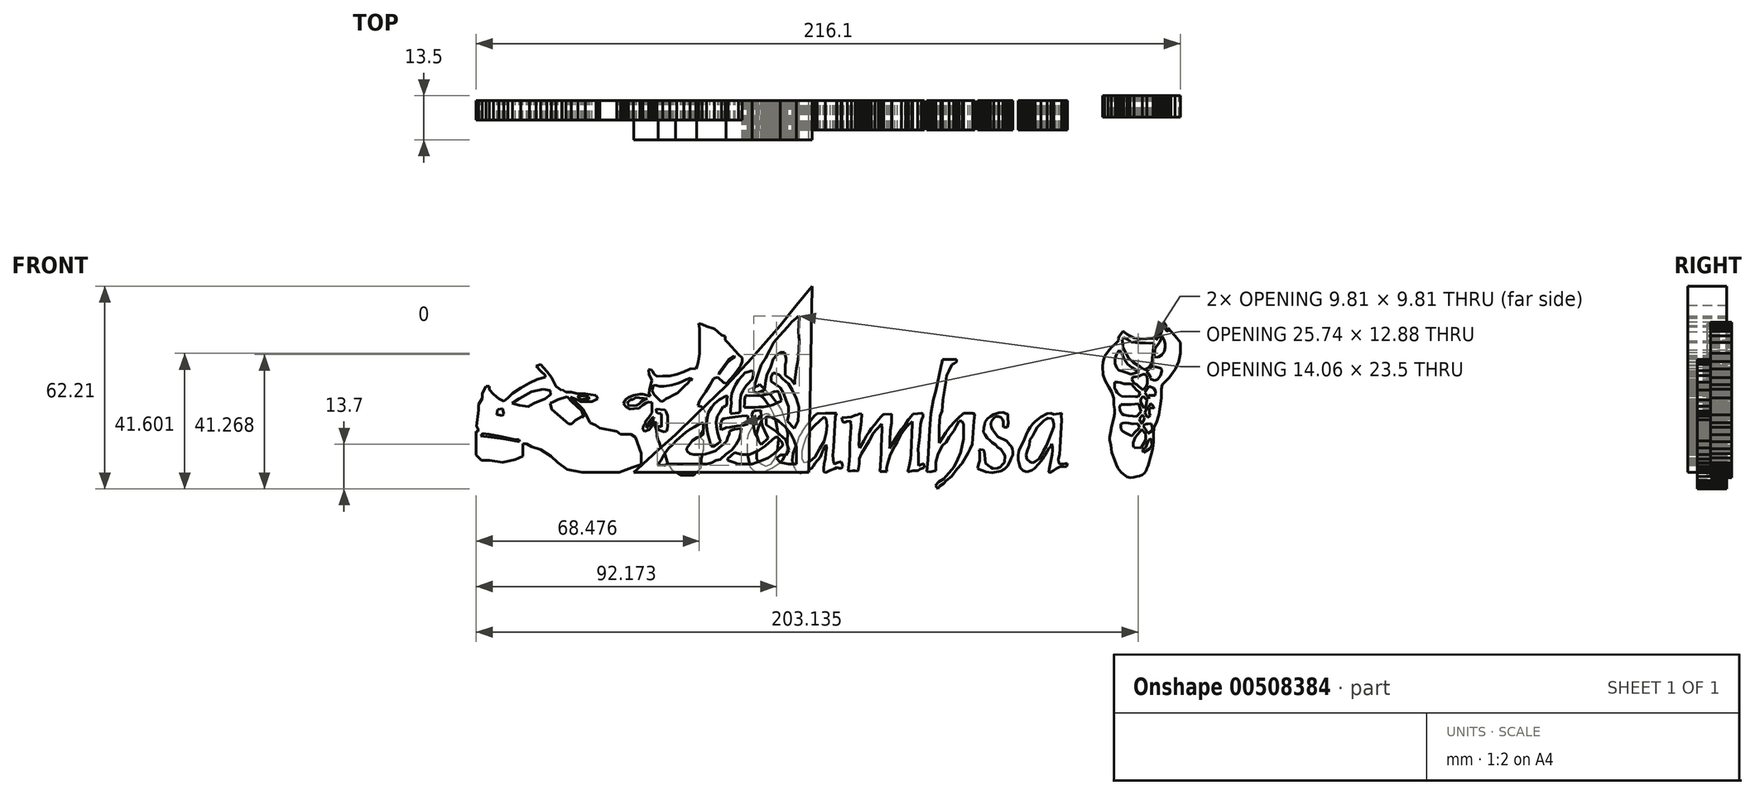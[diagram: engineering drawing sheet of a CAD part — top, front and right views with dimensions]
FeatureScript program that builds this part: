
annotation { "Feature Type Name" : "Feature", "Feature Type Description" : "" }
export const myFeature = defineFeature(function(context is Context, id is Id, definition is map)
    precondition{}
    {
        {
            var Q0;
            Q0=qCreatedBy(makeId("Front.planeOp"),FACE);
            var sketch = newSketch(context, id + "F0", { "sketchPlane" : qUnion([Q0])});
            skLineSegment(sketch, "E0", {"start": v(-52.16, 21.85) * mm, "end": v(-53.77, 22.66) * mm});
            skLineSegment(sketch, "E1", {"start": v(-53.77, 22.66) * mm, "end": v(-55.38, 23.98) * mm});
            skLineSegment(sketch, "E2", {"start": v(-55.38, 23.98) * mm, "end": v(-56.65, 25.48) * mm});
            skLineSegment(sketch, "E3", {"start": v(-56.65, 25.48) * mm, "end": v(-56.65, 26.4) * mm});
            skLineSegment(sketch, "E4", {"start": v(-56.65, 26.4) * mm, "end": v(-57.68, 26.4) * mm});
            skLineSegment(sketch, "E5", {"start": v(-57.68, 26.4) * mm, "end": v(-58.83, 24.27) * mm});
            skLineSegment(sketch, "E6", {"start": v(-58.83, 24.27) * mm, "end": v(-58.83, 22.72) * mm});
            skLineSegment(sketch, "E7", {"start": v(-58.83, 22.72) * mm, "end": v(-59.93, 20.82) * mm});
            skLineSegment(sketch, "E8", {"start": v(-59.93, 20.82) * mm, "end": v(-59.93, 19.15) * mm});
            skLineSegment(sketch, "E9", {"start": v(-59.93, 19.15) * mm, "end": v(-60.56, 14.31) * mm});
            skLineSegment(sketch, "E10", {"start": v(-60.56, 14.31) * mm, "end": v(-60.1, 13.22) * mm});
            skLineSegment(sketch, "E11", {"start": v(-60.1, 13.22) * mm, "end": v(-60.1, 12.58) * mm});
            skLineSegment(sketch, "E12", {"start": v(-60.1, 12.58) * mm, "end": v(-60.68, 12.58) * mm});
            skLineSegment(sketch, "E13", {"start": v(-60.68, 12.58) * mm, "end": v(-60.68, 10.91) * mm});
            skLineSegment(sketch, "E14", {"start": v(-60.68, 10.91) * mm, "end": v(-60.68, 7.7) * mm});
            skLineSegment(sketch, "E15", {"start": v(-60.68, 7.7) * mm, "end": v(-60.68, 5.33) * mm});
            skLineSegment(sketch, "E16", {"start": v(-60.68, 5.33) * mm, "end": v(-59, 3.66) * mm});
            skLineSegment(sketch, "E17", {"start": v(-59, 3.66) * mm, "end": v(-56.47, 3.66) * mm});
            skLineSegment(sketch, "E18", {"start": v(-56.47, 3.66) * mm, "end": v(-52.5, 3.14) * mm});
            skLineSegment(sketch, "E19", {"start": v(-52.5, 3.14) * mm, "end": v(-48.59, 4) * mm});
            skLineSegment(sketch, "E20", {"start": v(-48.59, 4) * mm, "end": v(-46.34, 4.99) * mm});
            skLineSegment(sketch, "E21", {"start": v(-46.34, 4.99) * mm, "end": v(-46.34, 7.17) * mm});
            skLineSegment(sketch, "E22", {"start": v(-46.34, 7.17) * mm, "end": v(-46.34, 8.78) * mm});
            skLineSegment(sketch, "E23", {"start": v(-46.34, 8.78) * mm, "end": v(-45.25, 8.78) * mm});
            skLineSegment(sketch, "E24", {"start": v(-45.25, 8.78) * mm, "end": v(-43.7, 7.92) * mm});
            skLineSegment(sketch, "E25", {"start": v(-43.7, 7.92) * mm, "end": v(-40.93, 7) * mm});
            skLineSegment(sketch, "E26", {"start": v(-40.93, 7) * mm, "end": v(-37.7, 5.04) * mm});
            skLineSegment(sketch, "E27", {"start": v(-37.7, 5.04) * mm, "end": v(-35.64, 3.09) * mm});
            skLineSegment(sketch, "E28", {"start": v(-35.64, 3.09) * mm, "end": v(-32.76, 0.96) * mm});
            skLineSegment(sketch, "E29", {"start": v(-32.76, 0.96) * mm, "end": v(-28.2, 0) * mm});
            skLineSegment(sketch, "E30", {"start": v(-28.2, 0) * mm, "end": v(-23.03, 0) * mm});
            skLineSegment(sketch, "E31", {"start": v(-23.03, 0) * mm, "end": v(-16.7, 0) * mm});
            skLineSegment(sketch, "E32", {"start": v(-16.7, 0) * mm, "end": v(-12.72, 1.53) * mm});
            skLineSegment(sketch, "E33", {"start": v(-12.72, 1.53) * mm, "end": v(-10.02, 2.51) * mm});
            skLineSegment(sketch, "E34", {"start": v(-10.02, 2.51) * mm, "end": v(-10.02, 3.32) * mm});
            skLineSegment(sketch, "E35", {"start": v(-10.02, 3.32) * mm, "end": v(-10.02, 5.9) * mm});
            skLineSegment(sketch, "E36", {"start": v(-10.02, 5.9) * mm, "end": v(-11.8, 10.86) * mm});
            skLineSegment(sketch, "E37", {"start": v(-11.8, 10.86) * mm, "end": v(-13.24, 11.66) * mm});
            skLineSegment(sketch, "E38", {"start": v(-13.24, 11.66) * mm, "end": v(-16.4, 11.66) * mm});
            skLineSegment(sketch, "E39", {"start": v(-16.4, 11.66) * mm, "end": v(-17.5, 12.58) * mm});
            skLineSegment(sketch, "E40", {"start": v(-17.5, 12.58) * mm, "end": v(-22.74, 13.62) * mm});
            skLineSegment(sketch, "E41", {"start": v(-22.74, 13.62) * mm, "end": v(-24, 14.48) * mm});
            skLineSegment(sketch, "E42", {"start": v(-24, 14.48) * mm, "end": v(-25.73, 15.23) * mm});
            skLineSegment(sketch, "E43", {"start": v(-25.73, 15.23) * mm, "end": v(-26.54, 16.96) * mm});
            skLineSegment(sketch, "E44", {"start": v(-26.54, 16.96) * mm, "end": v(-27.92, 19.5) * mm});
            skLineSegment(sketch, "E45", {"start": v(-27.92, 19.5) * mm, "end": v(-30.86, 22.37) * mm});
            skLineSegment(sketch, "E46", {"start": v(-30.86, 22.37) * mm, "end": v(-31.72, 23.12) * mm});
            skLineSegment(sketch, "E47", {"start": v(-31.72, 23.12) * mm, "end": v(-29.42, 22.26) * mm});
            skLineSegment(sketch, "E48", {"start": v(-29.42, 22.26) * mm, "end": v(-28.61, 21.8) * mm});
            skLineSegment(sketch, "E49", {"start": v(-28.61, 21.8) * mm, "end": v(-26.42, 21.8) * mm});
            skLineSegment(sketch, "E50", {"start": v(-26.42, 21.8) * mm, "end": v(-25.1, 21.8) * mm});
            skLineSegment(sketch, "E51", {"start": v(-25.1, 21.8) * mm, "end": v(-23.37, 22.6) * mm});
            skLineSegment(sketch, "E52", {"start": v(-23.37, 22.6) * mm, "end": v(-23.86, 23.64) * mm});
            skLineSegment(sketch, "E53", {"start": v(-23.86, 23.64) * mm, "end": v(-27.12, 24.16) * mm});
            skLineSegment(sketch, "E54", {"start": v(-27.12, 24.16) * mm, "end": v(-29.42, 24.16) * mm});
            skLineSegment(sketch, "E55", {"start": v(-29.42, 24.16) * mm, "end": v(-31.5, 24.62) * mm});
            skLineSegment(sketch, "E56", {"start": v(-31.5, 24.62) * mm, "end": v(-33.16, 24.62) * mm});
            skLineSegment(sketch, "E57", {"start": v(-33.16, 24.62) * mm, "end": v(-34.25, 25.42) * mm});
            skLineSegment(sketch, "E58", {"start": v(-34.25, 25.42) * mm, "end": v(-34.44, 25.17) * mm});
            skLineSegment(sketch, "E59", {"start": v(-34.44, 25.17) * mm, "end": v(-36.19, 26.46) * mm});
            skLineSegment(sketch, "E60", {"start": v(-36.19, 26.46) * mm, "end": v(-37.53, 29.22) * mm});
            skLineSegment(sketch, "E61", {"start": v(-37.53, 29.22) * mm, "end": v(-38.92, 31.06) * mm});
            skLineSegment(sketch, "E62", {"start": v(-38.92, 31.06) * mm, "end": v(-40.93, 33.2) * mm});
            skLineSegment(sketch, "E63", {"start": v(-40.93, 33.2) * mm, "end": v(-42.26, 32.62) * mm});
            skLineSegment(sketch, "E64", {"start": v(-42.26, 32.62) * mm, "end": v(-40.7, 31) * mm});
            skLineSegment(sketch, "E65", {"start": v(-40.7, 31) * mm, "end": v(-39.43, 29.85) * mm});
            skLineSegment(sketch, "E66", {"start": v(-39.43, 29.85) * mm, "end": v(-39.43, 29.22) * mm});
            skLineSegment(sketch, "E67", {"start": v(-39.43, 29.22) * mm, "end": v(-41.85, 28.65) * mm});
            skLineSegment(sketch, "E68", {"start": v(-41.85, 28.65) * mm, "end": v(-44.33, 27.44) * mm});
            skLineSegment(sketch, "E69", {"start": v(-44.33, 27.44) * mm, "end": v(-46.98, 26) * mm});
            skLineSegment(sketch, "E70", {"start": v(-46.98, 26) * mm, "end": v(-49.57, 24.33) * mm});
            skLineSegment(sketch, "E71", {"start": v(-49.57, 24.33) * mm, "end": v(-50.9, 22.95) * mm});
            skLineSegment(sketch, "E72", {"start": v(-50.9, 22.95) * mm, "end": v(-52.16, 21.85) * mm});
            skLineSegment(sketch, "E73", {"start": v(-37.94, 21.22) * mm, "end": v(-37.48, 19.38) * mm});
            skLineSegment(sketch, "E74", {"start": v(-37.48, 19.38) * mm, "end": v(-32.3, 14.89) * mm});
            skLineSegment(sketch, "E75", {"start": v(-32.3, 14.89) * mm, "end": v(-31.32, 14.89) * mm});
            skLineSegment(sketch, "E76", {"start": v(-31.32, 14.89) * mm, "end": v(-30.17, 16.04) * mm});
            skLineSegment(sketch, "E77", {"start": v(-30.17, 16.04) * mm, "end": v(-28.2, 17.13) * mm});
            skLineSegment(sketch, "E78", {"start": v(-28.2, 17.13) * mm, "end": v(-27.7, 16.96) * mm});
            skLineSegment(sketch, "E79", {"start": v(-27.7, 16.96) * mm, "end": v(-28.27, 18.97) * mm});
            skLineSegment(sketch, "E80", {"start": v(-28.27, 18.97) * mm, "end": v(-31.38, 21.77) * mm});
            skPoint(sketch, "E80.endSnap0", {"position": v(-59.38, 21.77) * mm});
            skLineSegment(sketch, "E81", {"start": v(-31.38, 21.77) * mm, "end": v(-32.76, 23.3) * mm});
            skLineSegment(sketch, "E82", {"start": v(-32.76, 23.3) * mm, "end": v(-35.52, 22.43) * mm});
            skLineSegment(sketch, "E83", {"start": v(-35.52, 22.43) * mm, "end": v(-36.84, 21.74) * mm});
            skLineSegment(sketch, "E84", {"start": v(-36.84, 21.74) * mm, "end": v(-37.94, 21.22) * mm});
            skLineSegment(sketch, "E85", {"start": v(-35.12, 21.22) * mm, "end": v(-33.62, 22.14) * mm});
            skLineSegment(sketch, "E86", {"start": v(-33.62, 22.14) * mm, "end": v(-32.63, 22.28) * mm});
            skLineSegment(sketch, "E87", {"start": v(-32.63, 22.28) * mm, "end": v(-31.9, 21.34) * mm});
            skLineSegment(sketch, "E88", {"start": v(-31.9, 21.34) * mm, "end": v(-30.56, 20.1) * mm});
            skLineSegment(sketch, "E89", {"start": v(-30.56, 20.1) * mm, "end": v(-29.1, 19) * mm});
            skLineSegment(sketch, "E90", {"start": v(-29.1, 19) * mm, "end": v(-29.1, 18.34) * mm});
            skLineSegment(sketch, "E91", {"start": v(-29.1, 18.34) * mm, "end": v(-30.3, 17.83) * mm});
            skLineSegment(sketch, "E92", {"start": v(-30.3, 17.83) * mm, "end": v(-31.17, 17.23) * mm});
            skLineSegment(sketch, "E93", {"start": v(-31.17, 17.23) * mm, "end": v(-31.9, 17.68) * mm});
            skLineSegment(sketch, "E94", {"start": v(-31.9, 17.68) * mm, "end": v(-33.02, 18.94) * mm});
            skLineSegment(sketch, "E95", {"start": v(-33.02, 18.94) * mm, "end": v(-33.88, 19.97) * mm});
            skLineSegment(sketch, "E96", {"start": v(-33.88, 19.97) * mm, "end": v(-34.56, 20.6) * mm});
            skLineSegment(sketch, "E97", {"start": v(-34.56, 20.6) * mm, "end": v(-35.12, 21.22) * mm});
            skLineSegment(sketch, "E98", {"start": v(-26.17, 23.22) * mm, "end": v(-28.2, 23.54) * mm});
            skLineSegment(sketch, "E99", {"start": v(-28.2, 23.54) * mm, "end": v(-29.56, 23.54) * mm});
            skLineSegment(sketch, "E100", {"start": v(-29.56, 23.54) * mm, "end": v(-29.32, 23.18) * mm});
            skLineSegment(sketch, "E101", {"start": v(-29.32, 23.18) * mm, "end": v(-28.45, 22.43) * mm});
            skLineSegment(sketch, "E102", {"start": v(-28.45, 22.43) * mm, "end": v(-27.03, 22.67) * mm});
            skLineSegment(sketch, "E103", {"start": v(-27.03, 22.67) * mm, "end": v(-26.03, 22.52) * mm});
            skLineSegment(sketch, "E104", {"start": v(-26.03, 22.52) * mm, "end": v(-26.17, 23.22) * mm});
            skLineSegment(sketch, "E105", {"start": v(-49.66, 21.22) * mm, "end": v(-47.54, 22.67) * mm});
            skLineSegment(sketch, "E106", {"start": v(-47.54, 22.67) * mm, "end": v(-43.66, 24.84) * mm});
            skLineSegment(sketch, "E107", {"start": v(-43.66, 24.84) * mm, "end": v(-40.16, 25.54) * mm});
            skLineSegment(sketch, "E108", {"start": v(-40.16, 25.54) * mm, "end": v(-38.01, 25.2) * mm});
            skLineSegment(sketch, "E109", {"start": v(-38.01, 25.2) * mm, "end": v(-37.8, 23.87) * mm});
            skLineSegment(sketch, "E110", {"start": v(-37.8, 23.87) * mm, "end": v(-39.54, 22.67) * mm});
            skLineSegment(sketch, "E111", {"start": v(-39.54, 22.67) * mm, "end": v(-42.86, 21.22) * mm});
            skLineSegment(sketch, "E112", {"start": v(-42.86, 21.22) * mm, "end": v(-44.7, 20.18) * mm});
            skLineSegment(sketch, "E113", {"start": v(-44.7, 20.18) * mm, "end": v(-47.4, 20.6) * mm});
            skLineSegment(sketch, "E114", {"start": v(-47.4, 20.6) * mm, "end": v(-49.66, 21.22) * mm});
            skLineSegment(sketch, "E115", {"start": v(-59.35, 11.23) * mm, "end": v(-58.72, 11.96) * mm});
            skLineSegment(sketch, "E116", {"start": v(-58.72, 11.96) * mm, "end": v(-56.7, 11.76) * mm});
            skLineSegment(sketch, "E117", {"start": v(-56.7, 11.76) * mm, "end": v(-53.3, 11.13) * mm});
            skLineSegment(sketch, "E118", {"start": v(-53.3, 11.13) * mm, "end": v(-49.28, 10.26) * mm});
            skLineSegment(sketch, "E119", {"start": v(-49.28, 10.26) * mm, "end": v(-47.5, 10.02) * mm});
            skLineSegment(sketch, "E120", {"start": v(-47.5, 10.02) * mm, "end": v(-47.35, 9.44) * mm});
            skLineSegment(sketch, "E121", {"start": v(-47.35, 9.44) * mm, "end": v(-51.46, 10.17) * mm});
            skLineSegment(sketch, "E122", {"start": v(-51.46, 10.17) * mm, "end": v(-55.14, 10.65) * mm});
            skLineSegment(sketch, "E123", {"start": v(-55.14, 10.65) * mm, "end": v(-59.35, 11.23) * mm});
            skLineSegment(sketch, "E124", {"start": v(-54.08, 19.36) * mm, "end": v(-52.58, 19.66) * mm});
            skLineSegment(sketch, "E125", {"start": v(-52.58, 19.66) * mm, "end": v(-52.23, 17.94) * mm});
            skLineSegment(sketch, "E126", {"start": v(-52.23, 17.94) * mm, "end": v(-52.66, 17.45) * mm});
            skLineSegment(sketch, "E127", {"start": v(-52.66, 17.45) * mm, "end": v(-54.32, 17.81) * mm});
            skLineSegment(sketch, "E128", {"start": v(-54.32, 17.81) * mm, "end": v(-54.08, 19.36) * mm});
            skLineSegment(sketch, "E129", {"start": v(-6.02, 22.75) * mm, "end": v(-4.76, 20.8) * mm});
            skLineSegment(sketch, "E130", {"start": v(-4.76, 20.8) * mm, "end": v(-3.96, 17.79) * mm});
            skLineSegment(sketch, "E131", {"start": v(-3.96, 17.79) * mm, "end": v(-2.58, 15.86) * mm});
            skLineSegment(sketch, "E132", {"start": v(-2.58, 15.86) * mm, "end": v(0, 14.17) * mm});
            skLineSegment(sketch, "E133", {"start": v(0, 14.17) * mm, "end": v(2.62, 14.17) * mm});
            skLineSegment(sketch, "E134", {"start": v(2.62, 14.17) * mm, "end": v(4.09, 14.17) * mm});
            skLineSegment(sketch, "E135", {"start": v(4.09, 14.17) * mm, "end": v(6.37, 16.45) * mm});
            skLineSegment(sketch, "E136", {"start": v(6.37, 16.45) * mm, "end": v(6.37, 19.18) * mm});
            skLineSegment(sketch, "E137", {"start": v(6.37, 19.18) * mm, "end": v(7.18, 22.3) * mm});
            skLineSegment(sketch, "E138", {"start": v(7.18, 22.3) * mm, "end": v(7.18, 24.67) * mm});
            skLineSegment(sketch, "E139", {"start": v(7.18, 24.67) * mm, "end": v(6.26, 25.57) * mm});
            skLineSegment(sketch, "E140", {"start": v(6.26, 25.57) * mm, "end": v(6.26, 26.6) * mm});
            skLineSegment(sketch, "E141", {"start": v(6.26, 26.6) * mm, "end": v(7.8, 29.07) * mm});
            skLineSegment(sketch, "E142", {"start": v(7.8, 29.07) * mm, "end": v(7.85, 33.37) * mm});
            skLineSegment(sketch, "E143", {"start": v(7.85, 33.37) * mm, "end": v(7.18, 34.4) * mm});
            skLineSegment(sketch, "E144", {"start": v(7.18, 34.4) * mm, "end": v(6.45, 35.3) * mm});
            skLineSegment(sketch, "E145", {"start": v(6.45, 35.3) * mm, "end": v(5.32, 35.46) * mm});
            skLineSegment(sketch, "E146", {"start": v(5.32, 35.46) * mm, "end": v(5.89, 37) * mm});
            skLineSegment(sketch, "E147", {"start": v(5.89, 37) * mm, "end": v(6.68, 38.17) * mm});
            skLineSegment(sketch, "E148", {"start": v(6.68, 38.17) * mm, "end": v(7.78, 39.83) * mm});
            skLineSegment(sketch, "E149", {"start": v(7.78, 39.83) * mm, "end": v(9.12, 41.87) * mm});
            skLineSegment(sketch, "E150", {"start": v(9.12, 41.87) * mm, "end": v(10.26, 43.87) * mm});
            skLineSegment(sketch, "E151", {"start": v(10.26, 43.87) * mm, "end": v(11.51, 44.21) * mm});
            skLineSegment(sketch, "E152", {"start": v(11.51, 44.21) * mm, "end": v(13.22, 42.65) * mm});
            skLineSegment(sketch, "E153", {"start": v(13.22, 42.65) * mm, "end": v(14.1, 42.32) * mm});
            skLineSegment(sketch, "E154", {"start": v(14.1, 42.32) * mm, "end": v(16.44, 44.88) * mm});
            skLineSegment(sketch, "E155", {"start": v(16.44, 44.88) * mm, "end": v(18.49, 47.7) * mm});
            skLineSegment(sketch, "E156", {"start": v(18.49, 47.7) * mm, "end": v(18.92, 49.06) * mm});
            skLineSegment(sketch, "E157", {"start": v(18.92, 49.06) * mm, "end": v(18.92, 50.25) * mm});
            skLineSegment(sketch, "E158", {"start": v(18.92, 50.25) * mm, "end": v(17.84, 51.21) * mm});
            skLineSegment(sketch, "E159", {"start": v(17.84, 51.21) * mm, "end": v(14.6, 54.74) * mm});
            skLineSegment(sketch, "E160", {"start": v(14.6, 54.74) * mm, "end": v(13.8, 55.68) * mm});
            skLineSegment(sketch, "E161", {"start": v(13.8, 55.68) * mm, "end": v(13.8, 56.76) * mm});
            skLineSegment(sketch, "E162", {"start": v(13.8, 56.76) * mm, "end": v(12.64, 57.2) * mm});
            skLineSegment(sketch, "E163", {"start": v(12.64, 57.2) * mm, "end": v(10.42, 59.17) * mm});
            skLineSegment(sketch, "E164", {"start": v(10.42, 59.17) * mm, "end": v(8, 59.93) * mm});
            skLineSegment(sketch, "E165", {"start": v(8, 59.93) * mm, "end": v(6.58, 60.49) * mm});
            skLineSegment(sketch, "E166", {"start": v(6.58, 60.49) * mm, "end": v(5.66, 60.78) * mm});
            skLineSegment(sketch, "E167", {"start": v(5.66, 60.78) * mm, "end": v(5.89, 59.11) * mm});
            skLineSegment(sketch, "E168", {"start": v(5.89, 59.11) * mm, "end": v(5.89, 55.85) * mm});
            skLineSegment(sketch, "E169", {"start": v(5.89, 55.85) * mm, "end": v(5.89, 53.23) * mm});
            skLineSegment(sketch, "E170", {"start": v(5.89, 53.23) * mm, "end": v(5.89, 51.55) * mm});
            skLineSegment(sketch, "E171", {"start": v(5.89, 51.55) * mm, "end": v(5.5, 49.05) * mm});
            skLineSegment(sketch, "E172", {"start": v(5.5, 49.05) * mm, "end": v(5.18, 47.54) * mm});
            skLineSegment(sketch, "E173", {"start": v(5.18, 47.54) * mm, "end": v(4.75, 46.95) * mm});
            skLineSegment(sketch, "E174", {"start": v(4.75, 46.95) * mm, "end": v(2.97, 46.76) * mm});
            skLineSegment(sketch, "E175", {"start": v(2.97, 46.76) * mm, "end": v(1.05, 45.9) * mm});
            skLineSegment(sketch, "E176", {"start": v(1.05, 45.9) * mm, "end": v(-1.08, 45.11) * mm});
            skLineSegment(sketch, "E177", {"start": v(-1.08, 45.11) * mm, "end": v(-3.26, 44.62) * mm});
            skLineSegment(sketch, "E178", {"start": v(-3.26, 44.62) * mm, "end": v(-5.42, 44.59) * mm});
            skLineSegment(sketch, "E179", {"start": v(-5.42, 44.59) * mm, "end": v(-7.15, 44.48) * mm});
            skLineSegment(sketch, "E180", {"start": v(-7.15, 44.48) * mm, "end": v(-8.14, 45.28) * mm});
            skLineSegment(sketch, "E181", {"start": v(-8.14, 45.28) * mm, "end": v(-8.58, 46.16) * mm});
            skLineSegment(sketch, "E182", {"start": v(-8.58, 46.16) * mm, "end": v(-9.05, 46.65) * mm});
            skLineSegment(sketch, "E183", {"start": v(-9.05, 46.65) * mm, "end": v(-9.78, 46.49) * mm});
            skLineSegment(sketch, "E184", {"start": v(-9.78, 46.49) * mm, "end": v(-9.62, 44.98) * mm});
            skLineSegment(sketch, "E185", {"start": v(-9.62, 44.98) * mm, "end": v(-9.14, 44.1) * mm});
            skLineSegment(sketch, "E186", {"start": v(-9.14, 44.1) * mm, "end": v(-8.76, 43.2) * mm});
            skLineSegment(sketch, "E187", {"start": v(-8.76, 43.2) * mm, "end": v(-8.95, 42.5) * mm});
            skLineSegment(sketch, "E188", {"start": v(-8.95, 42.5) * mm, "end": v(-9.5, 40.4) * mm});
            skLineSegment(sketch, "E189", {"start": v(-9.5, 40.4) * mm, "end": v(-9.57, 39.3) * mm});
            skLineSegment(sketch, "E190", {"start": v(-9.57, 39.3) * mm, "end": v(-9.29, 38.39) * mm});
            skLineSegment(sketch, "E191", {"start": v(-9.29, 38.39) * mm, "end": v(-11.53, 39) * mm});
            skLineSegment(sketch, "E192", {"start": v(-11.53, 39) * mm, "end": v(-12.41, 39.02) * mm});
            skLineSegment(sketch, "E193", {"start": v(-12.41, 39.02) * mm, "end": v(-14.38, 38.71) * mm});
            skLineSegment(sketch, "E194", {"start": v(-14.38, 38.71) * mm, "end": v(-15.94, 38.01) * mm});
            skLineSegment(sketch, "E195", {"start": v(-15.94, 38.01) * mm, "end": v(-16.87, 37.45) * mm});
            skLineSegment(sketch, "E196", {"start": v(-16.87, 37.45) * mm, "end": v(-17.16, 36.72) * mm});
            skLineSegment(sketch, "E197", {"start": v(-17.16, 36.72) * mm, "end": v(-17.45, 36.13) * mm});
            skLineSegment(sketch, "E198", {"start": v(-17.45, 36.13) * mm, "end": v(-16.62, 35.12) * mm});
            skLineSegment(sketch, "E199", {"start": v(-16.62, 35.12) * mm, "end": v(-15.5, 34.46) * mm});
            skLineSegment(sketch, "E200", {"start": v(-15.5, 34.46) * mm, "end": v(-14.21, 34.54) * mm});
            skLineSegment(sketch, "E201", {"start": v(-14.21, 34.54) * mm, "end": v(-12.69, 34.78) * mm});
            skLineSegment(sketch, "E202", {"start": v(-12.69, 34.78) * mm, "end": v(-11.56, 35.7) * mm});
            skLineSegment(sketch, "E203", {"start": v(-11.56, 35.7) * mm, "end": v(-10.53, 36.42) * mm});
            skLineSegment(sketch, "E204", {"start": v(-10.53, 36.42) * mm, "end": v(-9.7, 36.6) * mm});
            skLineSegment(sketch, "E205", {"start": v(-9.7, 36.6) * mm, "end": v(-8.75, 36.47) * mm});
            skLineSegment(sketch, "E206", {"start": v(-8.75, 36.47) * mm, "end": v(-8.73, 35.42) * mm});
            skLineSegment(sketch, "E207", {"start": v(-8.73, 35.42) * mm, "end": v(-8.68, 33.33) * mm});
            skLineSegment(sketch, "E208", {"start": v(-8.68, 33.33) * mm, "end": v(-9.8, 31.87) * mm});
            skLineSegment(sketch, "E209", {"start": v(-9.8, 31.87) * mm, "end": v(-10.72, 30.64) * mm});
            skLineSegment(sketch, "E210", {"start": v(-10.72, 30.64) * mm, "end": v(-10.72, 30.01) * mm});
            skLineSegment(sketch, "E211", {"start": v(-10.72, 30.01) * mm, "end": v(-11.39, 29.26) * mm});
            skLineSegment(sketch, "E212", {"start": v(-11.39, 29.26) * mm, "end": v(-11.58, 28.24) * mm});
            skLineSegment(sketch, "E213", {"start": v(-11.58, 28.24) * mm, "end": v(-11, 27.56) * mm});
            skLineSegment(sketch, "E214", {"start": v(-11, 27.56) * mm, "end": v(-9.61, 28.08) * mm});
            skLineSegment(sketch, "E215", {"start": v(-9.61, 28.08) * mm, "end": v(-8.76, 29.12) * mm});
            skLineSegment(sketch, "E216", {"start": v(-8.76, 29.12) * mm, "end": v(-8.45, 29.78) * mm});
            skLineSegment(sketch, "E217", {"start": v(-8.45, 29.78) * mm, "end": v(-8.14, 30.41) * mm});
            skLineSegment(sketch, "E218", {"start": v(-8.14, 30.41) * mm, "end": v(-7.67, 30.66) * mm});
            skLineSegment(sketch, "E219", {"start": v(-7.67, 30.66) * mm, "end": v(-7.63, 30) * mm});
            skLineSegment(sketch, "E220", {"start": v(-7.63, 30) * mm, "end": v(-7.66, 29.08) * mm});
            skLineSegment(sketch, "E221", {"start": v(-7.66, 29.08) * mm, "end": v(-7.29, 28.04) * mm});
            skLineSegment(sketch, "E222", {"start": v(-7.29, 28.04) * mm, "end": v(-7.16, 26.35) * mm});
            skLineSegment(sketch, "E223", {"start": v(-7.16, 26.35) * mm, "end": v(-6.97, 25.2) * mm});
            skLineSegment(sketch, "E224", {"start": v(-6.97, 25.2) * mm, "end": v(-6.48, 24.12) * mm});
            skLineSegment(sketch, "E225", {"start": v(-6.48, 24.12) * mm, "end": v(-6.02, 22.75) * mm});
            skLineSegment(sketch, "E226", {"start": v(-7.43, 34.47) * mm, "end": v(-4.76, 34.18) * mm});
            skLineSegment(sketch, "E227", {"start": v(-4.76, 34.18) * mm, "end": v(-4.36, 33.75) * mm});
            skLineSegment(sketch, "E228", {"start": v(-4.36, 33.75) * mm, "end": v(-3.96, 32.26) * mm});
            skLineSegment(sketch, "E229", {"start": v(-3.96, 32.26) * mm, "end": v(-3.92, 30.5) * mm});
            skLineSegment(sketch, "E230", {"start": v(-3.92, 30.5) * mm, "end": v(-3.92, 29.33) * mm});
            skLineSegment(sketch, "E231", {"start": v(-3.92, 29.33) * mm, "end": v(-4.06, 28.38) * mm});
            skLineSegment(sketch, "E232", {"start": v(-4.06, 28.38) * mm, "end": v(-4.3, 27.62) * mm});
            skLineSegment(sketch, "E233", {"start": v(-4.3, 27.62) * mm, "end": v(-5.06, 27.53) * mm});
            skLineSegment(sketch, "E234", {"start": v(-5.06, 27.53) * mm, "end": v(-5.75, 27.8) * mm});
            skLineSegment(sketch, "E235", {"start": v(-5.75, 27.8) * mm, "end": v(-6.47, 28.05) * mm});
            skLineSegment(sketch, "E236", {"start": v(-6.47, 28.05) * mm, "end": v(-6.8, 28.11) * mm});
            skLineSegment(sketch, "E237", {"start": v(-6.8, 28.11) * mm, "end": v(-7.03, 29.26) * mm});
            skLineSegment(sketch, "E238", {"start": v(-7.03, 29.26) * mm, "end": v(-5.82, 29.04) * mm});
            skLineSegment(sketch, "E239", {"start": v(-5.82, 29.04) * mm, "end": v(-5.8, 30.87) * mm});
            skLineSegment(sketch, "E240", {"start": v(-5.8, 30.87) * mm, "end": v(-5.81, 32.44) * mm});
            skLineSegment(sketch, "E241", {"start": v(-5.81, 32.44) * mm, "end": v(-5.86, 33.13) * mm});
            skLineSegment(sketch, "E242", {"start": v(-5.86, 33.13) * mm, "end": v(-6.89, 33.15) * mm});
            skLineSegment(sketch, "E243", {"start": v(-6.89, 33.15) * mm, "end": v(-7.35, 33.5) * mm});
            skLineSegment(sketch, "E244", {"start": v(-7.35, 33.5) * mm, "end": v(-7.43, 34.47) * mm});
            skLineSegment(sketch, "E245", {"start": v(-10.43, 29.05) * mm, "end": v(-9.97, 30) * mm});
            skLineSegment(sketch, "E246", {"start": v(-9.97, 30) * mm, "end": v(-9.54, 30.65) * mm});
            skLineSegment(sketch, "E247", {"start": v(-9.54, 30.65) * mm, "end": v(-8.95, 31.26) * mm});
            skLineSegment(sketch, "E248", {"start": v(-8.95, 31.26) * mm, "end": v(-8.46, 31.95) * mm});
            skLineSegment(sketch, "E249", {"start": v(-8.46, 31.95) * mm, "end": v(-8.15, 31.98) * mm});
            skLineSegment(sketch, "E250", {"start": v(-8.15, 31.98) * mm, "end": v(-8.07, 31.6) * mm});
            skLineSegment(sketch, "E251", {"start": v(-8.07, 31.6) * mm, "end": v(-8.47, 31) * mm});
            skLineSegment(sketch, "E252", {"start": v(-8.47, 31) * mm, "end": v(-8.86, 30.23) * mm});
            skLineSegment(sketch, "E253", {"start": v(-8.86, 30.23) * mm, "end": v(-9.48, 29.43) * mm});
            skLineSegment(sketch, "E254", {"start": v(-9.48, 29.43) * mm, "end": v(-10.06, 28.86) * mm});
            skLineSegment(sketch, "E255", {"start": v(-10.06, 28.86) * mm, "end": v(-10.34, 28.78) * mm});
            skLineSegment(sketch, "E256", {"start": v(-10.34, 28.78) * mm, "end": v(-10.43, 29.05) * mm});
            skLineSegment(sketch, "E257", {"start": v(-8.2, 41.87) * mm, "end": v(-8.73, 40.18) * mm});
            skLineSegment(sketch, "E258", {"start": v(-8.73, 40.18) * mm, "end": v(-8.06, 38.91) * mm});
            skLineSegment(sketch, "E259", {"start": v(-8.06, 38.91) * mm, "end": v(-5.92, 36.76) * mm});
            skLineSegment(sketch, "E260", {"start": v(-5.92, 36.76) * mm, "end": v(-5.1, 37.02) * mm});
            skLineSegment(sketch, "E261", {"start": v(-5.1, 37.02) * mm, "end": v(-4.43, 37.6) * mm});
            skLineSegment(sketch, "E262", {"start": v(-4.43, 37.6) * mm, "end": v(-3.5, 38) * mm});
            skLineSegment(sketch, "E263", {"start": v(-3.5, 38) * mm, "end": v(-2.18, 38.83) * mm});
            skLineSegment(sketch, "E264", {"start": v(-2.18, 38.83) * mm, "end": v(-0.85, 39.48) * mm});
            skLineSegment(sketch, "E265", {"start": v(-0.85, 39.48) * mm, "end": v(0.37, 40.74) * mm});
            skLineSegment(sketch, "E266", {"start": v(0.37, 40.74) * mm, "end": v(1.33, 41.62) * mm});
            skLineSegment(sketch, "E267", {"start": v(1.33, 41.62) * mm, "end": v(2.27, 42.47) * mm});
            skLineSegment(sketch, "E268", {"start": v(2.27, 42.47) * mm, "end": v(3.02, 43.3) * mm});
            skLineSegment(sketch, "E269", {"start": v(3.02, 43.3) * mm, "end": v(3.8, 43.48) * mm});
            skLineSegment(sketch, "E270", {"start": v(3.8, 43.48) * mm, "end": v(3.07, 44.02) * mm});
            skLineSegment(sketch, "E271", {"start": v(3.07, 44.02) * mm, "end": v(1.7, 43.46) * mm});
            skLineSegment(sketch, "E272", {"start": v(1.7, 43.46) * mm, "end": v(0.19, 42.67) * mm});
            skLineSegment(sketch, "E273", {"start": v(0.19, 42.67) * mm, "end": v(-0.8, 42.37) * mm});
            skLineSegment(sketch, "E274", {"start": v(-0.8, 42.37) * mm, "end": v(-2.58, 41.87) * mm});
            skLineSegment(sketch, "E275", {"start": v(-2.58, 41.87) * mm, "end": v(-5.02, 41.46) * mm});
            skLineSegment(sketch, "E276", {"start": v(-5.02, 41.46) * mm, "end": v(-6.39, 41.47) * mm});
            skLineSegment(sketch, "E277", {"start": v(-6.39, 41.47) * mm, "end": v(-7.35, 41.7) * mm});
            skLineSegment(sketch, "E278", {"start": v(-7.35, 41.7) * mm, "end": v(-8.2, 41.87) * mm});
            skLineSegment(sketch, "E279", {"start": v(-10.06, 37.62) * mm, "end": v(-12.41, 37.88) * mm});
            skLineSegment(sketch, "E280", {"start": v(-12.41, 37.88) * mm, "end": v(-13.65, 38.01) * mm});
            skLineSegment(sketch, "E281", {"start": v(-13.65, 38.01) * mm, "end": v(-14.58, 37.35) * mm});
            skLineSegment(sketch, "E282", {"start": v(-14.58, 37.35) * mm, "end": v(-15.04, 37.33) * mm});
            skLineSegment(sketch, "E283", {"start": v(-15.04, 37.33) * mm, "end": v(-15.95, 36.92) * mm});
            skLineSegment(sketch, "E284", {"start": v(-15.95, 36.92) * mm, "end": v(-16.2, 36.16) * mm});
            skLineSegment(sketch, "E285", {"start": v(-16.2, 36.16) * mm, "end": v(-15.78, 35.62) * mm});
            skLineSegment(sketch, "E286", {"start": v(-15.78, 35.62) * mm, "end": v(-14.4, 35.43) * mm});
            skLineSegment(sketch, "E287", {"start": v(-14.4, 35.43) * mm, "end": v(-13.4, 35.58) * mm});
            skLineSegment(sketch, "E288", {"start": v(-13.4, 35.58) * mm, "end": v(-12.56, 36.14) * mm});
            skLineSegment(sketch, "E289", {"start": v(-12.56, 36.14) * mm, "end": v(-12, 36.8) * mm});
            skLineSegment(sketch, "E290", {"start": v(-12, 36.8) * mm, "end": v(-11.35, 37.08) * mm});
            skLineSegment(sketch, "E291", {"start": v(-11.35, 37.08) * mm, "end": v(-10.06, 37.62) * mm});
            skLineSegment(sketch, "E292", {"start": v(11.7, 45.43) * mm, "end": v(13.07, 47.33) * mm});
            skLineSegment(sketch, "E293", {"start": v(13.07, 47.33) * mm, "end": v(14.71, 49.6) * mm});
            skLineSegment(sketch, "E294", {"start": v(14.71, 49.6) * mm, "end": v(16.6, 50.78) * mm});
            skLineSegment(sketch, "E295", {"start": v(16.6, 50.78) * mm, "end": v(16.82, 50.44) * mm});
            skLineSegment(sketch, "E296", {"start": v(16.82, 50.44) * mm, "end": v(15.34, 49.5) * mm});
            skLineSegment(sketch, "E297", {"start": v(15.34, 49.5) * mm, "end": v(14.43, 48.68) * mm});
            skLineSegment(sketch, "E298", {"start": v(14.43, 48.68) * mm, "end": v(13.44, 47.32) * mm});
            skLineSegment(sketch, "E299", {"start": v(13.44, 47.32) * mm, "end": v(12.45, 45.94) * mm});
            skLineSegment(sketch, "E300", {"start": v(12.45, 45.94) * mm, "end": v(11.87, 45.15) * mm});
            skLineSegment(sketch, "E301", {"start": v(11.87, 45.15) * mm, "end": v(11.7, 45.43) * mm});
            skSolve(sketch);
        }
        {
            var Q0;
            Q0 = qSketchRegion(id + "F0", true);
            extrude(context, id + "F1", {"entities" : qUnion([Q0]), "depth" : 6 * mm});
        }
        {
            var Q0;
            Q0=qCreatedBy(makeId("Front.planeOp"),FACE);
            var sketch = newSketch(context, id + "F2", { "sketchPlane" : qUnion([Q0])});
            skLineSegment(sketch, "E302", {"start": v(20.35, -39.22) * mm, "end": v(25.12, -33.39) * mm});
            skLineSegment(sketch, "E303", {"start": v(25.12, -33.39) * mm, "end": v(30.07, -27.2) * mm});
            skLineSegment(sketch, "E304", {"start": v(30.07, -27.2) * mm, "end": v(38.73, -17.3) * mm});
            skLineSegment(sketch, "E305", {"start": v(38.73, -17.3) * mm, "end": v(46.69, -8.64) * mm});
            skLineSegment(sketch, "E306", {"start": v(46.69, -8.64) * mm, "end": v(55.7, 0) * mm});
            skLineSegment(sketch, "E307", {"start": v(55.7, 0) * mm, "end": v(62.24, 6.4) * mm});
            skLineSegment(sketch, "E308", {"start": v(62.24, 6.4) * mm, "end": v(67.6, 11.08) * mm});
            skLineSegment(sketch, "E309", {"start": v(67.6, 11.08) * mm, "end": v(73.91, 16.95) * mm});
            skLineSegment(sketch, "E310", {"start": v(73.91, 16.95) * mm, "end": v(75.03, 17.98) * mm});
            skLineSegment(sketch, "E311", {"start": v(75.03, 17.98) * mm, "end": v(21.36, 17.98) * mm});
            skLineSegment(sketch, "E312", {"start": v(21.36, 17.98) * mm, "end": v(20.35, -39.22) * mm});
            skLineSegment(sketch, "E313", {"start": v(25.12, 15.33) * mm, "end": v(25.12, 12.7) * mm});
            skLineSegment(sketch, "E314", {"start": v(25.12, 12.7) * mm, "end": v(25.12, 10.18) * mm});
            skLineSegment(sketch, "E315", {"start": v(25.12, 10.18) * mm, "end": v(25.94, 7.97) * mm});
            skLineSegment(sketch, "E316", {"start": v(25.94, 7.97) * mm, "end": v(26.89, 5.98) * mm});
            skLineSegment(sketch, "E317", {"start": v(26.89, 5.98) * mm, "end": v(28.67, 3.77) * mm});
            skLineSegment(sketch, "E318", {"start": v(28.67, 3.77) * mm, "end": v(30.46, 2.3) * mm});
            skLineSegment(sketch, "E319", {"start": v(30.46, 2.3) * mm, "end": v(32.67, 1.04) * mm});
            skLineSegment(sketch, "E320", {"start": v(32.67, 1.04) * mm, "end": v(34.35, 0.93) * mm});
            skLineSegment(sketch, "E321", {"start": v(34.35, 0.93) * mm, "end": v(34.35, 3.35) * mm});
            skLineSegment(sketch, "E322", {"start": v(34.35, 3.35) * mm, "end": v(31.3, 5.35) * mm});
            skLineSegment(sketch, "E323", {"start": v(31.3, 5.35) * mm, "end": v(28.46, 7.87) * mm});
            skLineSegment(sketch, "E324", {"start": v(28.46, 7.87) * mm, "end": v(27.41, 11.02) * mm});
            skLineSegment(sketch, "E325", {"start": v(27.41, 11.02) * mm, "end": v(28.36, 12.6) * mm});
            skLineSegment(sketch, "E326", {"start": v(28.36, 12.6) * mm, "end": v(30.04, 12.6) * mm});
            skLineSegment(sketch, "E327", {"start": v(30.04, 12.6) * mm, "end": v(31.2, 13.65) * mm});
            skLineSegment(sketch, "E328", {"start": v(31.2, 13.65) * mm, "end": v(30.1, 14.86) * mm});
            skLineSegment(sketch, "E329", {"start": v(30.1, 14.86) * mm, "end": v(27.57, 15.44) * mm});
            skLineSegment(sketch, "E330", {"start": v(27.57, 15.44) * mm, "end": v(25.12, 15.33) * mm});
            skLineSegment(sketch, "E331", {"start": v(29.34, 9.65) * mm, "end": v(30.62, 10.97) * mm});
            skPoint(sketch, "E331.endSnap0", {"position": v(30.62, 13.12) * mm});
            skLineSegment(sketch, "E332", {"start": v(30.62, 10.97) * mm, "end": v(32.03, 12.26) * mm});
            skLineSegment(sketch, "E333", {"start": v(32.03, 12.26) * mm, "end": v(33.8, 13.45) * mm});
            skLineSegment(sketch, "E334", {"start": v(33.8, 13.45) * mm, "end": v(35.97, 14.42) * mm});
            skLineSegment(sketch, "E335", {"start": v(35.97, 14.42) * mm, "end": v(38.67, 15.33) * mm});
            skLineSegment(sketch, "E336", {"start": v(38.67, 15.33) * mm, "end": v(41.14, 15.33) * mm});
            skLineSegment(sketch, "E337", {"start": v(41.14, 15.33) * mm, "end": v(42.86, 15.33) * mm});
            skLineSegment(sketch, "E338", {"start": v(42.86, 15.33) * mm, "end": v(44.68, 14.77) * mm});
            skLineSegment(sketch, "E339", {"start": v(44.68, 14.77) * mm, "end": v(46.18, 14.24) * mm});
            skLineSegment(sketch, "E340", {"start": v(46.18, 14.24) * mm, "end": v(46.18, 13.76) * mm});
            skLineSegment(sketch, "E341", {"start": v(46.18, 13.76) * mm, "end": v(44.9, 12.6) * mm});
            skLineSegment(sketch, "E342", {"start": v(44.9, 12.6) * mm, "end": v(44, 11.78) * mm});
            skLineSegment(sketch, "E343", {"start": v(44, 11.78) * mm, "end": v(41.98, 12.48) * mm});
            skLineSegment(sketch, "E344", {"start": v(41.98, 12.48) * mm, "end": v(39.5, 12.48) * mm});
            skLineSegment(sketch, "E345", {"start": v(39.5, 12.48) * mm, "end": v(36.68, 11.15) * mm});
            skLineSegment(sketch, "E346", {"start": v(36.68, 11.15) * mm, "end": v(34.6, 9.82) * mm});
            skLineSegment(sketch, "E347", {"start": v(34.6, 9.82) * mm, "end": v(33.1, 8.45) * mm});
            skLineSegment(sketch, "E348", {"start": v(33.1, 8.45) * mm, "end": v(31.61, 7.1) * mm});
            skLineSegment(sketch, "E349", {"start": v(31.61, 7.1) * mm, "end": v(30.93, 7.1) * mm});
            skLineSegment(sketch, "E350", {"start": v(30.93, 7.1) * mm, "end": v(29.42, 8.77) * mm});
            skLineSegment(sketch, "E351", {"start": v(29.42, 8.77) * mm, "end": v(29.34, 9.65) * mm});
            skLineSegment(sketch, "E352", {"start": v(33.72, 7.4) * mm, "end": v(34.88, 8.45) * mm});
            skLineSegment(sketch, "E353", {"start": v(34.88, 8.45) * mm, "end": v(35.87, 9.35) * mm});
            skLineSegment(sketch, "E354", {"start": v(35.87, 9.35) * mm, "end": v(36.68, 8.45) * mm});
            skLineSegment(sketch, "E355", {"start": v(36.68, 8.45) * mm, "end": v(37.12, 7.13) * mm});
            skLineSegment(sketch, "E356", {"start": v(37.12, 7.13) * mm, "end": v(37.83, 5.8) * mm});
            skLineSegment(sketch, "E357", {"start": v(37.83, 5.8) * mm, "end": v(38.22, 4.12) * mm});
            skLineSegment(sketch, "E358", {"start": v(38.22, 4.12) * mm, "end": v(38.36, 2.93) * mm});
            skLineSegment(sketch, "E359", {"start": v(38.36, 2.93) * mm, "end": v(38.36, 1.6) * mm});
            skLineSegment(sketch, "E360", {"start": v(38.36, 1.6) * mm, "end": v(38.84, 0.1) * mm});
            skLineSegment(sketch, "E361", {"start": v(38.84, 0.1) * mm, "end": v(38.27, -1) * mm});
            skLineSegment(sketch, "E362", {"start": v(38.27, -1) * mm, "end": v(37.38, -1.05) * mm});
            skLineSegment(sketch, "E363", {"start": v(37.38, -1.05) * mm, "end": v(36.06, -1.14) * mm});
            skLineSegment(sketch, "E364", {"start": v(36.06, -1.14) * mm, "end": v(35.92, 0.93) * mm});
            skLineSegment(sketch, "E365", {"start": v(35.92, 0.93) * mm, "end": v(35.75, 2.49) * mm});
            skLineSegment(sketch, "E366", {"start": v(35.75, 2.49) * mm, "end": v(35.48, 3.73) * mm});
            skLineSegment(sketch, "E367", {"start": v(35.48, 3.73) * mm, "end": v(34.9, 5.14) * mm});
            skLineSegment(sketch, "E368", {"start": v(34.9, 5.14) * mm, "end": v(34.25, 6.47) * mm});
            skLineSegment(sketch, "E369", {"start": v(34.25, 6.47) * mm, "end": v(33.72, 7.4) * mm});
            skLineSegment(sketch, "E370", {"start": v(42.06, 4.5) * mm, "end": v(42.3, 6.25) * mm});
            skLineSegment(sketch, "E371", {"start": v(42.3, 6.25) * mm, "end": v(42.68, 7.68) * mm});
            skLineSegment(sketch, "E372", {"start": v(42.68, 7.68) * mm, "end": v(43.65, 9.4) * mm});
            skLineSegment(sketch, "E373", {"start": v(43.65, 9.4) * mm, "end": v(45, 11.09) * mm});
            skLineSegment(sketch, "E374", {"start": v(45, 11.09) * mm, "end": v(46.72, 12.3) * mm});
            skLineSegment(sketch, "E375", {"start": v(46.72, 12.3) * mm, "end": v(48.52, 13.95) * mm});
            skLineSegment(sketch, "E376", {"start": v(48.52, 13.95) * mm, "end": v(49.72, 14.24) * mm});
            skLineSegment(sketch, "E377", {"start": v(49.72, 14.24) * mm, "end": v(51.22, 14.93) * mm});
            skLineSegment(sketch, "E378", {"start": v(51.22, 14.93) * mm, "end": v(52.74, 15.33) * mm});
            skLineSegment(sketch, "E379", {"start": v(52.74, 15.33) * mm, "end": v(54.21, 15.36) * mm});
            skLineSegment(sketch, "E380", {"start": v(54.21, 15.36) * mm, "end": v(55.75, 15.33) * mm});
            skLineSegment(sketch, "E381", {"start": v(55.75, 15.33) * mm, "end": v(57.92, 15.33) * mm});
            skLineSegment(sketch, "E382", {"start": v(57.92, 15.33) * mm, "end": v(59.76, 15.41) * mm});
            skLineSegment(sketch, "E383", {"start": v(59.76, 15.41) * mm, "end": v(61.33, 15.36) * mm});
            skLineSegment(sketch, "E384", {"start": v(61.33, 15.36) * mm, "end": v(64.57, 15.41) * mm});
            skLineSegment(sketch, "E385", {"start": v(64.57, 15.41) * mm, "end": v(65.62, 15.73) * mm});
            skLineSegment(sketch, "E386", {"start": v(65.62, 15.73) * mm, "end": v(66.85, 15.62) * mm});
            skLineSegment(sketch, "E387", {"start": v(66.85, 15.62) * mm, "end": v(67.38, 15.62) * mm});
            skLineSegment(sketch, "E388", {"start": v(67.38, 15.62) * mm, "end": v(67.8, 15.67) * mm});
            skLineSegment(sketch, "E389", {"start": v(67.8, 15.67) * mm, "end": v(66.7, 14.24) * mm});
            skLineSegment(sketch, "E390", {"start": v(66.7, 14.24) * mm, "end": v(65.75, 12.5) * mm});
            skLineSegment(sketch, "E391", {"start": v(65.75, 12.5) * mm, "end": v(64.36, 10.6) * mm});
            skLineSegment(sketch, "E392", {"start": v(64.36, 10.6) * mm, "end": v(63.08, 9.44) * mm});
            skLineSegment(sketch, "E393", {"start": v(63.08, 9.44) * mm, "end": v(61.94, 8.13) * mm});
            skLineSegment(sketch, "E394", {"start": v(61.94, 8.13) * mm, "end": v(60.42, 6.76) * mm});
            skLineSegment(sketch, "E395", {"start": v(60.42, 6.76) * mm, "end": v(59.08, 5.54) * mm});
            skLineSegment(sketch, "E396", {"start": v(59.08, 5.54) * mm, "end": v(57.76, 4.74) * mm});
            skLineSegment(sketch, "E397", {"start": v(57.76, 4.74) * mm, "end": v(56.37, 3.93) * mm});
            skLineSegment(sketch, "E398", {"start": v(56.37, 3.93) * mm, "end": v(55.08, 3.17) * mm});
            skLineSegment(sketch, "E399", {"start": v(55.08, 3.17) * mm, "end": v(54.26, 2.85) * mm});
            skLineSegment(sketch, "E400", {"start": v(54.26, 2.85) * mm, "end": v(53.71, 2.85) * mm});
            skLineSegment(sketch, "E401", {"start": v(53.71, 2.85) * mm, "end": v(53.69, 4.72) * mm});
            skLineSegment(sketch, "E402", {"start": v(53.69, 4.72) * mm, "end": v(53.69, 6.19) * mm});
            skLineSegment(sketch, "E403", {"start": v(53.69, 6.19) * mm, "end": v(54.31, 6.76) * mm});
            skLineSegment(sketch, "E404", {"start": v(54.31, 6.76) * mm, "end": v(55.66, 7.3) * mm});
            skLineSegment(sketch, "E405", {"start": v(55.66, 7.3) * mm, "end": v(57.02, 8.16) * mm});
            skLineSegment(sketch, "E406", {"start": v(57.02, 8.16) * mm, "end": v(57.92, 9.26) * mm});
            skLineSegment(sketch, "E407", {"start": v(57.92, 9.26) * mm, "end": v(58.81, 10.52) * mm});
            skLineSegment(sketch, "E408", {"start": v(58.81, 10.52) * mm, "end": v(58.81, 11.18) * mm});
            skLineSegment(sketch, "E409", {"start": v(58.81, 11.18) * mm, "end": v(58.5, 11.51) * mm});
            skLineSegment(sketch, "E410", {"start": v(58.5, 11.51) * mm, "end": v(57.76, 12.15) * mm});
            skLineSegment(sketch, "E411", {"start": v(57.76, 12.15) * mm, "end": v(56.6, 12.42) * mm});
            skLineSegment(sketch, "E412", {"start": v(56.6, 12.42) * mm, "end": v(55, 12.5) * mm});
            skLineSegment(sketch, "E413", {"start": v(55, 12.5) * mm, "end": v(53.03, 12.31) * mm});
            skLineSegment(sketch, "E414", {"start": v(53.03, 12.31) * mm, "end": v(51.4, 11.81) * mm});
            skLineSegment(sketch, "E415", {"start": v(51.4, 11.81) * mm, "end": v(49.93, 11.29) * mm});
            skLineSegment(sketch, "E416", {"start": v(49.93, 11.29) * mm, "end": v(48.7, 10.31) * mm});
            skLineSegment(sketch, "E417", {"start": v(48.7, 10.31) * mm, "end": v(47.3, 9.2) * mm});
            skLineSegment(sketch, "E418", {"start": v(47.3, 9.2) * mm, "end": v(46.49, 8.26) * mm});
            skLineSegment(sketch, "E419", {"start": v(46.49, 8.26) * mm, "end": v(46.18, 7.19) * mm});
            skLineSegment(sketch, "E420", {"start": v(46.18, 7.19) * mm, "end": v(45.67, 6.24) * mm});
            skLineSegment(sketch, "E421", {"start": v(45.67, 6.24) * mm, "end": v(45.67, 5.35) * mm});
            skLineSegment(sketch, "E422", {"start": v(45.67, 5.35) * mm, "end": v(44.94, 4.93) * mm});
            skLineSegment(sketch, "E423", {"start": v(44.94, 4.93) * mm, "end": v(44.12, 4.74) * mm});
            skLineSegment(sketch, "E424", {"start": v(44.12, 4.74) * mm, "end": v(43.1, 4.53) * mm});
            skLineSegment(sketch, "E425", {"start": v(43.1, 4.53) * mm, "end": v(42.06, 4.5) * mm});
            skLineSegment(sketch, "E426", {"start": v(39.93, 3.12) * mm, "end": v(39.93, 1.88) * mm});
            skLineSegment(sketch, "E427", {"start": v(39.93, 1.88) * mm, "end": v(39.93, 0.77) * mm});
            skLineSegment(sketch, "E428", {"start": v(39.93, 0.77) * mm, "end": v(40.1, 0.5) * mm});
            skLineSegment(sketch, "E429", {"start": v(40.1, 0.5) * mm, "end": v(41.88, 0.69) * mm});
            skLineSegment(sketch, "E430", {"start": v(41.88, 0.69) * mm, "end": v(43.91, 0.9) * mm});
            skLineSegment(sketch, "E431", {"start": v(43.91, 0.9) * mm, "end": v(45.68, 1.17) * mm});
            skLineSegment(sketch, "E432", {"start": v(45.68, 1.17) * mm, "end": v(47.31, 1.44) * mm});
            skLineSegment(sketch, "E433", {"start": v(47.31, 1.44) * mm, "end": v(48.02, 1.8) * mm});
            skLineSegment(sketch, "E434", {"start": v(48.02, 1.8) * mm, "end": v(48.2, 2.76) * mm});
            skLineSegment(sketch, "E435", {"start": v(48.2, 2.76) * mm, "end": v(48.46, 4.22) * mm});
            skLineSegment(sketch, "E436", {"start": v(48.46, 4.22) * mm, "end": v(48.06, 4.88) * mm});
            skLineSegment(sketch, "E437", {"start": v(48.06, 4.88) * mm, "end": v(46.65, 4.22) * mm});
            skLineSegment(sketch, "E438", {"start": v(46.65, 4.22) * mm, "end": v(45.41, 4.04) * mm});
            skLineSegment(sketch, "E439", {"start": v(45.41, 4.04) * mm, "end": v(43.38, 3.7) * mm});
            skLineSegment(sketch, "E440", {"start": v(43.38, 3.7) * mm, "end": v(42.23, 3.56) * mm});
            skLineSegment(sketch, "E441", {"start": v(42.23, 3.56) * mm, "end": v(41.26, 3.38) * mm});
            skLineSegment(sketch, "E442", {"start": v(41.26, 3.38) * mm, "end": v(39.93, 3.12) * mm});
            skLineSegment(sketch, "E443", {"start": v(48.4, 8.45) * mm, "end": v(49.22, 9.2) * mm});
            skLineSegment(sketch, "E444", {"start": v(49.22, 9.2) * mm, "end": v(50.14, 9.65) * mm});
            skLineSegment(sketch, "E445", {"start": v(50.14, 9.65) * mm, "end": v(50.8, 10.08) * mm});
            skLineSegment(sketch, "E446", {"start": v(50.8, 10.08) * mm, "end": v(51.25, 9.82) * mm});
            skLineSegment(sketch, "E447", {"start": v(51.25, 9.82) * mm, "end": v(51.51, 9) * mm});
            skLineSegment(sketch, "E448", {"start": v(51.51, 9) * mm, "end": v(51.77, 8) * mm});
            skLineSegment(sketch, "E449", {"start": v(51.77, 8) * mm, "end": v(52.15, 6.74) * mm});
            skLineSegment(sketch, "E450", {"start": v(52.15, 6.74) * mm, "end": v(52.52, 4.91) * mm});
            skLineSegment(sketch, "E451", {"start": v(52.52, 4.91) * mm, "end": v(52.7, 3.24) * mm});
            skLineSegment(sketch, "E452", {"start": v(52.7, 3.24) * mm, "end": v(52.52, 1.64) * mm});
            skLineSegment(sketch, "E453", {"start": v(52.52, 1.64) * mm, "end": v(52.15, -0.33) * mm});
            skLineSegment(sketch, "E454", {"start": v(52.15, -0.33) * mm, "end": v(51.22, -1.96) * mm});
            skLineSegment(sketch, "E455", {"start": v(51.22, -1.96) * mm, "end": v(50.21, -3.11) * mm});
            skLineSegment(sketch, "E456", {"start": v(50.21, -3.11) * mm, "end": v(48.73, -4.49) * mm});
            skLineSegment(sketch, "E457", {"start": v(48.73, -4.49) * mm, "end": v(46.9, -5.42) * mm});
            skLineSegment(sketch, "E458", {"start": v(46.9, -5.42) * mm, "end": v(46.2, -5.53) * mm});
            skLineSegment(sketch, "E459", {"start": v(46.2, -5.53) * mm, "end": v(46.5, -4.56) * mm});
            skLineSegment(sketch, "E460", {"start": v(46.5, -4.56) * mm, "end": v(46.5, -3.15) * mm});
            skLineSegment(sketch, "E461", {"start": v(46.5, -3.15) * mm, "end": v(46.9, -2.26) * mm});
            skLineSegment(sketch, "E462", {"start": v(46.9, -2.26) * mm, "end": v(47.61, -2.22) * mm});
            skLineSegment(sketch, "E463", {"start": v(47.61, -2.22) * mm, "end": v(48.61, -0.55) * mm});
            skLineSegment(sketch, "E464", {"start": v(48.61, -0.55) * mm, "end": v(49.32, 0.6) * mm});
            skLineSegment(sketch, "E465", {"start": v(49.32, 0.6) * mm, "end": v(49.73, 2.61) * mm});
            skLineSegment(sketch, "E466", {"start": v(49.73, 2.61) * mm, "end": v(49.66, 3.91) * mm});
            skLineSegment(sketch, "E467", {"start": v(49.66, 3.91) * mm, "end": v(49.28, 5.96) * mm});
            skLineSegment(sketch, "E468", {"start": v(49.28, 5.96) * mm, "end": v(48.73, 7.6) * mm});
            skLineSegment(sketch, "E469", {"start": v(48.73, 7.6) * mm, "end": v(48.4, 8.45) * mm});
            skLineSegment(sketch, "E470", {"start": v(25.74, 4.5) * mm, "end": v(27, 3.12) * mm});
            skLineSegment(sketch, "E471", {"start": v(27, 3.12) * mm, "end": v(27.9, 2.13) * mm});
            skLineSegment(sketch, "E472", {"start": v(27.9, 2.13) * mm, "end": v(27.6, 0.48) * mm});
            skLineSegment(sketch, "E473", {"start": v(27.6, 0.48) * mm, "end": v(27.6, -2.27) * mm});
            skLineSegment(sketch, "E474", {"start": v(27.6, -2.27) * mm, "end": v(28.27, -4.13) * mm});
            skLineSegment(sketch, "E475", {"start": v(28.27, -4.13) * mm, "end": v(29.01, -6.28) * mm});
            skLineSegment(sketch, "E476", {"start": v(29.01, -6.28) * mm, "end": v(30.05, -8.14) * mm});
            skLineSegment(sketch, "E477", {"start": v(30.05, -8.14) * mm, "end": v(31.61, -9.18) * mm});
            skLineSegment(sketch, "E478", {"start": v(31.61, -9.18) * mm, "end": v(32.88, -10.07) * mm});
            skLineSegment(sketch, "E479", {"start": v(32.88, -10.07) * mm, "end": v(32.88, -11.41) * mm});
            skLineSegment(sketch, "E480", {"start": v(32.88, -11.41) * mm, "end": v(32.28, -12.67) * mm});
            skLineSegment(sketch, "E481", {"start": v(32.28, -12.67) * mm, "end": v(30.5, -12.08) * mm});
            skLineSegment(sketch, "E482", {"start": v(30.5, -12.08) * mm, "end": v(29.3, -10.74) * mm});
            skLineSegment(sketch, "E483", {"start": v(29.3, -10.74) * mm, "end": v(27.6, -9.25) * mm});
            skLineSegment(sketch, "E484", {"start": v(27.6, -9.25) * mm, "end": v(26.34, -7.4) * mm});
            skLineSegment(sketch, "E485", {"start": v(26.34, -7.4) * mm, "end": v(25.07, -4.72) * mm});
            skLineSegment(sketch, "E486", {"start": v(25.07, -4.72) * mm, "end": v(24.33, -2.2) * mm});
            skLineSegment(sketch, "E487", {"start": v(24.33, -2.2) * mm, "end": v(24.55, 0.11) * mm});
            skLineSegment(sketch, "E488", {"start": v(24.55, 0.11) * mm, "end": v(24.63, 2.2) * mm});
            skLineSegment(sketch, "E489", {"start": v(24.63, 2.2) * mm, "end": v(25.74, 4.5) * mm});
            skLineSegment(sketch, "E490", {"start": v(42.38, -1) * mm, "end": v(42.38, -2.53) * mm});
            skLineSegment(sketch, "E491", {"start": v(42.38, -2.53) * mm, "end": v(42.38, -4.09) * mm});
            skLineSegment(sketch, "E492", {"start": v(42.38, -4.09) * mm, "end": v(42.08, -5.87) * mm});
            skLineSegment(sketch, "E493", {"start": v(42.08, -5.87) * mm, "end": v(41.45, -7.17) * mm});
            skLineSegment(sketch, "E494", {"start": v(41.45, -7.17) * mm, "end": v(40.48, -8.7) * mm});
            skLineSegment(sketch, "E495", {"start": v(40.48, -8.7) * mm, "end": v(39.74, -9.51) * mm});
            skLineSegment(sketch, "E496", {"start": v(39.74, -9.51) * mm, "end": v(39.03, -10.22) * mm});
            skLineSegment(sketch, "E497", {"start": v(39.03, -10.22) * mm, "end": v(38.73, -10.6) * mm});
            skLineSegment(sketch, "E498", {"start": v(38.73, -10.6) * mm, "end": v(38.29, -12.08) * mm});
            skLineSegment(sketch, "E499", {"start": v(38.29, -12.08) * mm, "end": v(38.29, -13) * mm});
            skLineSegment(sketch, "E500", {"start": v(38.29, -13) * mm, "end": v(38.66, -13.38) * mm});
            skLineSegment(sketch, "E501", {"start": v(38.66, -13.38) * mm, "end": v(39.89, -12.93) * mm});
            skLineSegment(sketch, "E502", {"start": v(39.89, -12.93) * mm, "end": v(40.85, -12.67) * mm});
            skLineSegment(sketch, "E503", {"start": v(40.85, -12.67) * mm, "end": v(41.74, -11.63) * mm});
            skLineSegment(sketch, "E504", {"start": v(41.74, -11.63) * mm, "end": v(42.9, -10.44) * mm});
            skLineSegment(sketch, "E505", {"start": v(42.9, -10.44) * mm, "end": v(43.83, -9.03) * mm});
            skLineSegment(sketch, "E506", {"start": v(43.83, -9.03) * mm, "end": v(44.38, -7.58) * mm});
            skLineSegment(sketch, "E507", {"start": v(44.38, -7.58) * mm, "end": v(44.9, -6.28) * mm});
            skLineSegment(sketch, "E508", {"start": v(44.9, -6.28) * mm, "end": v(45.16, -4.57) * mm});
            skLineSegment(sketch, "E509", {"start": v(45.16, -4.57) * mm, "end": v(45.13, -3.27) * mm});
            skLineSegment(sketch, "E510", {"start": v(45.13, -3.27) * mm, "end": v(45.28, -1.45) * mm});
            skLineSegment(sketch, "E511", {"start": v(45.28, -1.45) * mm, "end": v(45.35, -0.19) * mm});
            skLineSegment(sketch, "E512", {"start": v(45.35, -0.19) * mm, "end": v(44.94, -0.11) * mm});
            skLineSegment(sketch, "E513", {"start": v(44.94, -0.11) * mm, "end": v(43.94, -0.3) * mm});
            skLineSegment(sketch, "E514", {"start": v(43.94, -0.3) * mm, "end": v(42.9, -0.37) * mm});
            skLineSegment(sketch, "E515", {"start": v(42.9, -0.37) * mm, "end": v(42.38, -0.67) * mm});
            skLineSegment(sketch, "E516", {"start": v(42.38, -0.67) * mm, "end": v(42.36, -1) * mm});
            skLineSegment(sketch, "E517", {"start": v(42.36, -1) * mm, "end": v(42.38, -1) * mm});
            skLineSegment(sketch, "E518", {"start": v(29.65, -4.12) * mm, "end": v(29.88, -4.79) * mm});
            skLineSegment(sketch, "E519", {"start": v(29.88, -4.79) * mm, "end": v(30.45, -6.46) * mm});
            skLineSegment(sketch, "E520", {"start": v(30.45, -6.46) * mm, "end": v(30.7, -6.9) * mm});
            skLineSegment(sketch, "E521", {"start": v(30.7, -6.9) * mm, "end": v(31.15, -6.98) * mm});
            skLineSegment(sketch, "E522", {"start": v(31.15, -6.98) * mm, "end": v(31.94, -6.83) * mm});
            skLineSegment(sketch, "E523", {"start": v(31.94, -6.83) * mm, "end": v(32.96, -6.33) * mm});
            skLineSegment(sketch, "E524", {"start": v(32.96, -6.33) * mm, "end": v(35.62, -5.72) * mm});
            skLineSegment(sketch, "E525", {"start": v(35.62, -5.72) * mm, "end": v(36.77, -5.57) * mm});
            skLineSegment(sketch, "E526", {"start": v(36.77, -5.57) * mm, "end": v(38.22, -5.72) * mm});
            skLineSegment(sketch, "E527", {"start": v(38.22, -5.72) * mm, "end": v(39.43, -5.6) * mm});
            skLineSegment(sketch, "E528", {"start": v(39.43, -5.6) * mm, "end": v(40.32, -5.72) * mm});
            skLineSegment(sketch, "E529", {"start": v(40.32, -5.72) * mm, "end": v(40.77, -5.57) * mm});
            skLineSegment(sketch, "E530", {"start": v(40.77, -5.57) * mm, "end": v(40.95, -4.51) * mm});
            skLineSegment(sketch, "E531", {"start": v(40.95, -4.51) * mm, "end": v(41.03, -3.57) * mm});
            skLineSegment(sketch, "E532", {"start": v(41.03, -3.57) * mm, "end": v(41.16, -2.04) * mm});
            skLineSegment(sketch, "E533", {"start": v(41.16, -2.04) * mm, "end": v(40.22, -1.97) * mm});
            skLineSegment(sketch, "E534", {"start": v(40.22, -1.97) * mm, "end": v(39.4, -2) * mm});
            skLineSegment(sketch, "E535", {"start": v(39.4, -2) * mm, "end": v(37.82, -2) * mm});
            skLineSegment(sketch, "E536", {"start": v(37.82, -2) * mm, "end": v(36.7, -2.15) * mm});
            skLineSegment(sketch, "E537", {"start": v(36.7, -2.15) * mm, "end": v(35.33, -2.18) * mm});
            skLineSegment(sketch, "E538", {"start": v(35.33, -2.18) * mm, "end": v(33.99, -2.44) * mm});
            skLineSegment(sketch, "E539", {"start": v(33.99, -2.44) * mm, "end": v(32.41, -2.75) * mm});
            skLineSegment(sketch, "E540", {"start": v(32.41, -2.75) * mm, "end": v(31.57, -3.17) * mm});
            skLineSegment(sketch, "E541", {"start": v(31.57, -3.17) * mm, "end": v(30.83, -3.54) * mm});
            skLineSegment(sketch, "E542", {"start": v(30.83, -3.54) * mm, "end": v(30.1, -3.86) * mm});
            skLineSegment(sketch, "E543", {"start": v(30.1, -3.86) * mm, "end": v(29.65, -4.12) * mm});
            skLineSegment(sketch, "E544", {"start": v(35.01, -7.15) * mm, "end": v(35.7, -7.15) * mm});
            skLineSegment(sketch, "E545", {"start": v(35.7, -7.15) * mm, "end": v(37.01, -6.53) * mm});
            skLineSegment(sketch, "E546", {"start": v(37.01, -6.53) * mm, "end": v(38.08, -6.72) * mm});
            skLineSegment(sketch, "E547", {"start": v(38.08, -6.72) * mm, "end": v(38.26, -7.47) * mm});
            skLineSegment(sketch, "E548", {"start": v(38.26, -7.47) * mm, "end": v(37.76, -9.28) * mm});
            skLineSegment(sketch, "E549", {"start": v(37.76, -9.28) * mm, "end": v(37.01, -11.72) * mm});
            skLineSegment(sketch, "E550", {"start": v(37.01, -11.72) * mm, "end": v(35.95, -15.15) * mm});
            skLineSegment(sketch, "E551", {"start": v(35.95, -15.15) * mm, "end": v(34.7, -17.03) * mm});
            skLineSegment(sketch, "E552", {"start": v(34.7, -17.03) * mm, "end": v(33.26, -19.72) * mm});
            skLineSegment(sketch, "E553", {"start": v(33.26, -19.72) * mm, "end": v(32.14, -21.9) * mm});
            skLineSegment(sketch, "E554", {"start": v(32.14, -21.9) * mm, "end": v(30.33, -23.97) * mm});
            skLineSegment(sketch, "E555", {"start": v(30.33, -23.97) * mm, "end": v(27.83, -26.84) * mm});
            skLineSegment(sketch, "E556", {"start": v(27.83, -26.84) * mm, "end": v(26.51, -28.28) * mm});
            skLineSegment(sketch, "E557", {"start": v(26.51, -28.28) * mm, "end": v(25.14, -29.4) * mm});
            skLineSegment(sketch, "E558", {"start": v(25.14, -29.4) * mm, "end": v(24.51, -30.03) * mm});
            skLineSegment(sketch, "E559", {"start": v(24.51, -30.03) * mm, "end": v(24.2, -29.65) * mm});
            skLineSegment(sketch, "E560", {"start": v(24.2, -29.65) * mm, "end": v(24.51, -25.28) * mm});
            skLineSegment(sketch, "E561", {"start": v(24.51, -25.28) * mm, "end": v(24.2, -22.53) * mm});
            skLineSegment(sketch, "E562", {"start": v(24.2, -22.53) * mm, "end": v(24.51, -17.72) * mm});
            skLineSegment(sketch, "E563", {"start": v(24.51, -17.72) * mm, "end": v(24.7, -15.84) * mm});
            skLineSegment(sketch, "E564", {"start": v(24.7, -15.84) * mm, "end": v(25.14, -13.97) * mm});
            skLineSegment(sketch, "E565", {"start": v(25.14, -13.97) * mm, "end": v(25.39, -12.1) * mm});
            skLineSegment(sketch, "E566", {"start": v(25.39, -12.1) * mm, "end": v(25.58, -10.22) * mm});
            skLineSegment(sketch, "E567", {"start": v(25.58, -10.22) * mm, "end": v(25.58, -9.1) * mm});
            skLineSegment(sketch, "E568", {"start": v(25.58, -9.1) * mm, "end": v(26.2, -9.72) * mm});
            skLineSegment(sketch, "E569", {"start": v(26.2, -9.72) * mm, "end": v(26.83, -10.65) * mm});
            skLineSegment(sketch, "E570", {"start": v(26.83, -10.65) * mm, "end": v(27.89, -11.47) * mm});
            skLineSegment(sketch, "E571", {"start": v(27.89, -11.47) * mm, "end": v(28.51, -11.9) * mm});
            skLineSegment(sketch, "E572", {"start": v(28.51, -11.9) * mm, "end": v(28.58, -12.22) * mm});
            skLineSegment(sketch, "E573", {"start": v(28.58, -12.22) * mm, "end": v(28.58, -13.4) * mm});
            skLineSegment(sketch, "E574", {"start": v(28.58, -13.4) * mm, "end": v(28.58, -15.15) * mm});
            skLineSegment(sketch, "E575", {"start": v(28.58, -15.15) * mm, "end": v(28.26, -16.1) * mm});
            skLineSegment(sketch, "E576", {"start": v(28.26, -16.1) * mm, "end": v(28.26, -17.15) * mm});
            skLineSegment(sketch, "E577", {"start": v(28.26, -17.15) * mm, "end": v(28.83, -18.9) * mm});
            skLineSegment(sketch, "E578", {"start": v(28.83, -18.9) * mm, "end": v(30.08, -18.97) * mm});
            skLineSegment(sketch, "E579", {"start": v(30.08, -18.97) * mm, "end": v(31.2, -18.03) * mm});
            skLineSegment(sketch, "E580", {"start": v(31.2, -18.03) * mm, "end": v(32.26, -16.9) * mm});
            skLineSegment(sketch, "E581", {"start": v(32.26, -16.9) * mm, "end": v(32.89, -14.9) * mm});
            skLineSegment(sketch, "E582", {"start": v(32.89, -14.9) * mm, "end": v(33.14, -14.03) * mm});
            skLineSegment(sketch, "E583", {"start": v(33.14, -14.03) * mm, "end": v(34.2, -12.15) * mm});
            skLineSegment(sketch, "E584", {"start": v(34.2, -12.15) * mm, "end": v(34.51, -10.28) * mm});
            skLineSegment(sketch, "E585", {"start": v(34.51, -10.28) * mm, "end": v(34.83, -8.34) * mm});
            skLineSegment(sketch, "E586", {"start": v(34.83, -8.34) * mm, "end": v(35.01, -7.15) * mm});
            skLineSegment(sketch, "E587", {"start": v(35.01, -7.15) * mm, "end": v(35.01, -7.15) * mm});
            skSolve(sketch);
        }
        {
            var Q0;
            Q0 = qSketchRegion(id + "F2", true);
            extrude(context, id + "F3", {"entities" : qUnion([Q0]), "depth" : 12 * mm});
        }
        {
            var Q0;
            Q0=makeQuery(id+"F3.opExtrude","SWEPT_BODY",BODY,{"disambiguationData":[OSD([sQuery(id+"F2.wireOp",EDGE,"E302"),sQuery(id+"F2.wireOp",EDGE,"E303"),sQuery(id+"F2.wireOp",EDGE,"E304"),sQuery(id+"F2.wireOp",EDGE,"E305"),sQuery(id+"F2.wireOp",EDGE,"E306"),sQuery(id+"F2.wireOp",EDGE,"E307"),sQuery(id+"F2.wireOp",EDGE,"E308"),sQuery(id+"F2.wireOp",EDGE,"E309"),sQuery(id+"F2.wireOp",EDGE,"E310"),sQuery(id+"F2.wireOp",EDGE,"E311"),sQuery(id+"F2.wireOp",EDGE,"E312"),sQuery(id+"F2.wireOp",EDGE,"E313"),sQuery(id+"F2.wireOp",EDGE,"E314"),sQuery(id+"F2.wireOp",EDGE,"E315"),sQuery(id+"F2.wireOp",EDGE,"E316"),sQuery(id+"F2.wireOp",EDGE,"E317"),sQuery(id+"F2.wireOp",EDGE,"E318"),sQuery(id+"F2.wireOp",EDGE,"E319"),sQuery(id+"F2.wireOp",EDGE,"E320"),sQuery(id+"F2.wireOp",EDGE,"E321"),sQuery(id+"F2.wireOp",EDGE,"E322"),sQuery(id+"F2.wireOp",EDGE,"E323"),sQuery(id+"F2.wireOp",EDGE,"E324"),sQuery(id+"F2.wireOp",EDGE,"E325"),sQuery(id+"F2.wireOp",EDGE,"E326"),sQuery(id+"F2.wireOp",EDGE,"E327"),sQuery(id+"F2.wireOp",EDGE,"E328"),sQuery(id+"F2.wireOp",EDGE,"E329"),sQuery(id+"F2.wireOp",EDGE,"E330"),sQuery(id+"F2.wireOp",EDGE,"E331"),sQuery(id+"F2.wireOp",EDGE,"E332"),sQuery(id+"F2.wireOp",EDGE,"E333"),sQuery(id+"F2.wireOp",EDGE,"E334"),sQuery(id+"F2.wireOp",EDGE,"E335"),sQuery(id+"F2.wireOp",EDGE,"E336"),sQuery(id+"F2.wireOp",EDGE,"E337"),sQuery(id+"F2.wireOp",EDGE,"E338"),sQuery(id+"F2.wireOp",EDGE,"E339"),sQuery(id+"F2.wireOp",EDGE,"E340"),sQuery(id+"F2.wireOp",EDGE,"E341"),sQuery(id+"F2.wireOp",EDGE,"E342"),sQuery(id+"F2.wireOp",EDGE,"E343"),sQuery(id+"F2.wireOp",EDGE,"E344"),sQuery(id+"F2.wireOp",EDGE,"E345"),sQuery(id+"F2.wireOp",EDGE,"E346"),sQuery(id+"F2.wireOp",EDGE,"E347"),sQuery(id+"F2.wireOp",EDGE,"E348"),sQuery(id+"F2.wireOp",EDGE,"E349"),sQuery(id+"F2.wireOp",EDGE,"E350"),sQuery(id+"F2.wireOp",EDGE,"E351"),sQuery(id+"F2.wireOp",EDGE,"E352"),sQuery(id+"F2.wireOp",EDGE,"E353"),sQuery(id+"F2.wireOp",EDGE,"E354"),sQuery(id+"F2.wireOp",EDGE,"E355"),sQuery(id+"F2.wireOp",EDGE,"E356"),sQuery(id+"F2.wireOp",EDGE,"E357"),sQuery(id+"F2.wireOp",EDGE,"E358"),sQuery(id+"F2.wireOp",EDGE,"E359"),sQuery(id+"F2.wireOp",EDGE,"E360"),sQuery(id+"F2.wireOp",EDGE,"E361"),sQuery(id+"F2.wireOp",EDGE,"E362"),sQuery(id+"F2.wireOp",EDGE,"E363"),sQuery(id+"F2.wireOp",EDGE,"E364"),sQuery(id+"F2.wireOp",EDGE,"E365"),sQuery(id+"F2.wireOp",EDGE,"E366"),sQuery(id+"F2.wireOp",EDGE,"E367"),sQuery(id+"F2.wireOp",EDGE,"E368"),sQuery(id+"F2.wireOp",EDGE,"E369"),sQuery(id+"F2.wireOp",EDGE,"E370"),sQuery(id+"F2.wireOp",EDGE,"E371"),sQuery(id+"F2.wireOp",EDGE,"E372"),sQuery(id+"F2.wireOp",EDGE,"E373"),sQuery(id+"F2.wireOp",EDGE,"E374"),sQuery(id+"F2.wireOp",EDGE,"E375"),sQuery(id+"F2.wireOp",EDGE,"E376"),sQuery(id+"F2.wireOp",EDGE,"E377"),sQuery(id+"F2.wireOp",EDGE,"E378"),sQuery(id+"F2.wireOp",EDGE,"E379"),sQuery(id+"F2.wireOp",EDGE,"E380"),sQuery(id+"F2.wireOp",EDGE,"E381"),sQuery(id+"F2.wireOp",EDGE,"E382"),sQuery(id+"F2.wireOp",EDGE,"E383"),sQuery(id+"F2.wireOp",EDGE,"E384"),sQuery(id+"F2.wireOp",EDGE,"E385"),sQuery(id+"F2.wireOp",EDGE,"E386"),sQuery(id+"F2.wireOp",EDGE,"E387"),sQuery(id+"F2.wireOp",EDGE,"E388"),sQuery(id+"F2.wireOp",EDGE,"E389"),sQuery(id+"F2.wireOp",EDGE,"E390"),sQuery(id+"F2.wireOp",EDGE,"E391"),sQuery(id+"F2.wireOp",EDGE,"E392"),sQuery(id+"F2.wireOp",EDGE,"E393"),sQuery(id+"F2.wireOp",EDGE,"E394"),sQuery(id+"F2.wireOp",EDGE,"E395"),sQuery(id+"F2.wireOp",EDGE,"E396"),sQuery(id+"F2.wireOp",EDGE,"E397"),sQuery(id+"F2.wireOp",EDGE,"E398"),sQuery(id+"F2.wireOp",EDGE,"E399"),sQuery(id+"F2.wireOp",EDGE,"E400"),sQuery(id+"F2.wireOp",EDGE,"E401"),sQuery(id+"F2.wireOp",EDGE,"E402"),sQuery(id+"F2.wireOp",EDGE,"E403"),sQuery(id+"F2.wireOp",EDGE,"E404"),sQuery(id+"F2.wireOp",EDGE,"E405"),sQuery(id+"F2.wireOp",EDGE,"E406"),sQuery(id+"F2.wireOp",EDGE,"E407"),sQuery(id+"F2.wireOp",EDGE,"E408"),sQuery(id+"F2.wireOp",EDGE,"E409"),sQuery(id+"F2.wireOp",EDGE,"E410"),sQuery(id+"F2.wireOp",EDGE,"E411"),sQuery(id+"F2.wireOp",EDGE,"E412"),sQuery(id+"F2.wireOp",EDGE,"E413"),sQuery(id+"F2.wireOp",EDGE,"E414"),sQuery(id+"F2.wireOp",EDGE,"E415"),sQuery(id+"F2.wireOp",EDGE,"E416"),sQuery(id+"F2.wireOp",EDGE,"E417"),sQuery(id+"F2.wireOp",EDGE,"E418"),sQuery(id+"F2.wireOp",EDGE,"E419"),sQuery(id+"F2.wireOp",EDGE,"E420"),sQuery(id+"F2.wireOp",EDGE,"E421"),sQuery(id+"F2.wireOp",EDGE,"E422"),sQuery(id+"F2.wireOp",EDGE,"E423"),sQuery(id+"F2.wireOp",EDGE,"E424"),sQuery(id+"F2.wireOp",EDGE,"E425"),sQuery(id+"F2.wireOp",EDGE,"E426"),sQuery(id+"F2.wireOp",EDGE,"E427"),sQuery(id+"F2.wireOp",EDGE,"E428"),sQuery(id+"F2.wireOp",EDGE,"E429"),sQuery(id+"F2.wireOp",EDGE,"E430"),sQuery(id+"F2.wireOp",EDGE,"E431"),sQuery(id+"F2.wireOp",EDGE,"E432"),sQuery(id+"F2.wireOp",EDGE,"E433"),sQuery(id+"F2.wireOp",EDGE,"E434"),sQuery(id+"F2.wireOp",EDGE,"E435"),sQuery(id+"F2.wireOp",EDGE,"E436"),sQuery(id+"F2.wireOp",EDGE,"E437"),sQuery(id+"F2.wireOp",EDGE,"E438"),sQuery(id+"F2.wireOp",EDGE,"E439"),sQuery(id+"F2.wireOp",EDGE,"E440"),sQuery(id+"F2.wireOp",EDGE,"E441"),sQuery(id+"F2.wireOp",EDGE,"E442"),sQuery(id+"F2.wireOp",EDGE,"E443"),sQuery(id+"F2.wireOp",EDGE,"E444"),sQuery(id+"F2.wireOp",EDGE,"E445"),sQuery(id+"F2.wireOp",EDGE,"E446"),sQuery(id+"F2.wireOp",EDGE,"E447"),sQuery(id+"F2.wireOp",EDGE,"E448"),sQuery(id+"F2.wireOp",EDGE,"E449"),sQuery(id+"F2.wireOp",EDGE,"E450"),sQuery(id+"F2.wireOp",EDGE,"E451"),sQuery(id+"F2.wireOp",EDGE,"E452"),sQuery(id+"F2.wireOp",EDGE,"E453"),sQuery(id+"F2.wireOp",EDGE,"E454"),sQuery(id+"F2.wireOp",EDGE,"E455"),sQuery(id+"F2.wireOp",EDGE,"E456"),sQuery(id+"F2.wireOp",EDGE,"E457"),sQuery(id+"F2.wireOp",EDGE,"E458"),sQuery(id+"F2.wireOp",EDGE,"E459"),sQuery(id+"F2.wireOp",EDGE,"E460"),sQuery(id+"F2.wireOp",EDGE,"E461"),sQuery(id+"F2.wireOp",EDGE,"E462"),sQuery(id+"F2.wireOp",EDGE,"E463"),sQuery(id+"F2.wireOp",EDGE,"E464"),sQuery(id+"F2.wireOp",EDGE,"E465"),sQuery(id+"F2.wireOp",EDGE,"E466"),sQuery(id+"F2.wireOp",EDGE,"E467"),sQuery(id+"F2.wireOp",EDGE,"E468"),sQuery(id+"F2.wireOp",EDGE,"E469"),sQuery(id+"F2.wireOp",EDGE,"E470"),sQuery(id+"F2.wireOp",EDGE,"E471"),sQuery(id+"F2.wireOp",EDGE,"E472"),sQuery(id+"F2.wireOp",EDGE,"E473"),sQuery(id+"F2.wireOp",EDGE,"E474"),sQuery(id+"F2.wireOp",EDGE,"E475"),sQuery(id+"F2.wireOp",EDGE,"E476"),sQuery(id+"F2.wireOp",EDGE,"E477"),sQuery(id+"F2.wireOp",EDGE,"E478"),sQuery(id+"F2.wireOp",EDGE,"E479"),sQuery(id+"F2.wireOp",EDGE,"E480"),sQuery(id+"F2.wireOp",EDGE,"E481"),sQuery(id+"F2.wireOp",EDGE,"E482"),sQuery(id+"F2.wireOp",EDGE,"E483"),sQuery(id+"F2.wireOp",EDGE,"E484"),sQuery(id+"F2.wireOp",EDGE,"E485"),sQuery(id+"F2.wireOp",EDGE,"E486"),sQuery(id+"F2.wireOp",EDGE,"E487"),sQuery(id+"F2.wireOp",EDGE,"E488"),sQuery(id+"F2.wireOp",EDGE,"E489"),sQuery(id+"F2.wireOp",EDGE,"E490"),sQuery(id+"F2.wireOp",EDGE,"E491"),sQuery(id+"F2.wireOp",EDGE,"E492"),sQuery(id+"F2.wireOp",EDGE,"E493"),sQuery(id+"F2.wireOp",EDGE,"E494"),sQuery(id+"F2.wireOp",EDGE,"E495"),sQuery(id+"F2.wireOp",EDGE,"E496"),sQuery(id+"F2.wireOp",EDGE,"E497"),sQuery(id+"F2.wireOp",EDGE,"E498"),sQuery(id+"F2.wireOp",EDGE,"E499"),sQuery(id+"F2.wireOp",EDGE,"E500"),sQuery(id+"F2.wireOp",EDGE,"E501"),sQuery(id+"F2.wireOp",EDGE,"E502"),sQuery(id+"F2.wireOp",EDGE,"E503"),sQuery(id+"F2.wireOp",EDGE,"E504"),sQuery(id+"F2.wireOp",EDGE,"E505"),sQuery(id+"F2.wireOp",EDGE,"E506"),sQuery(id+"F2.wireOp",EDGE,"E507"),sQuery(id+"F2.wireOp",EDGE,"E508"),sQuery(id+"F2.wireOp",EDGE,"E509"),sQuery(id+"F2.wireOp",EDGE,"E510"),sQuery(id+"F2.wireOp",EDGE,"E511"),sQuery(id+"F2.wireOp",EDGE,"E512"),sQuery(id+"F2.wireOp",EDGE,"E513"),sQuery(id+"F2.wireOp",EDGE,"E514"),sQuery(id+"F2.wireOp",EDGE,"E515"),sQuery(id+"F2.wireOp",EDGE,"E516"),sQuery(id+"F2.wireOp",EDGE,"E517"),sQuery(id+"F2.wireOp",EDGE,"E518"),sQuery(id+"F2.wireOp",EDGE,"E519"),sQuery(id+"F2.wireOp",EDGE,"E520"),sQuery(id+"F2.wireOp",EDGE,"E521"),sQuery(id+"F2.wireOp",EDGE,"E522"),sQuery(id+"F2.wireOp",EDGE,"E523"),sQuery(id+"F2.wireOp",EDGE,"E524"),sQuery(id+"F2.wireOp",EDGE,"E525"),sQuery(id+"F2.wireOp",EDGE,"E526"),sQuery(id+"F2.wireOp",EDGE,"E527"),sQuery(id+"F2.wireOp",EDGE,"E528"),sQuery(id+"F2.wireOp",EDGE,"E529"),sQuery(id+"F2.wireOp",EDGE,"E530"),sQuery(id+"F2.wireOp",EDGE,"E531"),sQuery(id+"F2.wireOp",EDGE,"E532"),sQuery(id+"F2.wireOp",EDGE,"E533"),sQuery(id+"F2.wireOp",EDGE,"E534"),sQuery(id+"F2.wireOp",EDGE,"E535"),sQuery(id+"F2.wireOp",EDGE,"E536"),sQuery(id+"F2.wireOp",EDGE,"E537"),sQuery(id+"F2.wireOp",EDGE,"E538"),sQuery(id+"F2.wireOp",EDGE,"E539"),sQuery(id+"F2.wireOp",EDGE,"E540"),sQuery(id+"F2.wireOp",EDGE,"E541"),sQuery(id+"F2.wireOp",EDGE,"E542"),sQuery(id+"F2.wireOp",EDGE,"E543"),sQuery(id+"F2.wireOp",EDGE,"E544"),sQuery(id+"F2.wireOp",EDGE,"E545"),sQuery(id+"F2.wireOp",EDGE,"E546"),sQuery(id+"F2.wireOp",EDGE,"E547"),sQuery(id+"F2.wireOp",EDGE,"E548"),sQuery(id+"F2.wireOp",EDGE,"E549"),sQuery(id+"F2.wireOp",EDGE,"E550"),sQuery(id+"F2.wireOp",EDGE,"E551"),sQuery(id+"F2.wireOp",EDGE,"E552"),sQuery(id+"F2.wireOp",EDGE,"E553"),sQuery(id+"F2.wireOp",EDGE,"E554"),sQuery(id+"F2.wireOp",EDGE,"E555"),sQuery(id+"F2.wireOp",EDGE,"E556"),sQuery(id+"F2.wireOp",EDGE,"E557"),sQuery(id+"F2.wireOp",EDGE,"E558"),sQuery(id+"F2.wireOp",EDGE,"E559"),sQuery(id+"F2.wireOp",EDGE,"E560"),sQuery(id+"F2.wireOp",EDGE,"E561"),sQuery(id+"F2.wireOp",EDGE,"E562"),sQuery(id+"F2.wireOp",EDGE,"E563"),sQuery(id+"F2.wireOp",EDGE,"E564"),sQuery(id+"F2.wireOp",EDGE,"E565"),sQuery(id+"F2.wireOp",EDGE,"E566"),sQuery(id+"F2.wireOp",EDGE,"E567"),sQuery(id+"F2.wireOp",EDGE,"E568"),sQuery(id+"F2.wireOp",EDGE,"E569"),sQuery(id+"F2.wireOp",EDGE,"E570"),sQuery(id+"F2.wireOp",EDGE,"E571"),sQuery(id+"F2.wireOp",EDGE,"E572"),sQuery(id+"F2.wireOp",EDGE,"E573"),sQuery(id+"F2.wireOp",EDGE,"E574"),sQuery(id+"F2.wireOp",EDGE,"E575"),sQuery(id+"F2.wireOp",EDGE,"E576"),sQuery(id+"F2.wireOp",EDGE,"E577"),sQuery(id+"F2.wireOp",EDGE,"E578"),sQuery(id+"F2.wireOp",EDGE,"E579"),sQuery(id+"F2.wireOp",EDGE,"E580"),sQuery(id+"F2.wireOp",EDGE,"E581"),sQuery(id+"F2.wireOp",EDGE,"E582"),sQuery(id+"F2.wireOp",EDGE,"E583"),sQuery(id+"F2.wireOp",EDGE,"E584"),sQuery(id+"F2.wireOp",EDGE,"E585"),sQuery(id+"F2.wireOp",EDGE,"E586"),sQuery(id+"F2.wireOp",EDGE,"E587")])]});
            var Q1;
            Q1=makeQuery(id+"F3.opExtrude","SWEPT_EDGE",EDGE,{"disambiguationData":[OSD([sQuery(id+"F2.wireOp",EDGE,"E311"),sQuery(id+"F2.wireOp",EDGE,"E312")])]});
            transform(context, id + "F4", {"entities" : qUnion([Q0]), "transformType" : TransformType.ROTATION, "transformAxis" : qUnion([Q1]), "angle" : 180 * degree, "makeCopy" : false});
        }
        {
            var Q0;
            Q0=makeQuery(id+"F3.opExtrude","SWEPT_BODY",BODY,{"disambiguationData":[OSD([sQuery(id+"F2.wireOp",EDGE,"E302"),sQuery(id+"F2.wireOp",EDGE,"E303"),sQuery(id+"F2.wireOp",EDGE,"E304"),sQuery(id+"F2.wireOp",EDGE,"E305"),sQuery(id+"F2.wireOp",EDGE,"E306"),sQuery(id+"F2.wireOp",EDGE,"E307"),sQuery(id+"F2.wireOp",EDGE,"E308"),sQuery(id+"F2.wireOp",EDGE,"E309"),sQuery(id+"F2.wireOp",EDGE,"E310"),sQuery(id+"F2.wireOp",EDGE,"E311"),sQuery(id+"F2.wireOp",EDGE,"E312"),sQuery(id+"F2.wireOp",EDGE,"E313"),sQuery(id+"F2.wireOp",EDGE,"E314"),sQuery(id+"F2.wireOp",EDGE,"E315"),sQuery(id+"F2.wireOp",EDGE,"E316"),sQuery(id+"F2.wireOp",EDGE,"E317"),sQuery(id+"F2.wireOp",EDGE,"E318"),sQuery(id+"F2.wireOp",EDGE,"E319"),sQuery(id+"F2.wireOp",EDGE,"E320"),sQuery(id+"F2.wireOp",EDGE,"E321"),sQuery(id+"F2.wireOp",EDGE,"E322"),sQuery(id+"F2.wireOp",EDGE,"E323"),sQuery(id+"F2.wireOp",EDGE,"E324"),sQuery(id+"F2.wireOp",EDGE,"E325"),sQuery(id+"F2.wireOp",EDGE,"E326"),sQuery(id+"F2.wireOp",EDGE,"E327"),sQuery(id+"F2.wireOp",EDGE,"E328"),sQuery(id+"F2.wireOp",EDGE,"E329"),sQuery(id+"F2.wireOp",EDGE,"E330"),sQuery(id+"F2.wireOp",EDGE,"E331"),sQuery(id+"F2.wireOp",EDGE,"E332"),sQuery(id+"F2.wireOp",EDGE,"E333"),sQuery(id+"F2.wireOp",EDGE,"E334"),sQuery(id+"F2.wireOp",EDGE,"E335"),sQuery(id+"F2.wireOp",EDGE,"E336"),sQuery(id+"F2.wireOp",EDGE,"E337"),sQuery(id+"F2.wireOp",EDGE,"E338"),sQuery(id+"F2.wireOp",EDGE,"E339"),sQuery(id+"F2.wireOp",EDGE,"E340"),sQuery(id+"F2.wireOp",EDGE,"E341"),sQuery(id+"F2.wireOp",EDGE,"E342"),sQuery(id+"F2.wireOp",EDGE,"E343"),sQuery(id+"F2.wireOp",EDGE,"E344"),sQuery(id+"F2.wireOp",EDGE,"E345"),sQuery(id+"F2.wireOp",EDGE,"E346"),sQuery(id+"F2.wireOp",EDGE,"E347"),sQuery(id+"F2.wireOp",EDGE,"E348"),sQuery(id+"F2.wireOp",EDGE,"E349"),sQuery(id+"F2.wireOp",EDGE,"E350"),sQuery(id+"F2.wireOp",EDGE,"E351"),sQuery(id+"F2.wireOp",EDGE,"E352"),sQuery(id+"F2.wireOp",EDGE,"E353"),sQuery(id+"F2.wireOp",EDGE,"E354"),sQuery(id+"F2.wireOp",EDGE,"E355"),sQuery(id+"F2.wireOp",EDGE,"E356"),sQuery(id+"F2.wireOp",EDGE,"E357"),sQuery(id+"F2.wireOp",EDGE,"E358"),sQuery(id+"F2.wireOp",EDGE,"E359"),sQuery(id+"F2.wireOp",EDGE,"E360"),sQuery(id+"F2.wireOp",EDGE,"E361"),sQuery(id+"F2.wireOp",EDGE,"E362"),sQuery(id+"F2.wireOp",EDGE,"E363"),sQuery(id+"F2.wireOp",EDGE,"E364"),sQuery(id+"F2.wireOp",EDGE,"E365"),sQuery(id+"F2.wireOp",EDGE,"E366"),sQuery(id+"F2.wireOp",EDGE,"E367"),sQuery(id+"F2.wireOp",EDGE,"E368"),sQuery(id+"F2.wireOp",EDGE,"E369"),sQuery(id+"F2.wireOp",EDGE,"E370"),sQuery(id+"F2.wireOp",EDGE,"E371"),sQuery(id+"F2.wireOp",EDGE,"E372"),sQuery(id+"F2.wireOp",EDGE,"E373"),sQuery(id+"F2.wireOp",EDGE,"E374"),sQuery(id+"F2.wireOp",EDGE,"E375"),sQuery(id+"F2.wireOp",EDGE,"E376"),sQuery(id+"F2.wireOp",EDGE,"E377"),sQuery(id+"F2.wireOp",EDGE,"E378"),sQuery(id+"F2.wireOp",EDGE,"E379"),sQuery(id+"F2.wireOp",EDGE,"E380"),sQuery(id+"F2.wireOp",EDGE,"E381"),sQuery(id+"F2.wireOp",EDGE,"E382"),sQuery(id+"F2.wireOp",EDGE,"E383"),sQuery(id+"F2.wireOp",EDGE,"E384"),sQuery(id+"F2.wireOp",EDGE,"E385"),sQuery(id+"F2.wireOp",EDGE,"E386"),sQuery(id+"F2.wireOp",EDGE,"E387"),sQuery(id+"F2.wireOp",EDGE,"E388"),sQuery(id+"F2.wireOp",EDGE,"E389"),sQuery(id+"F2.wireOp",EDGE,"E390"),sQuery(id+"F2.wireOp",EDGE,"E391"),sQuery(id+"F2.wireOp",EDGE,"E392"),sQuery(id+"F2.wireOp",EDGE,"E393"),sQuery(id+"F2.wireOp",EDGE,"E394"),sQuery(id+"F2.wireOp",EDGE,"E395"),sQuery(id+"F2.wireOp",EDGE,"E396"),sQuery(id+"F2.wireOp",EDGE,"E397"),sQuery(id+"F2.wireOp",EDGE,"E398"),sQuery(id+"F2.wireOp",EDGE,"E399"),sQuery(id+"F2.wireOp",EDGE,"E400"),sQuery(id+"F2.wireOp",EDGE,"E401"),sQuery(id+"F2.wireOp",EDGE,"E402"),sQuery(id+"F2.wireOp",EDGE,"E403"),sQuery(id+"F2.wireOp",EDGE,"E404"),sQuery(id+"F2.wireOp",EDGE,"E405"),sQuery(id+"F2.wireOp",EDGE,"E406"),sQuery(id+"F2.wireOp",EDGE,"E407"),sQuery(id+"F2.wireOp",EDGE,"E408"),sQuery(id+"F2.wireOp",EDGE,"E409"),sQuery(id+"F2.wireOp",EDGE,"E410"),sQuery(id+"F2.wireOp",EDGE,"E411"),sQuery(id+"F2.wireOp",EDGE,"E412"),sQuery(id+"F2.wireOp",EDGE,"E413"),sQuery(id+"F2.wireOp",EDGE,"E414"),sQuery(id+"F2.wireOp",EDGE,"E415"),sQuery(id+"F2.wireOp",EDGE,"E416"),sQuery(id+"F2.wireOp",EDGE,"E417"),sQuery(id+"F2.wireOp",EDGE,"E418"),sQuery(id+"F2.wireOp",EDGE,"E419"),sQuery(id+"F2.wireOp",EDGE,"E420"),sQuery(id+"F2.wireOp",EDGE,"E421"),sQuery(id+"F2.wireOp",EDGE,"E422"),sQuery(id+"F2.wireOp",EDGE,"E423"),sQuery(id+"F2.wireOp",EDGE,"E424"),sQuery(id+"F2.wireOp",EDGE,"E425"),sQuery(id+"F2.wireOp",EDGE,"E426"),sQuery(id+"F2.wireOp",EDGE,"E427"),sQuery(id+"F2.wireOp",EDGE,"E428"),sQuery(id+"F2.wireOp",EDGE,"E429"),sQuery(id+"F2.wireOp",EDGE,"E430"),sQuery(id+"F2.wireOp",EDGE,"E431"),sQuery(id+"F2.wireOp",EDGE,"E432"),sQuery(id+"F2.wireOp",EDGE,"E433"),sQuery(id+"F2.wireOp",EDGE,"E434"),sQuery(id+"F2.wireOp",EDGE,"E435"),sQuery(id+"F2.wireOp",EDGE,"E436"),sQuery(id+"F2.wireOp",EDGE,"E437"),sQuery(id+"F2.wireOp",EDGE,"E438"),sQuery(id+"F2.wireOp",EDGE,"E439"),sQuery(id+"F2.wireOp",EDGE,"E440"),sQuery(id+"F2.wireOp",EDGE,"E441"),sQuery(id+"F2.wireOp",EDGE,"E442"),sQuery(id+"F2.wireOp",EDGE,"E443"),sQuery(id+"F2.wireOp",EDGE,"E444"),sQuery(id+"F2.wireOp",EDGE,"E445"),sQuery(id+"F2.wireOp",EDGE,"E446"),sQuery(id+"F2.wireOp",EDGE,"E447"),sQuery(id+"F2.wireOp",EDGE,"E448"),sQuery(id+"F2.wireOp",EDGE,"E449"),sQuery(id+"F2.wireOp",EDGE,"E450"),sQuery(id+"F2.wireOp",EDGE,"E451"),sQuery(id+"F2.wireOp",EDGE,"E452"),sQuery(id+"F2.wireOp",EDGE,"E453"),sQuery(id+"F2.wireOp",EDGE,"E454"),sQuery(id+"F2.wireOp",EDGE,"E455"),sQuery(id+"F2.wireOp",EDGE,"E456"),sQuery(id+"F2.wireOp",EDGE,"E457"),sQuery(id+"F2.wireOp",EDGE,"E458"),sQuery(id+"F2.wireOp",EDGE,"E459"),sQuery(id+"F2.wireOp",EDGE,"E460"),sQuery(id+"F2.wireOp",EDGE,"E461"),sQuery(id+"F2.wireOp",EDGE,"E462"),sQuery(id+"F2.wireOp",EDGE,"E463"),sQuery(id+"F2.wireOp",EDGE,"E464"),sQuery(id+"F2.wireOp",EDGE,"E465"),sQuery(id+"F2.wireOp",EDGE,"E466"),sQuery(id+"F2.wireOp",EDGE,"E467"),sQuery(id+"F2.wireOp",EDGE,"E468"),sQuery(id+"F2.wireOp",EDGE,"E469"),sQuery(id+"F2.wireOp",EDGE,"E470"),sQuery(id+"F2.wireOp",EDGE,"E471"),sQuery(id+"F2.wireOp",EDGE,"E472"),sQuery(id+"F2.wireOp",EDGE,"E473"),sQuery(id+"F2.wireOp",EDGE,"E474"),sQuery(id+"F2.wireOp",EDGE,"E475"),sQuery(id+"F2.wireOp",EDGE,"E476"),sQuery(id+"F2.wireOp",EDGE,"E477"),sQuery(id+"F2.wireOp",EDGE,"E478"),sQuery(id+"F2.wireOp",EDGE,"E479"),sQuery(id+"F2.wireOp",EDGE,"E480"),sQuery(id+"F2.wireOp",EDGE,"E481"),sQuery(id+"F2.wireOp",EDGE,"E482"),sQuery(id+"F2.wireOp",EDGE,"E483"),sQuery(id+"F2.wireOp",EDGE,"E484"),sQuery(id+"F2.wireOp",EDGE,"E485"),sQuery(id+"F2.wireOp",EDGE,"E486"),sQuery(id+"F2.wireOp",EDGE,"E487"),sQuery(id+"F2.wireOp",EDGE,"E488"),sQuery(id+"F2.wireOp",EDGE,"E489"),sQuery(id+"F2.wireOp",EDGE,"E490"),sQuery(id+"F2.wireOp",EDGE,"E491"),sQuery(id+"F2.wireOp",EDGE,"E492"),sQuery(id+"F2.wireOp",EDGE,"E493"),sQuery(id+"F2.wireOp",EDGE,"E494"),sQuery(id+"F2.wireOp",EDGE,"E495"),sQuery(id+"F2.wireOp",EDGE,"E496"),sQuery(id+"F2.wireOp",EDGE,"E497"),sQuery(id+"F2.wireOp",EDGE,"E498"),sQuery(id+"F2.wireOp",EDGE,"E499"),sQuery(id+"F2.wireOp",EDGE,"E500"),sQuery(id+"F2.wireOp",EDGE,"E501"),sQuery(id+"F2.wireOp",EDGE,"E502"),sQuery(id+"F2.wireOp",EDGE,"E503"),sQuery(id+"F2.wireOp",EDGE,"E504"),sQuery(id+"F2.wireOp",EDGE,"E505"),sQuery(id+"F2.wireOp",EDGE,"E506"),sQuery(id+"F2.wireOp",EDGE,"E507"),sQuery(id+"F2.wireOp",EDGE,"E508"),sQuery(id+"F2.wireOp",EDGE,"E509"),sQuery(id+"F2.wireOp",EDGE,"E510"),sQuery(id+"F2.wireOp",EDGE,"E511"),sQuery(id+"F2.wireOp",EDGE,"E512"),sQuery(id+"F2.wireOp",EDGE,"E513"),sQuery(id+"F2.wireOp",EDGE,"E514"),sQuery(id+"F2.wireOp",EDGE,"E515"),sQuery(id+"F2.wireOp",EDGE,"E516"),sQuery(id+"F2.wireOp",EDGE,"E517"),sQuery(id+"F2.wireOp",EDGE,"E518"),sQuery(id+"F2.wireOp",EDGE,"E519"),sQuery(id+"F2.wireOp",EDGE,"E520"),sQuery(id+"F2.wireOp",EDGE,"E521"),sQuery(id+"F2.wireOp",EDGE,"E522"),sQuery(id+"F2.wireOp",EDGE,"E523"),sQuery(id+"F2.wireOp",EDGE,"E524"),sQuery(id+"F2.wireOp",EDGE,"E525"),sQuery(id+"F2.wireOp",EDGE,"E526"),sQuery(id+"F2.wireOp",EDGE,"E527"),sQuery(id+"F2.wireOp",EDGE,"E528"),sQuery(id+"F2.wireOp",EDGE,"E529"),sQuery(id+"F2.wireOp",EDGE,"E530"),sQuery(id+"F2.wireOp",EDGE,"E531"),sQuery(id+"F2.wireOp",EDGE,"E532"),sQuery(id+"F2.wireOp",EDGE,"E533"),sQuery(id+"F2.wireOp",EDGE,"E534"),sQuery(id+"F2.wireOp",EDGE,"E535"),sQuery(id+"F2.wireOp",EDGE,"E536"),sQuery(id+"F2.wireOp",EDGE,"E537"),sQuery(id+"F2.wireOp",EDGE,"E538"),sQuery(id+"F2.wireOp",EDGE,"E539"),sQuery(id+"F2.wireOp",EDGE,"E540"),sQuery(id+"F2.wireOp",EDGE,"E541"),sQuery(id+"F2.wireOp",EDGE,"E542"),sQuery(id+"F2.wireOp",EDGE,"E543"),sQuery(id+"F2.wireOp",EDGE,"E544"),sQuery(id+"F2.wireOp",EDGE,"E545"),sQuery(id+"F2.wireOp",EDGE,"E546"),sQuery(id+"F2.wireOp",EDGE,"E547"),sQuery(id+"F2.wireOp",EDGE,"E548"),sQuery(id+"F2.wireOp",EDGE,"E549"),sQuery(id+"F2.wireOp",EDGE,"E550"),sQuery(id+"F2.wireOp",EDGE,"E551"),sQuery(id+"F2.wireOp",EDGE,"E552"),sQuery(id+"F2.wireOp",EDGE,"E553"),sQuery(id+"F2.wireOp",EDGE,"E554"),sQuery(id+"F2.wireOp",EDGE,"E555"),sQuery(id+"F2.wireOp",EDGE,"E556"),sQuery(id+"F2.wireOp",EDGE,"E557"),sQuery(id+"F2.wireOp",EDGE,"E558"),sQuery(id+"F2.wireOp",EDGE,"E559"),sQuery(id+"F2.wireOp",EDGE,"E560"),sQuery(id+"F2.wireOp",EDGE,"E561"),sQuery(id+"F2.wireOp",EDGE,"E562"),sQuery(id+"F2.wireOp",EDGE,"E563"),sQuery(id+"F2.wireOp",EDGE,"E564"),sQuery(id+"F2.wireOp",EDGE,"E565"),sQuery(id+"F2.wireOp",EDGE,"E566"),sQuery(id+"F2.wireOp",EDGE,"E567"),sQuery(id+"F2.wireOp",EDGE,"E568"),sQuery(id+"F2.wireOp",EDGE,"E569"),sQuery(id+"F2.wireOp",EDGE,"E570"),sQuery(id+"F2.wireOp",EDGE,"E571"),sQuery(id+"F2.wireOp",EDGE,"E572"),sQuery(id+"F2.wireOp",EDGE,"E573"),sQuery(id+"F2.wireOp",EDGE,"E574"),sQuery(id+"F2.wireOp",EDGE,"E575"),sQuery(id+"F2.wireOp",EDGE,"E576"),sQuery(id+"F2.wireOp",EDGE,"E577"),sQuery(id+"F2.wireOp",EDGE,"E578"),sQuery(id+"F2.wireOp",EDGE,"E579"),sQuery(id+"F2.wireOp",EDGE,"E580"),sQuery(id+"F2.wireOp",EDGE,"E581"),sQuery(id+"F2.wireOp",EDGE,"E582"),sQuery(id+"F2.wireOp",EDGE,"E583"),sQuery(id+"F2.wireOp",EDGE,"E584"),sQuery(id+"F2.wireOp",EDGE,"E585"),sQuery(id+"F2.wireOp",EDGE,"E586"),sQuery(id+"F2.wireOp",EDGE,"E587")])]});
            transform(context, id + "F5", {"entities" : qUnion([Q0]), "transformType" : TransformType.TRANSLATION_3D, "dx" : 20 * mm, "dy" : 0 * mm, "dz" : -18 * mm, "makeCopy" : false});
        }
        {
            var Q0;
            Q0=makeQuery(id+"F1.opExtrude","SWEPT_BODY",BODY,{"disambiguationData":[OSD([sQuery(id+"F0.wireOp",EDGE,"E129"),sQuery(id+"F0.wireOp",EDGE,"E130"),sQuery(id+"F0.wireOp",EDGE,"E131"),sQuery(id+"F0.wireOp",EDGE,"E132"),sQuery(id+"F0.wireOp",EDGE,"E133"),sQuery(id+"F0.wireOp",EDGE,"E134"),sQuery(id+"F0.wireOp",EDGE,"E135"),sQuery(id+"F0.wireOp",EDGE,"E136"),sQuery(id+"F0.wireOp",EDGE,"E137"),sQuery(id+"F0.wireOp",EDGE,"E138"),sQuery(id+"F0.wireOp",EDGE,"E139"),sQuery(id+"F0.wireOp",EDGE,"E140"),sQuery(id+"F0.wireOp",EDGE,"E141"),sQuery(id+"F0.wireOp",EDGE,"E142"),sQuery(id+"F0.wireOp",EDGE,"E143"),sQuery(id+"F0.wireOp",EDGE,"E144"),sQuery(id+"F0.wireOp",EDGE,"E145"),sQuery(id+"F0.wireOp",EDGE,"E146"),sQuery(id+"F0.wireOp",EDGE,"E147"),sQuery(id+"F0.wireOp",EDGE,"E148"),sQuery(id+"F0.wireOp",EDGE,"E149"),sQuery(id+"F0.wireOp",EDGE,"E150"),sQuery(id+"F0.wireOp",EDGE,"E151"),sQuery(id+"F0.wireOp",EDGE,"E152"),sQuery(id+"F0.wireOp",EDGE,"E153"),sQuery(id+"F0.wireOp",EDGE,"E154"),sQuery(id+"F0.wireOp",EDGE,"E155"),sQuery(id+"F0.wireOp",EDGE,"E156"),sQuery(id+"F0.wireOp",EDGE,"E157"),sQuery(id+"F0.wireOp",EDGE,"E158"),sQuery(id+"F0.wireOp",EDGE,"E159"),sQuery(id+"F0.wireOp",EDGE,"E160"),sQuery(id+"F0.wireOp",EDGE,"E161"),sQuery(id+"F0.wireOp",EDGE,"E162"),sQuery(id+"F0.wireOp",EDGE,"E163"),sQuery(id+"F0.wireOp",EDGE,"E164"),sQuery(id+"F0.wireOp",EDGE,"E165"),sQuery(id+"F0.wireOp",EDGE,"E166"),sQuery(id+"F0.wireOp",EDGE,"E167"),sQuery(id+"F0.wireOp",EDGE,"E168"),sQuery(id+"F0.wireOp",EDGE,"E169"),sQuery(id+"F0.wireOp",EDGE,"E170"),sQuery(id+"F0.wireOp",EDGE,"E171"),sQuery(id+"F0.wireOp",EDGE,"E172"),sQuery(id+"F0.wireOp",EDGE,"E173"),sQuery(id+"F0.wireOp",EDGE,"E174"),sQuery(id+"F0.wireOp",EDGE,"E175"),sQuery(id+"F0.wireOp",EDGE,"E176"),sQuery(id+"F0.wireOp",EDGE,"E177"),sQuery(id+"F0.wireOp",EDGE,"E178"),sQuery(id+"F0.wireOp",EDGE,"E179"),sQuery(id+"F0.wireOp",EDGE,"E180"),sQuery(id+"F0.wireOp",EDGE,"E181"),sQuery(id+"F0.wireOp",EDGE,"E182"),sQuery(id+"F0.wireOp",EDGE,"E183"),sQuery(id+"F0.wireOp",EDGE,"E184"),sQuery(id+"F0.wireOp",EDGE,"E185"),sQuery(id+"F0.wireOp",EDGE,"E186"),sQuery(id+"F0.wireOp",EDGE,"E187"),sQuery(id+"F0.wireOp",EDGE,"E188"),sQuery(id+"F0.wireOp",EDGE,"E189"),sQuery(id+"F0.wireOp",EDGE,"E190"),sQuery(id+"F0.wireOp",EDGE,"E191"),sQuery(id+"F0.wireOp",EDGE,"E192"),sQuery(id+"F0.wireOp",EDGE,"E193"),sQuery(id+"F0.wireOp",EDGE,"E194"),sQuery(id+"F0.wireOp",EDGE,"E195"),sQuery(id+"F0.wireOp",EDGE,"E196"),sQuery(id+"F0.wireOp",EDGE,"E197"),sQuery(id+"F0.wireOp",EDGE,"E198"),sQuery(id+"F0.wireOp",EDGE,"E199"),sQuery(id+"F0.wireOp",EDGE,"E200"),sQuery(id+"F0.wireOp",EDGE,"E201"),sQuery(id+"F0.wireOp",EDGE,"E202"),sQuery(id+"F0.wireOp",EDGE,"E203"),sQuery(id+"F0.wireOp",EDGE,"E204"),sQuery(id+"F0.wireOp",EDGE,"E205"),sQuery(id+"F0.wireOp",EDGE,"E206"),sQuery(id+"F0.wireOp",EDGE,"E207"),sQuery(id+"F0.wireOp",EDGE,"E208"),sQuery(id+"F0.wireOp",EDGE,"E209"),sQuery(id+"F0.wireOp",EDGE,"E210"),sQuery(id+"F0.wireOp",EDGE,"E211"),sQuery(id+"F0.wireOp",EDGE,"E212"),sQuery(id+"F0.wireOp",EDGE,"E213"),sQuery(id+"F0.wireOp",EDGE,"E214"),sQuery(id+"F0.wireOp",EDGE,"E215"),sQuery(id+"F0.wireOp",EDGE,"E216"),sQuery(id+"F0.wireOp",EDGE,"E217"),sQuery(id+"F0.wireOp",EDGE,"E218"),sQuery(id+"F0.wireOp",EDGE,"E219"),sQuery(id+"F0.wireOp",EDGE,"E220"),sQuery(id+"F0.wireOp",EDGE,"E221"),sQuery(id+"F0.wireOp",EDGE,"E222"),sQuery(id+"F0.wireOp",EDGE,"E223"),sQuery(id+"F0.wireOp",EDGE,"E224"),sQuery(id+"F0.wireOp",EDGE,"E225"),sQuery(id+"F0.wireOp",EDGE,"E226"),sQuery(id+"F0.wireOp",EDGE,"E227"),sQuery(id+"F0.wireOp",EDGE,"E228"),sQuery(id+"F0.wireOp",EDGE,"E229"),sQuery(id+"F0.wireOp",EDGE,"E230"),sQuery(id+"F0.wireOp",EDGE,"E231"),sQuery(id+"F0.wireOp",EDGE,"E232"),sQuery(id+"F0.wireOp",EDGE,"E233"),sQuery(id+"F0.wireOp",EDGE,"E234"),sQuery(id+"F0.wireOp",EDGE,"E235"),sQuery(id+"F0.wireOp",EDGE,"E236"),sQuery(id+"F0.wireOp",EDGE,"E237"),sQuery(id+"F0.wireOp",EDGE,"E238"),sQuery(id+"F0.wireOp",EDGE,"E239"),sQuery(id+"F0.wireOp",EDGE,"E240"),sQuery(id+"F0.wireOp",EDGE,"E241"),sQuery(id+"F0.wireOp",EDGE,"E242"),sQuery(id+"F0.wireOp",EDGE,"E243"),sQuery(id+"F0.wireOp",EDGE,"E244"),sQuery(id+"F0.wireOp",EDGE,"E245"),sQuery(id+"F0.wireOp",EDGE,"E246"),sQuery(id+"F0.wireOp",EDGE,"E247"),sQuery(id+"F0.wireOp",EDGE,"E248"),sQuery(id+"F0.wireOp",EDGE,"E249"),sQuery(id+"F0.wireOp",EDGE,"E250"),sQuery(id+"F0.wireOp",EDGE,"E251"),sQuery(id+"F0.wireOp",EDGE,"E252"),sQuery(id+"F0.wireOp",EDGE,"E253"),sQuery(id+"F0.wireOp",EDGE,"E254"),sQuery(id+"F0.wireOp",EDGE,"E255"),sQuery(id+"F0.wireOp",EDGE,"E256"),sQuery(id+"F0.wireOp",EDGE,"E257"),sQuery(id+"F0.wireOp",EDGE,"E258"),sQuery(id+"F0.wireOp",EDGE,"E259"),sQuery(id+"F0.wireOp",EDGE,"E260"),sQuery(id+"F0.wireOp",EDGE,"E261"),sQuery(id+"F0.wireOp",EDGE,"E262"),sQuery(id+"F0.wireOp",EDGE,"E263"),sQuery(id+"F0.wireOp",EDGE,"E264"),sQuery(id+"F0.wireOp",EDGE,"E265"),sQuery(id+"F0.wireOp",EDGE,"E266"),sQuery(id+"F0.wireOp",EDGE,"E267"),sQuery(id+"F0.wireOp",EDGE,"E268"),sQuery(id+"F0.wireOp",EDGE,"E269"),sQuery(id+"F0.wireOp",EDGE,"E270"),sQuery(id+"F0.wireOp",EDGE,"E271"),sQuery(id+"F0.wireOp",EDGE,"E272"),sQuery(id+"F0.wireOp",EDGE,"E273"),sQuery(id+"F0.wireOp",EDGE,"E274"),sQuery(id+"F0.wireOp",EDGE,"E275"),sQuery(id+"F0.wireOp",EDGE,"E276"),sQuery(id+"F0.wireOp",EDGE,"E277"),sQuery(id+"F0.wireOp",EDGE,"E278"),sQuery(id+"F0.wireOp",EDGE,"E279"),sQuery(id+"F0.wireOp",EDGE,"E280"),sQuery(id+"F0.wireOp",EDGE,"E281"),sQuery(id+"F0.wireOp",EDGE,"E282"),sQuery(id+"F0.wireOp",EDGE,"E283"),sQuery(id+"F0.wireOp",EDGE,"E284"),sQuery(id+"F0.wireOp",EDGE,"E285"),sQuery(id+"F0.wireOp",EDGE,"E286"),sQuery(id+"F0.wireOp",EDGE,"E287"),sQuery(id+"F0.wireOp",EDGE,"E288"),sQuery(id+"F0.wireOp",EDGE,"E289"),sQuery(id+"F0.wireOp",EDGE,"E290"),sQuery(id+"F0.wireOp",EDGE,"E291"),sQuery(id+"F0.wireOp",EDGE,"E292"),sQuery(id+"F0.wireOp",EDGE,"E293"),sQuery(id+"F0.wireOp",EDGE,"E294"),sQuery(id+"F0.wireOp",EDGE,"E295"),sQuery(id+"F0.wireOp",EDGE,"E296"),sQuery(id+"F0.wireOp",EDGE,"E297"),sQuery(id+"F0.wireOp",EDGE,"E298"),sQuery(id+"F0.wireOp",EDGE,"E299"),sQuery(id+"F0.wireOp",EDGE,"E300"),sQuery(id+"F0.wireOp",EDGE,"E301")])]});
            transform(context, id + "F6", {"entities" : qUnion([Q0]), "transformType" : TransformType.TRANSLATION_3D, "dx" : 2 * mm, "dy" : 0 * mm, "dz" : 0 * mm, "makeCopy" : false});
        }
        {
            var Q0;
            Q0=makeQuery(id+"F1.opExtrude","SWEPT_BODY",BODY,{"disambiguationData":[OSD([sQuery(id+"F0.wireOp",EDGE,"E129"),sQuery(id+"F0.wireOp",EDGE,"E130"),sQuery(id+"F0.wireOp",EDGE,"E131"),sQuery(id+"F0.wireOp",EDGE,"E132"),sQuery(id+"F0.wireOp",EDGE,"E133"),sQuery(id+"F0.wireOp",EDGE,"E134"),sQuery(id+"F0.wireOp",EDGE,"E135"),sQuery(id+"F0.wireOp",EDGE,"E136"),sQuery(id+"F0.wireOp",EDGE,"E137"),sQuery(id+"F0.wireOp",EDGE,"E138"),sQuery(id+"F0.wireOp",EDGE,"E139"),sQuery(id+"F0.wireOp",EDGE,"E140"),sQuery(id+"F0.wireOp",EDGE,"E141"),sQuery(id+"F0.wireOp",EDGE,"E142"),sQuery(id+"F0.wireOp",EDGE,"E143"),sQuery(id+"F0.wireOp",EDGE,"E144"),sQuery(id+"F0.wireOp",EDGE,"E145"),sQuery(id+"F0.wireOp",EDGE,"E146"),sQuery(id+"F0.wireOp",EDGE,"E147"),sQuery(id+"F0.wireOp",EDGE,"E148"),sQuery(id+"F0.wireOp",EDGE,"E149"),sQuery(id+"F0.wireOp",EDGE,"E150"),sQuery(id+"F0.wireOp",EDGE,"E151"),sQuery(id+"F0.wireOp",EDGE,"E152"),sQuery(id+"F0.wireOp",EDGE,"E153"),sQuery(id+"F0.wireOp",EDGE,"E154"),sQuery(id+"F0.wireOp",EDGE,"E155"),sQuery(id+"F0.wireOp",EDGE,"E156"),sQuery(id+"F0.wireOp",EDGE,"E157"),sQuery(id+"F0.wireOp",EDGE,"E158"),sQuery(id+"F0.wireOp",EDGE,"E159"),sQuery(id+"F0.wireOp",EDGE,"E160"),sQuery(id+"F0.wireOp",EDGE,"E161"),sQuery(id+"F0.wireOp",EDGE,"E162"),sQuery(id+"F0.wireOp",EDGE,"E163"),sQuery(id+"F0.wireOp",EDGE,"E164"),sQuery(id+"F0.wireOp",EDGE,"E165"),sQuery(id+"F0.wireOp",EDGE,"E166"),sQuery(id+"F0.wireOp",EDGE,"E167"),sQuery(id+"F0.wireOp",EDGE,"E168"),sQuery(id+"F0.wireOp",EDGE,"E169"),sQuery(id+"F0.wireOp",EDGE,"E170"),sQuery(id+"F0.wireOp",EDGE,"E171"),sQuery(id+"F0.wireOp",EDGE,"E172"),sQuery(id+"F0.wireOp",EDGE,"E173"),sQuery(id+"F0.wireOp",EDGE,"E174"),sQuery(id+"F0.wireOp",EDGE,"E175"),sQuery(id+"F0.wireOp",EDGE,"E176"),sQuery(id+"F0.wireOp",EDGE,"E177"),sQuery(id+"F0.wireOp",EDGE,"E178"),sQuery(id+"F0.wireOp",EDGE,"E179"),sQuery(id+"F0.wireOp",EDGE,"E180"),sQuery(id+"F0.wireOp",EDGE,"E181"),sQuery(id+"F0.wireOp",EDGE,"E182"),sQuery(id+"F0.wireOp",EDGE,"E183"),sQuery(id+"F0.wireOp",EDGE,"E184"),sQuery(id+"F0.wireOp",EDGE,"E185"),sQuery(id+"F0.wireOp",EDGE,"E186"),sQuery(id+"F0.wireOp",EDGE,"E187"),sQuery(id+"F0.wireOp",EDGE,"E188"),sQuery(id+"F0.wireOp",EDGE,"E189"),sQuery(id+"F0.wireOp",EDGE,"E190"),sQuery(id+"F0.wireOp",EDGE,"E191"),sQuery(id+"F0.wireOp",EDGE,"E192"),sQuery(id+"F0.wireOp",EDGE,"E193"),sQuery(id+"F0.wireOp",EDGE,"E194"),sQuery(id+"F0.wireOp",EDGE,"E195"),sQuery(id+"F0.wireOp",EDGE,"E196"),sQuery(id+"F0.wireOp",EDGE,"E197"),sQuery(id+"F0.wireOp",EDGE,"E198"),sQuery(id+"F0.wireOp",EDGE,"E199"),sQuery(id+"F0.wireOp",EDGE,"E200"),sQuery(id+"F0.wireOp",EDGE,"E201"),sQuery(id+"F0.wireOp",EDGE,"E202"),sQuery(id+"F0.wireOp",EDGE,"E203"),sQuery(id+"F0.wireOp",EDGE,"E204"),sQuery(id+"F0.wireOp",EDGE,"E205"),sQuery(id+"F0.wireOp",EDGE,"E206"),sQuery(id+"F0.wireOp",EDGE,"E207"),sQuery(id+"F0.wireOp",EDGE,"E208"),sQuery(id+"F0.wireOp",EDGE,"E209"),sQuery(id+"F0.wireOp",EDGE,"E210"),sQuery(id+"F0.wireOp",EDGE,"E211"),sQuery(id+"F0.wireOp",EDGE,"E212"),sQuery(id+"F0.wireOp",EDGE,"E213"),sQuery(id+"F0.wireOp",EDGE,"E214"),sQuery(id+"F0.wireOp",EDGE,"E215"),sQuery(id+"F0.wireOp",EDGE,"E216"),sQuery(id+"F0.wireOp",EDGE,"E217"),sQuery(id+"F0.wireOp",EDGE,"E218"),sQuery(id+"F0.wireOp",EDGE,"E219"),sQuery(id+"F0.wireOp",EDGE,"E220"),sQuery(id+"F0.wireOp",EDGE,"E221"),sQuery(id+"F0.wireOp",EDGE,"E222"),sQuery(id+"F0.wireOp",EDGE,"E223"),sQuery(id+"F0.wireOp",EDGE,"E224"),sQuery(id+"F0.wireOp",EDGE,"E225"),sQuery(id+"F0.wireOp",EDGE,"E226"),sQuery(id+"F0.wireOp",EDGE,"E227"),sQuery(id+"F0.wireOp",EDGE,"E228"),sQuery(id+"F0.wireOp",EDGE,"E229"),sQuery(id+"F0.wireOp",EDGE,"E230"),sQuery(id+"F0.wireOp",EDGE,"E231"),sQuery(id+"F0.wireOp",EDGE,"E232"),sQuery(id+"F0.wireOp",EDGE,"E233"),sQuery(id+"F0.wireOp",EDGE,"E234"),sQuery(id+"F0.wireOp",EDGE,"E235"),sQuery(id+"F0.wireOp",EDGE,"E236"),sQuery(id+"F0.wireOp",EDGE,"E237"),sQuery(id+"F0.wireOp",EDGE,"E238"),sQuery(id+"F0.wireOp",EDGE,"E239"),sQuery(id+"F0.wireOp",EDGE,"E240"),sQuery(id+"F0.wireOp",EDGE,"E241"),sQuery(id+"F0.wireOp",EDGE,"E242"),sQuery(id+"F0.wireOp",EDGE,"E243"),sQuery(id+"F0.wireOp",EDGE,"E244"),sQuery(id+"F0.wireOp",EDGE,"E245"),sQuery(id+"F0.wireOp",EDGE,"E246"),sQuery(id+"F0.wireOp",EDGE,"E247"),sQuery(id+"F0.wireOp",EDGE,"E248"),sQuery(id+"F0.wireOp",EDGE,"E249"),sQuery(id+"F0.wireOp",EDGE,"E250"),sQuery(id+"F0.wireOp",EDGE,"E251"),sQuery(id+"F0.wireOp",EDGE,"E252"),sQuery(id+"F0.wireOp",EDGE,"E253"),sQuery(id+"F0.wireOp",EDGE,"E254"),sQuery(id+"F0.wireOp",EDGE,"E255"),sQuery(id+"F0.wireOp",EDGE,"E256"),sQuery(id+"F0.wireOp",EDGE,"E257"),sQuery(id+"F0.wireOp",EDGE,"E258"),sQuery(id+"F0.wireOp",EDGE,"E259"),sQuery(id+"F0.wireOp",EDGE,"E260"),sQuery(id+"F0.wireOp",EDGE,"E261"),sQuery(id+"F0.wireOp",EDGE,"E262"),sQuery(id+"F0.wireOp",EDGE,"E263"),sQuery(id+"F0.wireOp",EDGE,"E264"),sQuery(id+"F0.wireOp",EDGE,"E265"),sQuery(id+"F0.wireOp",EDGE,"E266"),sQuery(id+"F0.wireOp",EDGE,"E267"),sQuery(id+"F0.wireOp",EDGE,"E268"),sQuery(id+"F0.wireOp",EDGE,"E269"),sQuery(id+"F0.wireOp",EDGE,"E270"),sQuery(id+"F0.wireOp",EDGE,"E271"),sQuery(id+"F0.wireOp",EDGE,"E272"),sQuery(id+"F0.wireOp",EDGE,"E273"),sQuery(id+"F0.wireOp",EDGE,"E274"),sQuery(id+"F0.wireOp",EDGE,"E275"),sQuery(id+"F0.wireOp",EDGE,"E276"),sQuery(id+"F0.wireOp",EDGE,"E277"),sQuery(id+"F0.wireOp",EDGE,"E278"),sQuery(id+"F0.wireOp",EDGE,"E279"),sQuery(id+"F0.wireOp",EDGE,"E280"),sQuery(id+"F0.wireOp",EDGE,"E281"),sQuery(id+"F0.wireOp",EDGE,"E282"),sQuery(id+"F0.wireOp",EDGE,"E283"),sQuery(id+"F0.wireOp",EDGE,"E284"),sQuery(id+"F0.wireOp",EDGE,"E285"),sQuery(id+"F0.wireOp",EDGE,"E286"),sQuery(id+"F0.wireOp",EDGE,"E287"),sQuery(id+"F0.wireOp",EDGE,"E288"),sQuery(id+"F0.wireOp",EDGE,"E289"),sQuery(id+"F0.wireOp",EDGE,"E290"),sQuery(id+"F0.wireOp",EDGE,"E291"),sQuery(id+"F0.wireOp",EDGE,"E292"),sQuery(id+"F0.wireOp",EDGE,"E293"),sQuery(id+"F0.wireOp",EDGE,"E294"),sQuery(id+"F0.wireOp",EDGE,"E295"),sQuery(id+"F0.wireOp",EDGE,"E296"),sQuery(id+"F0.wireOp",EDGE,"E297"),sQuery(id+"F0.wireOp",EDGE,"E298"),sQuery(id+"F0.wireOp",EDGE,"E299"),sQuery(id+"F0.wireOp",EDGE,"E300"),sQuery(id+"F0.wireOp",EDGE,"E301")])]});
            transform(context, id + "F7", {"entities" : qUnion([Q0]), "transformType" : TransformType.TRANSLATION_3D, "dx" : 0 * mm, "dy" : 0 * mm, "dz" : -15 * mm, "makeCopy" : false});
        }
        {
            var Q0;
            Q0=qCreatedBy(makeId("Front.planeOp"),FACE);
            var sketch = newSketch(context, id + "F8", { "sketchPlane" : qUnion([Q0])});
            skLineSegment(sketch, "E588", {"start": v(22.99, 24.49) * mm, "end": v(22.99, 25.6) * mm});
            skLineSegment(sketch, "E589", {"start": v(22.99, 25.6) * mm, "end": v(24.1, 26.01) * mm});
            skLineSegment(sketch, "E590", {"start": v(24.1, 26.01) * mm, "end": v(25.83, 26.64) * mm});
            skLineSegment(sketch, "E591", {"start": v(25.83, 26.64) * mm, "end": v(26.3, 27.12) * mm});
            skLineSegment(sketch, "E592", {"start": v(26.3, 27.12) * mm, "end": v(29.8, 23.62) * mm});
            skLineSegment(sketch, "E593", {"start": v(29.8, 23.62) * mm, "end": v(31.4, 21.65) * mm});
            skLineSegment(sketch, "E594", {"start": v(31.4, 21.65) * mm, "end": v(33.03, 19.13) * mm});
            skLineSegment(sketch, "E595", {"start": v(33.03, 19.13) * mm, "end": v(33.82, 16.76) * mm});
            skLineSegment(sketch, "E596", {"start": v(33.82, 16.76) * mm, "end": v(34.34, 14.77) * mm});
            skLineSegment(sketch, "E597", {"start": v(34.87, 10.46) * mm, "end": v(34.87, 8.14) * mm});
            skLineSegment(sketch, "E598", {"start": v(34.87, 8.14) * mm, "end": v(34.34, 5.62) * mm});
            skLineSegment(sketch, "E599", {"start": v(34.34, 5.62) * mm, "end": v(33.3, 3.73) * mm});
            skLineSegment(sketch, "E600", {"start": v(33.3, 3.73) * mm, "end": v(32.08, 2.57) * mm});
            skLineSegment(sketch, "E601", {"start": v(32.08, 2.57) * mm, "end": v(30.24, 1.26) * mm});
            skLineSegment(sketch, "E602", {"start": v(30.24, 1.26) * mm, "end": v(28.4, 0.58) * mm});
            skLineSegment(sketch, "E603", {"start": v(24.57, 0.58) * mm, "end": v(23.57, 1.63) * mm});
            skLineSegment(sketch, "E604", {"start": v(23.57, 1.63) * mm, "end": v(22.94, 3.78) * mm});
            skLineSegment(sketch, "E605", {"start": v(22.94, 3.78) * mm, "end": v(22.62, 5.78) * mm});
            skLineSegment(sketch, "E606", {"start": v(22.62, 5.78) * mm, "end": v(22.62, 7.99) * mm});
            skLineSegment(sketch, "E607", {"start": v(22.62, 7.99) * mm, "end": v(22.62, 10.25) * mm});
            skLineSegment(sketch, "E608", {"start": v(22.62, 10.25) * mm, "end": v(23.04, 11.93) * mm});
            skLineSegment(sketch, "E609", {"start": v(23.04, 11.93) * mm, "end": v(24.2, 14.03) * mm});
            skLineSegment(sketch, "E610", {"start": v(24.2, 14.03) * mm, "end": v(25.25, 15.87) * mm});
            skLineSegment(sketch, "E611", {"start": v(25.25, 15.87) * mm, "end": v(26.35, 17.18) * mm});
            skLineSegment(sketch, "E612", {"start": v(26.35, 17.18) * mm, "end": v(28.2, 18.13) * mm});
            skLineSegment(sketch, "E613", {"start": v(28.2, 18.13) * mm, "end": v(28.98, 18.13) * mm});
            skLineSegment(sketch, "E614", {"start": v(28.98, 18.13) * mm, "end": v(29.45, 17.66) * mm});
            skLineSegment(sketch, "E615", {"start": v(29.45, 17.66) * mm, "end": v(28.25, 17.18) * mm});
            skLineSegment(sketch, "E616", {"start": v(28.25, 17.18) * mm, "end": v(26.88, 15.87) * mm});
            skLineSegment(sketch, "E617", {"start": v(26.88, 15.87) * mm, "end": v(25.93, 13.72) * mm});
            skLineSegment(sketch, "E618", {"start": v(25.93, 13.72) * mm, "end": v(25.4, 12.03) * mm});
            skLineSegment(sketch, "E619", {"start": v(25.4, 12.03) * mm, "end": v(25.4, 10.3) * mm});
            skLineSegment(sketch, "E620", {"start": v(25.4, 10.3) * mm, "end": v(25.4, 8.78) * mm});
            skLineSegment(sketch, "E621", {"start": v(25.4, 8.78) * mm, "end": v(25.4, 5.78) * mm});
            skLineSegment(sketch, "E622", {"start": v(25.4, 5.78) * mm, "end": v(25.4, 4.15) * mm});
            skLineSegment(sketch, "E623", {"start": v(25.4, 4.15) * mm, "end": v(26.1, 3.2) * mm});
            skLineSegment(sketch, "E624", {"start": v(26.1, 3.2) * mm, "end": v(26.88, 2.63) * mm});
            skLineSegment(sketch, "E625", {"start": v(26.88, 2.63) * mm, "end": v(28.25, 1.94) * mm});
            skLineSegment(sketch, "E626", {"start": v(28.25, 1.94) * mm, "end": v(29.87, 2.63) * mm});
            skLineSegment(sketch, "E627", {"start": v(29.87, 2.63) * mm, "end": v(31.03, 4.26) * mm});
            skLineSegment(sketch, "E628", {"start": v(31.03, 4.26) * mm, "end": v(31.71, 6.62) * mm});
            skLineSegment(sketch, "E629", {"start": v(31.71, 6.62) * mm, "end": v(32.13, 10.2) * mm});
            skLineSegment(sketch, "E630", {"start": v(32.13, 10.2) * mm, "end": v(31.82, 13.24) * mm});
            skLineSegment(sketch, "E631", {"start": v(31.82, 13.24) * mm, "end": v(31.19, 15.87) * mm});
            skLineSegment(sketch, "E632", {"start": v(31.19, 15.87) * mm, "end": v(30.66, 17.92) * mm});
            skLineSegment(sketch, "E633", {"start": v(30.66, 17.92) * mm, "end": v(29.56, 20.02) * mm});
            skLineSegment(sketch, "E634", {"start": v(29.56, 20.02) * mm, "end": v(27.72, 22.65) * mm});
            skLineSegment(sketch, "E635", {"start": v(27.72, 22.65) * mm, "end": v(25.88, 24.12) * mm});
            skLineSegment(sketch, "E636", {"start": v(25.88, 24.12) * mm, "end": v(24.1, 24.54) * mm});
            skLineSegment(sketch, "E637", {"start": v(24.1, 24.54) * mm, "end": v(22.99, 24.49) * mm});
            skLineSegment(sketch, "E638", {"start": v(24.57, 0.58) * mm, "end": v(26, 0) * mm});
            skLineSegment(sketch, "E639", {"start": v(26, 0) * mm, "end": v(27.21, 0) * mm});
            skLineSegment(sketch, "E640", {"start": v(27.21, 0) * mm, "end": v(28.4, 0.58) * mm});
            skLineSegment(sketch, "E641", {"start": v(34.34, 14.77) * mm, "end": v(34.71, 13.18) * mm});
            skLineSegment(sketch, "E642", {"start": v(34.71, 13.18) * mm, "end": v(34.94, 12.08) * mm});
            skLineSegment(sketch, "E643", {"start": v(34.94, 12.08) * mm, "end": v(34.94, 11.25) * mm});
            skLineSegment(sketch, "E644", {"start": v(34.94, 11.25) * mm, "end": v(34.87, 10.46) * mm});
            skLineSegment(sketch, "E645", {"start": v(49.9, 18.16) * mm, "end": v(47.64, 18.16) * mm});
            skLineSegment(sketch, "E646", {"start": v(47.64, 18.16) * mm, "end": v(46.45, 18.16) * mm});
            skLineSegment(sketch, "E647", {"start": v(46.45, 18.16) * mm, "end": v(43.93, 18.03) * mm});
            skLineSegment(sketch, "E648", {"start": v(39.42, 12.5) * mm, "end": v(38.4, 10.96) * mm});
            skLineSegment(sketch, "E649", {"start": v(38.4, 10.96) * mm, "end": v(37.87, 9.23) * mm});
            skLineSegment(sketch, "E650", {"start": v(37.87, 9.23) * mm, "end": v(37.3, 7.77) * mm});
            skLineSegment(sketch, "E651", {"start": v(37.3, 7.77) * mm, "end": v(36.64, 5.87) * mm});
            skLineSegment(sketch, "E652", {"start": v(37.03, 1.37) * mm, "end": v(37.65, 0.35) * mm});
            skLineSegment(sketch, "E653", {"start": v(37.65, 0.35) * mm, "end": v(38.71, -0.18) * mm});
            skLineSegment(sketch, "E654", {"start": v(43.35, 2.78) * mm, "end": v(44.94, 4.77) * mm});
            skLineSegment(sketch, "E655", {"start": v(44.94, 4.77) * mm, "end": v(45.87, 7.07) * mm});
            skLineSegment(sketch, "E656", {"start": v(45.87, 7.07) * mm, "end": v(46.45, 8.08) * mm});
            skLineSegment(sketch, "E657", {"start": v(46.45, 8.08) * mm, "end": v(46.71, 8.57) * mm});
            skLineSegment(sketch, "E658", {"start": v(46.71, 8.57) * mm, "end": v(46.93, 7.46) * mm});
            skLineSegment(sketch, "E659", {"start": v(46.93, 7.46) * mm, "end": v(46.58, 5.87) * mm});
            skLineSegment(sketch, "E660", {"start": v(46.58, 5.87) * mm, "end": v(46.54, 4.24) * mm});
            skLineSegment(sketch, "E661", {"start": v(46.54, 4.24) * mm, "end": v(46.14, 2.65) * mm});
            skLineSegment(sketch, "E662", {"start": v(46.14, 2.65) * mm, "end": v(46, 1.37) * mm});
            skLineSegment(sketch, "E663", {"start": v(46, 1.37) * mm, "end": v(46, 0.26) * mm});
            skLineSegment(sketch, "E664", {"start": v(46, 0.26) * mm, "end": v(46.45, -0.1) * mm});
            skLineSegment(sketch, "E665", {"start": v(46.45, -0.1) * mm, "end": v(48.04, 0.61) * mm});
            skLineSegment(sketch, "E666", {"start": v(48.04, 0.61) * mm, "end": v(49.36, 1.14) * mm});
            skLineSegment(sketch, "E667", {"start": v(49.36, 1.14) * mm, "end": v(50.07, 1.54) * mm});
            skLineSegment(sketch, "E668", {"start": v(50.07, 1.54) * mm, "end": v(50.65, 1.32) * mm});
            skLineSegment(sketch, "E669", {"start": v(50.65, 1.32) * mm, "end": v(51.4, 1.32) * mm});
            skLineSegment(sketch, "E670", {"start": v(51.4, 1.32) * mm, "end": v(51.8, 1.8) * mm});
            skLineSegment(sketch, "E671", {"start": v(51.8, 1.8) * mm, "end": v(51.62, 2.78) * mm});
            skLineSegment(sketch, "E672", {"start": v(51.62, 2.78) * mm, "end": v(51.3, 3.35) * mm});
            skLineSegment(sketch, "E673", {"start": v(51.3, 3.35) * mm, "end": v(50.03, 2.91) * mm});
            skLineSegment(sketch, "E674", {"start": v(36.64, 5.87) * mm, "end": v(36.35, 3.76) * mm});
            skLineSegment(sketch, "E675", {"start": v(36.35, 3.76) * mm, "end": v(36.42, 2.98) * mm});
            skLineSegment(sketch, "E676", {"start": v(36.42, 2.98) * mm, "end": v(36.76, 1.9) * mm});
            skLineSegment(sketch, "E677", {"start": v(36.76, 1.9) * mm, "end": v(37.03, 1.37) * mm});
            skLineSegment(sketch, "E678", {"start": v(38.71, -0.18) * mm, "end": v(39.32, 0) * mm});
            skLineSegment(sketch, "E679", {"start": v(39.32, 0) * mm, "end": v(40.3, 0.18) * mm});
            skLineSegment(sketch, "E680", {"start": v(40.3, 0.18) * mm, "end": v(40.99, 0.52) * mm});
            skLineSegment(sketch, "E681", {"start": v(40.99, 0.52) * mm, "end": v(41.53, 0.94) * mm});
            skLineSegment(sketch, "E682", {"start": v(41.53, 0.94) * mm, "end": v(42.3, 1.37) * mm});
            skLineSegment(sketch, "E683", {"start": v(42.3, 1.37) * mm, "end": v(42.84, 1.9) * mm});
            skLineSegment(sketch, "E684", {"start": v(42.84, 1.9) * mm, "end": v(43.35, 2.78) * mm});
            skLineSegment(sketch, "E685", {"start": v(50.03, 2.91) * mm, "end": v(49.26, 2.55) * mm});
            skLineSegment(sketch, "E686", {"start": v(49.26, 2.55) * mm, "end": v(49.1, 2.91) * mm});
            skLineSegment(sketch, "E687", {"start": v(49.1, 2.91) * mm, "end": v(48.82, 5.3) * mm});
            skLineSegment(sketch, "E688", {"start": v(48.82, 5.3) * mm, "end": v(48.97, 7.75) * mm});
            skLineSegment(sketch, "E689", {"start": v(48.97, 7.75) * mm, "end": v(49.26, 12.36) * mm});
            skLineSegment(sketch, "E690", {"start": v(49.26, 12.36) * mm, "end": v(49.45, 15.2) * mm});
            skLineSegment(sketch, "E691", {"start": v(49.45, 15.2) * mm, "end": v(49.57, 17.02) * mm});
            skLineSegment(sketch, "E692", {"start": v(49.57, 17.02) * mm, "end": v(49.9, 18.16) * mm});
            skLineSegment(sketch, "E693", {"start": v(39.42, 12.5) * mm, "end": v(40.65, 14.43) * mm});
            skLineSegment(sketch, "E694", {"start": v(40.65, 14.43) * mm, "end": v(41.99, 15.98) * mm});
            skLineSegment(sketch, "E695", {"start": v(41.99, 15.98) * mm, "end": v(43.12, 17.3) * mm});
            skLineSegment(sketch, "E696", {"start": v(43.12, 17.3) * mm, "end": v(43.93, 18.03) * mm});
            skLineSegment(sketch, "E697", {"start": v(53.5, 0.5) * mm, "end": v(53.92, 3.5) * mm});
            skLineSegment(sketch, "E698", {"start": v(53.92, 3.5) * mm, "end": v(54.02, 5.65) * mm});
            skLineSegment(sketch, "E699", {"start": v(54.02, 5.65) * mm, "end": v(54.02, 8.7) * mm});
            skLineSegment(sketch, "E700", {"start": v(54.39, 14) * mm, "end": v(54.28, 15.74) * mm});
            skLineSegment(sketch, "E701", {"start": v(54.28, 15.74) * mm, "end": v(53.08, 15.67) * mm});
            skLineSegment(sketch, "E702", {"start": v(53.08, 15.67) * mm, "end": v(52.23, 15.27) * mm});
            skLineSegment(sketch, "E703", {"start": v(52.23, 15.27) * mm, "end": v(51.66, 15.85) * mm});
            skLineSegment(sketch, "E704", {"start": v(51.66, 15.85) * mm, "end": v(51.55, 16.84) * mm});
            skLineSegment(sketch, "E705", {"start": v(51.55, 16.84) * mm, "end": v(53.23, 16.9) * mm});
            skLineSegment(sketch, "E706", {"start": v(53.23, 16.9) * mm, "end": v(54.55, 17.1) * mm});
            skLineSegment(sketch, "E707", {"start": v(54.55, 17.1) * mm, "end": v(55.6, 17.58) * mm});
            skLineSegment(sketch, "E708", {"start": v(55.6, 17.58) * mm, "end": v(56.44, 17.74) * mm});
            skLineSegment(sketch, "E709", {"start": v(56.44, 17.74) * mm, "end": v(56.91, 18.1) * mm});
            skLineSegment(sketch, "E710", {"start": v(56.91, 18.1) * mm, "end": v(57.7, 17.9) * mm});
            skLineSegment(sketch, "E711", {"start": v(57.7, 17.9) * mm, "end": v(57.49, 15.74) * mm});
            skLineSegment(sketch, "E712", {"start": v(57.49, 15.74) * mm, "end": v(57.33, 13.64) * mm});
            skLineSegment(sketch, "E713", {"start": v(57.33, 13.64) * mm, "end": v(56.96, 11.54) * mm});
            skLineSegment(sketch, "E714", {"start": v(56.96, 11.54) * mm, "end": v(56.91, 10.22) * mm});
            skLineSegment(sketch, "E715", {"start": v(56.91, 10.22) * mm, "end": v(56.8, 8.54) * mm});
            skLineSegment(sketch, "E716", {"start": v(56.8, 8.54) * mm, "end": v(57.07, 7.49) * mm});
            skLineSegment(sketch, "E717", {"start": v(57.07, 7.49) * mm, "end": v(58.33, 9.75) * mm});
            skLineSegment(sketch, "E718", {"start": v(58.33, 9.75) * mm, "end": v(59.07, 11.17) * mm});
            skLineSegment(sketch, "E719", {"start": v(59.07, 11.17) * mm, "end": v(59.9, 12.43) * mm});
            skLineSegment(sketch, "E720", {"start": v(59.9, 12.43) * mm, "end": v(60.64, 13.48) * mm});
            skLineSegment(sketch, "E721", {"start": v(60.64, 13.48) * mm, "end": v(61.7, 14.8) * mm});
            skLineSegment(sketch, "E722", {"start": v(61.7, 14.8) * mm, "end": v(62.7, 16.16) * mm});
            skLineSegment(sketch, "E723", {"start": v(62.7, 16.16) * mm, "end": v(63.64, 17.16) * mm});
            skLineSegment(sketch, "E724", {"start": v(63.64, 17.16) * mm, "end": v(64.11, 17.69) * mm});
            skLineSegment(sketch, "E725", {"start": v(64.11, 17.69) * mm, "end": v(64.37, 17.84) * mm});
            skLineSegment(sketch, "E726", {"start": v(64.37, 17.84) * mm, "end": v(66.8, 18) * mm});
            skLineSegment(sketch, "E727", {"start": v(66.8, 18) * mm, "end": v(66.8, 15.22) * mm});
            skLineSegment(sketch, "E728", {"start": v(66.8, 15.22) * mm, "end": v(66.48, 13) * mm});
            skLineSegment(sketch, "E729", {"start": v(66.48, 13) * mm, "end": v(66.42, 12.06) * mm});
            skLineSegment(sketch, "E730", {"start": v(66.42, 12.06) * mm, "end": v(66.27, 10.75) * mm});
            skLineSegment(sketch, "E731", {"start": v(66.27, 10.75) * mm, "end": v(66.27, 9.49) * mm});
            skLineSegment(sketch, "E732", {"start": v(66.27, 9.49) * mm, "end": v(66.27, 8.17) * mm});
            skLineSegment(sketch, "E733", {"start": v(66.27, 8.17) * mm, "end": v(66.21, 7.44) * mm});
            skLineSegment(sketch, "E734", {"start": v(66.21, 7.44) * mm, "end": v(66.95, 8.7) * mm});
            skLineSegment(sketch, "E735", {"start": v(66.95, 8.7) * mm, "end": v(67.95, 10.28) * mm});
            skLineSegment(sketch, "E736", {"start": v(67.95, 10.28) * mm, "end": v(69.84, 13.27) * mm});
            skLineSegment(sketch, "E737", {"start": v(69.84, 13.27) * mm, "end": v(71.1, 14.95) * mm});
            skLineSegment(sketch, "E738", {"start": v(71.1, 14.95) * mm, "end": v(72, 16.32) * mm});
            skLineSegment(sketch, "E739", {"start": v(72, 16.32) * mm, "end": v(73.05, 17.48) * mm});
            skLineSegment(sketch, "E740", {"start": v(73.05, 17.48) * mm, "end": v(73.3, 18) * mm});
            skLineSegment(sketch, "E741", {"start": v(73.3, 18) * mm, "end": v(74.78, 18.1) * mm});
            skLineSegment(sketch, "E742", {"start": v(74.78, 18.1) * mm, "end": v(75.94, 18.16) * mm});
            skLineSegment(sketch, "E743", {"start": v(75.94, 18.16) * mm, "end": v(76.52, 18) * mm});
            skLineSegment(sketch, "E744", {"start": v(76.52, 18) * mm, "end": v(76.46, 17.16) * mm});
            skLineSegment(sketch, "E745", {"start": v(76.46, 17.16) * mm, "end": v(76.1, 16.27) * mm});
            skLineSegment(sketch, "E746", {"start": v(76.1, 16.27) * mm, "end": v(75.73, 14.85) * mm});
            skLineSegment(sketch, "E747", {"start": v(75.73, 14.85) * mm, "end": v(75.46, 11.01) * mm});
            skLineSegment(sketch, "E748", {"start": v(75.46, 11.01) * mm, "end": v(74.89, 7.17) * mm});
            skLineSegment(sketch, "E749", {"start": v(74.89, 7.17) * mm, "end": v(75.04, 5.5) * mm});
            skLineSegment(sketch, "E750", {"start": v(75.94, 2.44) * mm, "end": v(76.73, 2.65) * mm});
            skLineSegment(sketch, "E751", {"start": v(76.73, 2.65) * mm, "end": v(76.88, 1.97) * mm});
            skLineSegment(sketch, "E752", {"start": v(76.88, 1.97) * mm, "end": v(76.73, 1.45) * mm});
            skLineSegment(sketch, "E753", {"start": v(76.73, 1.45) * mm, "end": v(75.62, 1.03) * mm});
            skLineSegment(sketch, "E754", {"start": v(75.62, 1.03) * mm, "end": v(74.89, 0.55) * mm});
            skLineSegment(sketch, "E755", {"start": v(74.89, 0.55) * mm, "end": v(73.47, 0.55) * mm});
            skLineSegment(sketch, "E756", {"start": v(73.47, 0.55) * mm, "end": v(71.73, 0.13) * mm});
            skLineSegment(sketch, "E757", {"start": v(71.73, 0.13) * mm, "end": v(72.26, 2.23) * mm});
            skLineSegment(sketch, "E758", {"start": v(72.26, 2.23) * mm, "end": v(72.68, 4.18) * mm});
            skLineSegment(sketch, "E759", {"start": v(72.68, 4.18) * mm, "end": v(72.73, 5.65) * mm});
            skLineSegment(sketch, "E760", {"start": v(72.73, 5.65) * mm, "end": v(73.1, 15.06) * mm});
            skLineSegment(sketch, "E761", {"start": v(73.1, 15.06) * mm, "end": v(73.2, 15.64) * mm});
            skLineSegment(sketch, "E762", {"start": v(73.2, 15.64) * mm, "end": v(71.73, 14.43) * mm});
            skLineSegment(sketch, "E763", {"start": v(71.73, 14.43) * mm, "end": v(70.84, 13.38) * mm});
            skLineSegment(sketch, "E764", {"start": v(70.84, 13.38) * mm, "end": v(69.63, 11.59) * mm});
            skLineSegment(sketch, "E765", {"start": v(69.63, 11.59) * mm, "end": v(68.53, 9.49) * mm});
            skLineSegment(sketch, "E766", {"start": v(68.53, 9.49) * mm, "end": v(67.84, 8.23) * mm});
            skLineSegment(sketch, "E767", {"start": v(67.84, 8.23) * mm, "end": v(66.48, 5.5) * mm});
            skLineSegment(sketch, "E768", {"start": v(66.48, 5.5) * mm, "end": v(65.69, 2.92) * mm});
            skLineSegment(sketch, "E769", {"start": v(65.69, 2.92) * mm, "end": v(65.32, 1.4) * mm});
            skLineSegment(sketch, "E770", {"start": v(65.32, 1.4) * mm, "end": v(65.32, 0.82) * mm});
            skLineSegment(sketch, "E771", {"start": v(65.32, 0.82) * mm, "end": v(65.37, 0.34) * mm});
            skLineSegment(sketch, "E772", {"start": v(65.37, 0.34) * mm, "end": v(63.27, 0.34) * mm});
            skLineSegment(sketch, "E773", {"start": v(63.27, 0.34) * mm, "end": v(63.59, 6.02) * mm});
            skLineSegment(sketch, "E774", {"start": v(63.59, 6.02) * mm, "end": v(63.64, 7.75) * mm});
            skLineSegment(sketch, "E775", {"start": v(63.64, 7.75) * mm, "end": v(63.9, 13.38) * mm});
            skLineSegment(sketch, "E776", {"start": v(63.9, 13.38) * mm, "end": v(63.74, 14.95) * mm});
            skLineSegment(sketch, "E777", {"start": v(63.74, 14.95) * mm, "end": v(61.12, 11.96) * mm});
            skLineSegment(sketch, "E778", {"start": v(61.12, 11.96) * mm, "end": v(60.6, 10.85) * mm});
            skLineSegment(sketch, "E779", {"start": v(60.6, 10.85) * mm, "end": v(59.9, 9.75) * mm});
            skLineSegment(sketch, "E780", {"start": v(59.9, 9.75) * mm, "end": v(57.49, 5.8) * mm});
            skLineSegment(sketch, "E781", {"start": v(57.49, 5.8) * mm, "end": v(56.91, 4.18) * mm});
            skLineSegment(sketch, "E782", {"start": v(56.91, 4.18) * mm, "end": v(56.91, 2.7) * mm});
            skLineSegment(sketch, "E783", {"start": v(56.91, 2.7) * mm, "end": v(56.54, 0.4) * mm});
            skLineSegment(sketch, "E784", {"start": v(55.6, 0.5) * mm, "end": v(54.86, 0.5) * mm});
            skLineSegment(sketch, "E785", {"start": v(54.86, 0.5) * mm, "end": v(54.07, 0.4) * mm});
            skLineSegment(sketch, "E786", {"start": v(54.07, 0.4) * mm, "end": v(53.5, 0.5) * mm});
            skLineSegment(sketch, "E787", {"start": v(56.54, 0.4) * mm, "end": v(55.6, 0.5) * mm});
            skLineSegment(sketch, "E788", {"start": v(54.39, 14) * mm, "end": v(54.02, 8.7) * mm});
            skLineSegment(sketch, "E789", {"start": v(41.94, 13.04) * mm, "end": v(40.53, 10.74) * mm});
            skLineSegment(sketch, "E790", {"start": v(40.53, 10.74) * mm, "end": v(39.73, 8.44) * mm});
            skLineSegment(sketch, "E791", {"start": v(39.73, 8.44) * mm, "end": v(39.2, 6.5) * mm});
            skLineSegment(sketch, "E792", {"start": v(39.2, 6.5) * mm, "end": v(39.29, 4.29) * mm});
            skLineSegment(sketch, "E793", {"start": v(39.29, 4.29) * mm, "end": v(39.9, 3.14) * mm});
            skLineSegment(sketch, "E794", {"start": v(39.9, 3.14) * mm, "end": v(41.67, 3.4) * mm});
            skLineSegment(sketch, "E795", {"start": v(41.67, 3.4) * mm, "end": v(43.35, 4.73) * mm});
            skLineSegment(sketch, "E796", {"start": v(43.35, 4.73) * mm, "end": v(44.68, 7.3) * mm});
            skLineSegment(sketch, "E797", {"start": v(44.68, 7.3) * mm, "end": v(46.1, 9.6) * mm});
            skLineSegment(sketch, "E798", {"start": v(46.1, 9.6) * mm, "end": v(46.71, 12.07) * mm});
            skLineSegment(sketch, "E799", {"start": v(46.71, 12.07) * mm, "end": v(46.98, 14.36) * mm});
            skLineSegment(sketch, "E800", {"start": v(46.98, 14.36) * mm, "end": v(46.8, 16.49) * mm});
            skLineSegment(sketch, "E801", {"start": v(46.8, 16.49) * mm, "end": v(46.1, 17.02) * mm});
            skLineSegment(sketch, "E802", {"start": v(46.1, 17.02) * mm, "end": v(44.68, 15.78) * mm});
            skLineSegment(sketch, "E803", {"start": v(44.68, 15.78) * mm, "end": v(43.18, 14.36) * mm});
            skLineSegment(sketch, "E804", {"start": v(43.18, 14.36) * mm, "end": v(41.94, 13.04) * mm});
            skLineSegment(sketch, "E805", {"start": v(82.42, 34.74) * mm, "end": v(84.45, 34.74) * mm});
            skLineSegment(sketch, "E806", {"start": v(84.45, 34.74) * mm, "end": v(85.87, 34.65) * mm});
            skLineSegment(sketch, "E807", {"start": v(85.87, 34.65) * mm, "end": v(86.75, 34.74) * mm});
            skLineSegment(sketch, "E808", {"start": v(86.75, 34.74) * mm, "end": v(86.75, 33.95) * mm});
            skLineSegment(sketch, "E809", {"start": v(86.75, 33.95) * mm, "end": v(85.96, 33.5) * mm});
            skLineSegment(sketch, "E810", {"start": v(85.96, 33.5) * mm, "end": v(85.34, 33.24) * mm});
            skLineSegment(sketch, "E811", {"start": v(85.34, 33.24) * mm, "end": v(84.45, 31.3) * mm});
            skLineSegment(sketch, "E812", {"start": v(84.45, 31.3) * mm, "end": v(83.66, 29.7) * mm});
            skLineSegment(sketch, "E813", {"start": v(83.66, 29.7) * mm, "end": v(83.48, 27.67) * mm});
            skLineSegment(sketch, "E814", {"start": v(83.48, 27.67) * mm, "end": v(83.04, 25.28) * mm});
            skLineSegment(sketch, "E815", {"start": v(83.04, 25.28) * mm, "end": v(82.6, 22.28) * mm});
            skLineSegment(sketch, "E816", {"start": v(82.6, 22.28) * mm, "end": v(82.42, 20.42) * mm});
            skLineSegment(sketch, "E817", {"start": v(82.42, 20.42) * mm, "end": v(82.33, 18.83) * mm});
            skLineSegment(sketch, "E818", {"start": v(82.33, 18.83) * mm, "end": v(81.71, 17.33) * mm});
            skLineSegment(sketch, "E819", {"start": v(81.71, 17.33) * mm, "end": v(81.54, 15.74) * mm});
            skLineSegment(sketch, "E820", {"start": v(81.54, 15.74) * mm, "end": v(81.36, 13.88) * mm});
            skLineSegment(sketch, "E821", {"start": v(81.36, 13.88) * mm, "end": v(81.45, 12.11) * mm});
            skLineSegment(sketch, "E822", {"start": v(81.45, 12.11) * mm, "end": v(81.36, 9.1) * mm});
            skLineSegment(sketch, "E823", {"start": v(81.36, 9.1) * mm, "end": v(82.33, 10.43) * mm});
            skLineSegment(sketch, "E824", {"start": v(88.56, 17.77) * mm, "end": v(88.96, 18.21) * mm});
            skLineSegment(sketch, "E825", {"start": v(88.96, 18.21) * mm, "end": v(90.55, 18.21) * mm});
            skLineSegment(sketch, "E826", {"start": v(90.55, 18.21) * mm, "end": v(91.7, 18.21) * mm});
            skLineSegment(sketch, "E827", {"start": v(91.7, 18.21) * mm, "end": v(92.32, 17.77) * mm});
            skLineSegment(sketch, "E828", {"start": v(92.32, 17.77) * mm, "end": v(92.05, 15.74) * mm});
            skLineSegment(sketch, "E829", {"start": v(92.05, 15.74) * mm, "end": v(91.52, 8.67) * mm});
            skLineSegment(sketch, "E830", {"start": v(91.52, 8.67) * mm, "end": v(91, 7.25) * mm});
            skLineSegment(sketch, "E831", {"start": v(91, 7.25) * mm, "end": v(90.29, 6.02) * mm});
            skLineSegment(sketch, "E832", {"start": v(90.29, 6.02) * mm, "end": v(88.34, 2.75) * mm});
            skLineSegment(sketch, "E833", {"start": v(88.34, 2.75) * mm, "end": v(86.84, 1.07) * mm});
            skLineSegment(sketch, "E834", {"start": v(86.84, 1.07) * mm, "end": v(85.25, -1.23) * mm});
            skLineSegment(sketch, "E835", {"start": v(85.25, -1.23) * mm, "end": v(83.57, -2.56) * mm});
            skLineSegment(sketch, "E836", {"start": v(83.57, -2.56) * mm, "end": v(82.77, -3.44) * mm});
            skLineSegment(sketch, "E837", {"start": v(82.77, -3.44) * mm, "end": v(81.45, -4.33) * mm});
            skLineSegment(sketch, "E838", {"start": v(81.45, -4.33) * mm, "end": v(81.1, -5.03) * mm});
            skLineSegment(sketch, "E839", {"start": v(81.1, -5.03) * mm, "end": v(80.2, -4.06) * mm});
            skLineSegment(sketch, "E840", {"start": v(80.2, -4.06) * mm, "end": v(81.27, -2.82) * mm});
            skLineSegment(sketch, "E841", {"start": v(81.27, -2.82) * mm, "end": v(82.86, -2.03) * mm});
            skLineSegment(sketch, "E842", {"start": v(82.86, -2.03) * mm, "end": v(85.96, 1.68) * mm});
            skLineSegment(sketch, "E843", {"start": v(85.96, 1.68) * mm, "end": v(87.1, 4.16) * mm});
            skLineSegment(sketch, "E844", {"start": v(87.1, 4.16) * mm, "end": v(87.99, 6.1) * mm});
            skLineSegment(sketch, "E845", {"start": v(87.99, 6.1) * mm, "end": v(88.96, 10.35) * mm});
            skLineSegment(sketch, "E846", {"start": v(88.96, 10.35) * mm, "end": v(88.87, 12.03) * mm});
            skLineSegment(sketch, "E847", {"start": v(88.87, 12.03) * mm, "end": v(88.87, 13.8) * mm});
            skLineSegment(sketch, "E848", {"start": v(88.87, 13.8) * mm, "end": v(88.87, 14.77) * mm});
            skLineSegment(sketch, "E849", {"start": v(88.87, 14.77) * mm, "end": v(88.34, 15.74) * mm});
            skLineSegment(sketch, "E850", {"start": v(88.34, 15.74) * mm, "end": v(87.55, 15.74) * mm});
            skLineSegment(sketch, "E851", {"start": v(87.55, 15.74) * mm, "end": v(86.75, 14.41) * mm});
            skLineSegment(sketch, "E852", {"start": v(86.75, 14.41) * mm, "end": v(85.96, 12.9) * mm});
            skLineSegment(sketch, "E853", {"start": v(85.96, 12.9) * mm, "end": v(84.45, 10.88) * mm});
            skLineSegment(sketch, "E854", {"start": v(84.45, 10.88) * mm, "end": v(83.57, 9.37) * mm});
            skLineSegment(sketch, "E855", {"start": v(83.57, 9.37) * mm, "end": v(82.33, 8.14) * mm});
            skLineSegment(sketch, "E856", {"start": v(82.33, 8.14) * mm, "end": v(81, 5.49) * mm});
            skLineSegment(sketch, "E857", {"start": v(81, 5.49) * mm, "end": v(80.39, 3.28) * mm});
            skLineSegment(sketch, "E858", {"start": v(80.39, 3.28) * mm, "end": v(80.39, 1.5) * mm});
            skLineSegment(sketch, "E859", {"start": v(80.39, 1.5) * mm, "end": v(80.39, 0.54) * mm});
            skLineSegment(sketch, "E860", {"start": v(80.39, 0.54) * mm, "end": v(78.62, 0.18) * mm});
            skLineSegment(sketch, "E861", {"start": v(78.62, 0.18) * mm, "end": v(77.56, 0.27) * mm});
            skLineSegment(sketch, "E862", {"start": v(79.24, 20.25) * mm, "end": v(79.6, 22.46) * mm});
            skLineSegment(sketch, "E863", {"start": v(79.6, 22.46) * mm, "end": v(80.39, 25.1) * mm});
            skLineSegment(sketch, "E864", {"start": v(80.39, 25.1) * mm, "end": v(81.89, 32.36) * mm});
            skLineSegment(sketch, "E865", {"start": v(81.89, 32.36) * mm, "end": v(82.33, 33.95) * mm});
            skLineSegment(sketch, "E866", {"start": v(82.33, 33.95) * mm, "end": v(82.4, 34.58) * mm});
            skLineSegment(sketch, "E867", {"start": v(82.4, 34.58) * mm, "end": v(82.42, 34.74) * mm});
            skLineSegment(sketch, "E868", {"start": v(79.24, 20.25) * mm, "end": v(78.88, 18.08) * mm});
            skPoint(sketch, "E868.endSnap0", {"position": v(82.02, 18.08) * mm});
            skLineSegment(sketch, "E869", {"start": v(78.88, 18.08) * mm, "end": v(78.44, 13.09) * mm});
            skLineSegment(sketch, "E870", {"start": v(78.44, 13.09) * mm, "end": v(78.02, 3.89) * mm});
            skLineSegment(sketch, "E871", {"start": v(78.02, 3.89) * mm, "end": v(77.56, 0.27) * mm});
            skLineSegment(sketch, "E872", {"start": v(75.04, 5.5) * mm, "end": v(75.04, 2.47) * mm});
            skLineSegment(sketch, "E873", {"start": v(75.04, 2.47) * mm, "end": v(75.18, 2.05) * mm});
            skLineSegment(sketch, "E874", {"start": v(75.18, 2.05) * mm, "end": v(75.94, 2.44) * mm});
            skLineSegment(sketch, "E875", {"start": v(82.33, 10.43) * mm, "end": v(83.41, 12.22) * mm});
            skLineSegment(sketch, "E876", {"start": v(83.41, 12.22) * mm, "end": v(84.6, 13.89) * mm});
            skLineSegment(sketch, "E877", {"start": v(84.6, 13.89) * mm, "end": v(86.3, 15.75) * mm});
            skLineSegment(sketch, "E878", {"start": v(86.3, 15.75) * mm, "end": v(87.52, 16.9) * mm});
            skLineSegment(sketch, "E879", {"start": v(87.52, 16.9) * mm, "end": v(88.56, 17.77) * mm});
            skPoint(sketch, "E880.orphan", {"position": v(88.16, 17.33) * mm});
            skLineSegment(sketch, "E881", {"start": v(101.27, 13.86) * mm, "end": v(102.42, 13.86) * mm});
            skLineSegment(sketch, "E882", {"start": v(102.42, 13.86) * mm, "end": v(102.6, 15.13) * mm});
            skLineSegment(sketch, "E883", {"start": v(102.6, 15.13) * mm, "end": v(102.46, 16.8) * mm});
            skLineSegment(sketch, "E884", {"start": v(102.46, 16.8) * mm, "end": v(102.46, 17.73) * mm});
            skLineSegment(sketch, "E885", {"start": v(102.46, 17.73) * mm, "end": v(102.46, 17.99) * mm});
            skLineSegment(sketch, "E886", {"start": v(102.46, 17.99) * mm, "end": v(101.9, 18.1) * mm});
            skLineSegment(sketch, "E887", {"start": v(101.9, 18.1) * mm, "end": v(101.34, 18.36) * mm});
            skLineSegment(sketch, "E888", {"start": v(101.34, 18.36) * mm, "end": v(100.93, 18.47) * mm});
            skLineSegment(sketch, "E889", {"start": v(100.93, 18.47) * mm, "end": v(99.67, 18.36) * mm});
            skLineSegment(sketch, "E890", {"start": v(99.67, 18.36) * mm, "end": v(98.15, 17.88) * mm});
            skLineSegment(sketch, "E891", {"start": v(98.15, 17.88) * mm, "end": v(97.18, 17.2) * mm});
            skLineSegment(sketch, "E892", {"start": v(97.18, 17.2) * mm, "end": v(96.32, 16.58) * mm});
            skLineSegment(sketch, "E893", {"start": v(96.32, 16.58) * mm, "end": v(95.54, 15.57) * mm});
            skLineSegment(sketch, "E894", {"start": v(95.54, 15.57) * mm, "end": v(95.36, 14.83) * mm});
            skLineSegment(sketch, "E895", {"start": v(95.36, 14.83) * mm, "end": v(95.17, 13.79) * mm});
            skLineSegment(sketch, "E896", {"start": v(95.17, 13.79) * mm, "end": v(94.99, 12.41) * mm});
            skLineSegment(sketch, "E897", {"start": v(94.99, 12.41) * mm, "end": v(95.47, 11.6) * mm});
            skLineSegment(sketch, "E898", {"start": v(95.47, 11.6) * mm, "end": v(96.14, 10.52) * mm});
            skLineSegment(sketch, "E899", {"start": v(96.14, 10.52) * mm, "end": v(97, 9.81) * mm});
            skLineSegment(sketch, "E900", {"start": v(97, 9.81) * mm, "end": v(97.63, 9.14) * mm});
            skLineSegment(sketch, "E901", {"start": v(97.63, 9.14) * mm, "end": v(98.67, 8.59) * mm});
            skLineSegment(sketch, "E902", {"start": v(98.67, 8.59) * mm, "end": v(99.48, 7.66) * mm});
            skLineSegment(sketch, "E903", {"start": v(99.48, 7.66) * mm, "end": v(100.34, 7.1) * mm});
            skLineSegment(sketch, "E904", {"start": v(100.34, 7.1) * mm, "end": v(101.08, 5.98) * mm});
            skLineSegment(sketch, "E905", {"start": v(101.08, 5.98) * mm, "end": v(101.64, 5.17) * mm});
            skLineSegment(sketch, "E906", {"start": v(101.64, 5.17) * mm, "end": v(101.45, 3.05) * mm});
            skLineSegment(sketch, "E907", {"start": v(101.45, 3.05) * mm, "end": v(100.9, 2.45) * mm});
            skLineSegment(sketch, "E908", {"start": v(100.9, 2.45) * mm, "end": v(100.19, 1.71) * mm});
            skLineSegment(sketch, "E909", {"start": v(100.19, 1.71) * mm, "end": v(99.26, 1.27) * mm});
            skLineSegment(sketch, "E910", {"start": v(99.26, 1.27) * mm, "end": v(97.92, 1.2) * mm});
            skLineSegment(sketch, "E911", {"start": v(97.92, 1.2) * mm, "end": v(97.33, 1.53) * mm});
            skLineSegment(sketch, "E912", {"start": v(97.33, 1.53) * mm, "end": v(96.44, 2.16) * mm});
            skLineSegment(sketch, "E913", {"start": v(96.44, 2.16) * mm, "end": v(95.7, 2.83) * mm});
            skLineSegment(sketch, "E914", {"start": v(95.7, 2.83) * mm, "end": v(95.36, 5.32) * mm});
            skLineSegment(sketch, "E915", {"start": v(95.36, 5.32) * mm, "end": v(95.28, 6.54) * mm});
            skLineSegment(sketch, "E916", {"start": v(95.28, 6.54) * mm, "end": v(94.99, 6.95) * mm});
            skLineSegment(sketch, "E917", {"start": v(94.99, 6.95) * mm, "end": v(94.1, 7.03) * mm});
            skLineSegment(sketch, "E918", {"start": v(94.1, 7.03) * mm, "end": v(93.72, 6.91) * mm});
            skLineSegment(sketch, "E919", {"start": v(93.72, 6.91) * mm, "end": v(93.87, 5.91) * mm});
            skLineSegment(sketch, "E920", {"start": v(93.87, 5.91) * mm, "end": v(93.8, 4.98) * mm});
            skLineSegment(sketch, "E921", {"start": v(95.77, 0.22) * mm, "end": v(97.63, -0.07) * mm});
            skLineSegment(sketch, "E922", {"start": v(97.63, -0.07) * mm, "end": v(100.34, 0.45) * mm});
            skLineSegment(sketch, "E923", {"start": v(100.34, 0.45) * mm, "end": v(101.45, 1.04) * mm});
            skLineSegment(sketch, "E924", {"start": v(101.45, 1.04) * mm, "end": v(102.38, 1.93) * mm});
            skLineSegment(sketch, "E925", {"start": v(102.38, 1.93) * mm, "end": v(102.98, 3.05) * mm});
            skLineSegment(sketch, "E926", {"start": v(102.98, 3.05) * mm, "end": v(103.57, 4.39) * mm});
            skLineSegment(sketch, "E927", {"start": v(103.16, 8.47) * mm, "end": v(102.09, 9.7) * mm});
            skLineSegment(sketch, "E928", {"start": v(102.09, 9.7) * mm, "end": v(99.4, 10.93) * mm});
            skLineSegment(sketch, "E929", {"start": v(99.4, 10.93) * mm, "end": v(98.55, 12.12) * mm});
            skLineSegment(sketch, "E930", {"start": v(97.4, 15.65) * mm, "end": v(98.18, 16.69) * mm});
            skLineSegment(sketch, "E931", {"start": v(98.18, 16.69) * mm, "end": v(98.85, 17.2) * mm});
            skLineSegment(sketch, "E932", {"start": v(98.85, 17.2) * mm, "end": v(99.63, 17.25) * mm});
            skLineSegment(sketch, "E933", {"start": v(99.63, 17.25) * mm, "end": v(100.38, 16.87) * mm});
            skLineSegment(sketch, "E934", {"start": v(100.38, 16.87) * mm, "end": v(100.97, 16.2) * mm});
            skLineSegment(sketch, "E935", {"start": v(100.97, 16.2) * mm, "end": v(101.08, 15.54) * mm});
            skLineSegment(sketch, "E936", {"start": v(101.08, 15.54) * mm, "end": v(101.16, 14.98) * mm});
            skLineSegment(sketch, "E937", {"start": v(101.16, 14.98) * mm, "end": v(101.16, 14.23) * mm});
            skLineSegment(sketch, "E938", {"start": v(101.16, 14.23) * mm, "end": v(101.27, 13.86) * mm});
            skLineSegment(sketch, "E939", {"start": v(98.55, 12.12) * mm, "end": v(97.9, 12.97) * mm});
            skLineSegment(sketch, "E940", {"start": v(97.9, 12.97) * mm, "end": v(97.45, 13.86) * mm});
            skLineSegment(sketch, "E941", {"start": v(97.45, 13.86) * mm, "end": v(97.23, 14.96) * mm});
            skLineSegment(sketch, "E942", {"start": v(97.23, 14.96) * mm, "end": v(97.4, 15.65) * mm});
            skLineSegment(sketch, "E943", {"start": v(103.57, 4.39) * mm, "end": v(103.97, 5.4) * mm});
            skLineSegment(sketch, "E944", {"start": v(103.97, 5.4) * mm, "end": v(104.02, 6.45) * mm});
            skLineSegment(sketch, "E945", {"start": v(104.02, 6.45) * mm, "end": v(103.84, 7.1) * mm});
            skLineSegment(sketch, "E946", {"start": v(103.84, 7.1) * mm, "end": v(103.63, 7.97) * mm});
            skLineSegment(sketch, "E947", {"start": v(103.63, 7.97) * mm, "end": v(103.16, 8.47) * mm});
            skLineSegment(sketch, "E948", {"start": v(93.8, 4.98) * mm, "end": v(93.8, 3.62) * mm});
            skLineSegment(sketch, "E949", {"start": v(93.8, 3.62) * mm, "end": v(93.6, 2.83) * mm});
            skLineSegment(sketch, "E950", {"start": v(93.6, 2.83) * mm, "end": v(93.35, 1.9) * mm});
            skLineSegment(sketch, "E951", {"start": v(95.77, 0.22) * mm, "end": v(94.82, 0.52) * mm});
            skLineSegment(sketch, "E952", {"start": v(94.82, 0.52) * mm, "end": v(94.1, 0.82) * mm});
            skLineSegment(sketch, "E953", {"start": v(94.1, 0.82) * mm, "end": v(93.53, 1.1) * mm});
            skLineSegment(sketch, "E954", {"start": v(93.53, 1.1) * mm, "end": v(93.2, 1.37) * mm});
            skLineSegment(sketch, "E955", {"start": v(93.2, 1.37) * mm, "end": v(93.35, 1.9) * mm});
            skLineSegment(sketch, "E956", {"start": v(119.02, 18.25) * mm, "end": v(116.66, 17.78) * mm});
            skLineSegment(sketch, "E957", {"start": v(116.66, 17.78) * mm, "end": v(115.71, 18.15) * mm});
            skLineSegment(sketch, "E958", {"start": v(115.71, 18.15) * mm, "end": v(114.55, 18.1) * mm});
            skLineSegment(sketch, "E959", {"start": v(114.55, 18.1) * mm, "end": v(112.61, 17.04) * mm});
            skLineSegment(sketch, "E960", {"start": v(112.61, 17.04) * mm, "end": v(110.88, 15.62) * mm});
            skLineSegment(sketch, "E961", {"start": v(110.88, 15.62) * mm, "end": v(110.14, 14.89) * mm});
            skLineSegment(sketch, "E962", {"start": v(110.14, 14.89) * mm, "end": v(109.4, 13.9) * mm});
            skLineSegment(sketch, "E963", {"start": v(109.4, 13.9) * mm, "end": v(108.77, 12.84) * mm});
            skLineSegment(sketch, "E964", {"start": v(108.77, 12.84) * mm, "end": v(108.1, 11.47) * mm});
            skLineSegment(sketch, "E965", {"start": v(108.1, 11.47) * mm, "end": v(107.62, 10.26) * mm});
            skLineSegment(sketch, "E966", {"start": v(107.62, 10.26) * mm, "end": v(106.83, 8.58) * mm});
            skLineSegment(sketch, "E967", {"start": v(106.83, 8.58) * mm, "end": v(105.99, 6.85) * mm});
            skLineSegment(sketch, "E968", {"start": v(105.99, 6.85) * mm, "end": v(105.67, 5.22) * mm});
            skLineSegment(sketch, "E969", {"start": v(105.67, 5.22) * mm, "end": v(105.62, 3.9) * mm});
            skLineSegment(sketch, "E970", {"start": v(105.62, 3.9) * mm, "end": v(105.99, 2.8) * mm});
            skLineSegment(sketch, "E971", {"start": v(105.99, 2.8) * mm, "end": v(106.25, 1.49) * mm});
            skLineSegment(sketch, "E972", {"start": v(106.25, 1.49) * mm, "end": v(107.25, 0.54) * mm});
            skLineSegment(sketch, "E973", {"start": v(107.25, 0.54) * mm, "end": v(108.35, 0.23) * mm});
            skLineSegment(sketch, "E974", {"start": v(108.35, 0.23) * mm, "end": v(109.82, 0.65) * mm});
            skLineSegment(sketch, "E975", {"start": v(109.82, 0.65) * mm, "end": v(110.61, 1.17) * mm});
            skLineSegment(sketch, "E976", {"start": v(110.61, 1.17) * mm, "end": v(112.08, 2.75) * mm});
            skLineSegment(sketch, "E977", {"start": v(112.08, 2.75) * mm, "end": v(113.14, 4.11) * mm});
            skLineSegment(sketch, "E978", {"start": v(113.14, 4.11) * mm, "end": v(113.82, 5.27) * mm});
            skLineSegment(sketch, "E979", {"start": v(113.82, 5.27) * mm, "end": v(114.4, 6.32) * mm});
            skLineSegment(sketch, "E980", {"start": v(114.4, 6.32) * mm, "end": v(115.08, 7.37) * mm});
            skLineSegment(sketch, "E981", {"start": v(115.08, 7.37) * mm, "end": v(115.6, 7.85) * mm});
            skLineSegment(sketch, "E982", {"start": v(115.6, 7.85) * mm, "end": v(115.92, 8.8) * mm});
            skLineSegment(sketch, "E983", {"start": v(115.92, 8.8) * mm, "end": v(116.24, 7.85) * mm});
            skLineSegment(sketch, "E984", {"start": v(116.24, 7.85) * mm, "end": v(116.24, 6.74) * mm});
            skLineSegment(sketch, "E985", {"start": v(116.24, 6.74) * mm, "end": v(116.03, 5.48) * mm});
            skLineSegment(sketch, "E986", {"start": v(116.03, 5.48) * mm, "end": v(115.5, 2.33) * mm});
            skLineSegment(sketch, "E987", {"start": v(115.5, 2.33) * mm, "end": v(115.24, 1.07) * mm});
            skLineSegment(sketch, "E988", {"start": v(115.24, 1.07) * mm, "end": v(115.13, 0.23) * mm});
            skLineSegment(sketch, "E989", {"start": v(115.13, 0.23) * mm, "end": v(115.34, -0.09) * mm});
            skLineSegment(sketch, "E990", {"start": v(115.34, -0.09) * mm, "end": v(116.5, 0.49) * mm});
            skLineSegment(sketch, "E991", {"start": v(116.5, 0.49) * mm, "end": v(117.34, 1.22) * mm});
            skLineSegment(sketch, "E992", {"start": v(117.34, 1.22) * mm, "end": v(118.4, 1.7) * mm});
            skLineSegment(sketch, "E993", {"start": v(118.4, 1.7) * mm, "end": v(120.5, 1.86) * mm});
            skLineSegment(sketch, "E994", {"start": v(120.5, 1.86) * mm, "end": v(120.76, 2.85) * mm});
            skLineSegment(sketch, "E995", {"start": v(120.76, 2.85) * mm, "end": v(120.18, 2.75) * mm});
            skLineSegment(sketch, "E996", {"start": v(120.18, 2.75) * mm, "end": v(119.55, 2.64) * mm});
            skLineSegment(sketch, "E997", {"start": v(119.55, 2.64) * mm, "end": v(118.55, 2.64) * mm});
            skLineSegment(sketch, "E998", {"start": v(118.55, 2.64) * mm, "end": v(118.08, 2.9) * mm});
            skLineSegment(sketch, "E999", {"start": v(118.08, 2.9) * mm, "end": v(118.02, 4.06) * mm});
            skLineSegment(sketch, "E1000", {"start": v(118.02, 4.06) * mm, "end": v(118.34, 5.53) * mm});
            skLineSegment(sketch, "E1001", {"start": v(118.34, 5.53) * mm, "end": v(118.55, 7.58) * mm});
            skLineSegment(sketch, "E1002", {"start": v(118.55, 7.58) * mm, "end": v(118.6, 9.69) * mm});
            skLineSegment(sketch, "E1003", {"start": v(118.6, 9.69) * mm, "end": v(119.02, 16.15) * mm});
            skLineSegment(sketch, "E1004", {"start": v(119.02, 16.15) * mm, "end": v(118.92, 17.36) * mm});
            skLineSegment(sketch, "E1005", {"start": v(118.92, 17.36) * mm, "end": v(119.03, 18.26) * mm});
            skLineSegment(sketch, "E1006", {"start": v(119.03, 18.26) * mm, "end": v(119.02, 18.25) * mm});
            skLineSegment(sketch, "E1007", {"start": v(119.02, 18.25) * mm, "end": v(119.02, 18.25) * mm});
            skLineSegment(sketch, "E1008", {"start": v(109.04, 8.2) * mm, "end": v(109.26, 9.96) * mm});
            skLineSegment(sketch, "E1009", {"start": v(109.26, 9.96) * mm, "end": v(110.15, 11.2) * mm});
            skLineSegment(sketch, "E1010", {"start": v(110.15, 11.2) * mm, "end": v(110.72, 12.53) * mm});
            skLineSegment(sketch, "E1011", {"start": v(110.72, 12.53) * mm, "end": v(111.47, 13.86) * mm});
            skLineSegment(sketch, "E1012", {"start": v(111.47, 13.86) * mm, "end": v(112.62, 15) * mm});
            skLineSegment(sketch, "E1013", {"start": v(112.62, 15) * mm, "end": v(113.5, 15.9) * mm});
            skLineSegment(sketch, "E1014", {"start": v(113.5, 15.9) * mm, "end": v(114.35, 16.42) * mm});
            skLineSegment(sketch, "E1015", {"start": v(114.35, 16.42) * mm, "end": v(114.88, 16.64) * mm});
            skLineSegment(sketch, "E1016", {"start": v(114.88, 16.64) * mm, "end": v(116.03, 16.5) * mm});
            skLineSegment(sketch, "E1017", {"start": v(116.03, 16.5) * mm, "end": v(116.38, 15.93) * mm});
            skLineSegment(sketch, "E1018", {"start": v(116.38, 15.93) * mm, "end": v(116.56, 14.87) * mm});
            skLineSegment(sketch, "E1019", {"start": v(116.56, 14.87) * mm, "end": v(116.6, 14) * mm});
            skLineSegment(sketch, "E1020", {"start": v(116.6, 14) * mm, "end": v(115.1, 10.01) * mm});
            skLineSegment(sketch, "E1021", {"start": v(115.1, 10.01) * mm, "end": v(114.35, 8.11) * mm});
            skLineSegment(sketch, "E1022", {"start": v(114.35, 8.11) * mm, "end": v(113.46, 6.7) * mm});
            skLineSegment(sketch, "E1023", {"start": v(113.46, 6.7) * mm, "end": v(112.89, 5.46) * mm});
            skLineSegment(sketch, "E1024", {"start": v(112.89, 5.46) * mm, "end": v(112.11, 4.27) * mm});
            skLineSegment(sketch, "E1025", {"start": v(112.11, 4.27) * mm, "end": v(110.83, 3.3) * mm});
            skLineSegment(sketch, "E1026", {"start": v(110.83, 3.3) * mm, "end": v(110.12, 2.98) * mm});
            skLineSegment(sketch, "E1027", {"start": v(110.12, 2.98) * mm, "end": v(109.33, 3.16) * mm});
            skLineSegment(sketch, "E1028", {"start": v(109.33, 3.16) * mm, "end": v(108.4, 4.09) * mm});
            skLineSegment(sketch, "E1029", {"start": v(108.4, 4.09) * mm, "end": v(108.13, 5.37) * mm});
            skLineSegment(sketch, "E1030", {"start": v(108.13, 5.37) * mm, "end": v(108.49, 6.6) * mm});
            skLineSegment(sketch, "E1031", {"start": v(108.49, 6.6) * mm, "end": v(109.02, 8.02) * mm});
            skLineSegment(sketch, "E1032", {"start": v(109.02, 8.02) * mm, "end": v(109.04, 8.2) * mm});
            skSolve(sketch);
        }
        {
            var Q0;
            Q0 = qSketchRegion(id + "F8", true);
            extrude(context, id + "F9", {"entities" : qUnion([Q0]), "depth" : 9 * mm});
        }
        {
            var Q0;
            Q0=qCreatedBy(makeId("Front.planeOp"),FACE);
            var sketch = newSketch(context, id + "F10", { "sketchPlane" : qUnion([Q0])});
            skLineSegment(sketch, "E1033", {"start": v(138.8, -0.8) * mm, "end": v(139.56, -1.4) * mm});
            skLineSegment(sketch, "E1034", {"start": v(145.85, 6.89) * mm, "end": v(145.85, 8.6) * mm});
            skLineSegment(sketch, "E1035", {"start": v(145.85, 8.6) * mm, "end": v(145.88, 10.32) * mm});
            skLineSegment(sketch, "E1036", {"start": v(145.88, 10.32) * mm, "end": v(146.46, 11.37) * mm});
            skLineSegment(sketch, "E1037", {"start": v(146.46, 11.37) * mm, "end": v(147.1, 13.32) * mm});
            skLineSegment(sketch, "E1038", {"start": v(147.1, 13.32) * mm, "end": v(147.61, 17.26) * mm});
            skLineSegment(sketch, "E1039", {"start": v(147.61, 17.26) * mm, "end": v(147.61, 19.35) * mm});
            skLineSegment(sketch, "E1040", {"start": v(147.61, 19.35) * mm, "end": v(147.84, 20.37) * mm});
            skLineSegment(sketch, "E1041", {"start": v(147.84, 20.37) * mm, "end": v(149.5, 22.03) * mm});
            skLineSegment(sketch, "E1042", {"start": v(149.5, 22.03) * mm, "end": v(151.02, 24.13) * mm});
            skLineSegment(sketch, "E1043", {"start": v(151.02, 24.13) * mm, "end": v(151.75, 25.92) * mm});
            skLineSegment(sketch, "E1044", {"start": v(151.75, 25.92) * mm, "end": v(152.12, 27.83) * mm});
            skLineSegment(sketch, "E1045", {"start": v(152.12, 27.83) * mm, "end": v(152.12, 30.4) * mm});
            skLineSegment(sketch, "E1046", {"start": v(152.12, 30.4) * mm, "end": v(150.92, 31.94) * mm});
            skLineSegment(sketch, "E1047", {"start": v(150.92, 31.94) * mm, "end": v(149.9, 32.96) * mm});
            skLineSegment(sketch, "E1048", {"start": v(149.9, 32.96) * mm, "end": v(149.41, 33.61) * mm});
            skLineSegment(sketch, "E1049", {"start": v(149.41, 33.61) * mm, "end": v(149.23, 33.77) * mm});
            skLineSegment(sketch, "E1050", {"start": v(149.23, 33.77) * mm, "end": v(149.23, 32.95) * mm});
            skLineSegment(sketch, "E1051", {"start": v(149.23, 32.95) * mm, "end": v(148.6, 33.37) * mm});
            skLineSegment(sketch, "E1052", {"start": v(148.6, 33.37) * mm, "end": v(148.6, 33.63) * mm});
            skLineSegment(sketch, "E1053", {"start": v(148.6, 33.63) * mm, "end": v(148.83, 34.19) * mm});
            skLineSegment(sketch, "E1054", {"start": v(148.83, 34.19) * mm, "end": v(148.56, 34.79) * mm});
            skLineSegment(sketch, "E1055", {"start": v(148.56, 34.79) * mm, "end": v(148.3, 35.16) * mm});
            skLineSegment(sketch, "E1056", {"start": v(148.3, 35.16) * mm, "end": v(148, 33.91) * mm});
            skLineSegment(sketch, "E1057", {"start": v(148, 33.91) * mm, "end": v(147.69, 32.85) * mm});
            skLineSegment(sketch, "E1058", {"start": v(147.69, 32.85) * mm, "end": v(146.94, 31.63) * mm});
            skLineSegment(sketch, "E1059", {"start": v(146.94, 31.63) * mm, "end": v(146.4, 30.94) * mm});
            skLineSegment(sketch, "E1060", {"start": v(146.4, 30.94) * mm, "end": v(146.83, 32.16) * mm});
            skLineSegment(sketch, "E1061", {"start": v(146.83, 32.16) * mm, "end": v(146.29, 31.5) * mm});
            skLineSegment(sketch, "E1062", {"start": v(146.29, 31.5) * mm, "end": v(145.71, 31.35) * mm});
            skLineSegment(sketch, "E1063", {"start": v(145.71, 31.35) * mm, "end": v(144.21, 31.2) * mm});
            skLineSegment(sketch, "E1064", {"start": v(144.21, 31.2) * mm, "end": v(143.14, 31.17) * mm});
            skLineSegment(sketch, "E1065", {"start": v(143.14, 31.17) * mm, "end": v(141.24, 31.46) * mm});
            skLineSegment(sketch, "E1066", {"start": v(141.24, 31.46) * mm, "end": v(140.26, 31.93) * mm});
            skLineSegment(sketch, "E1067", {"start": v(140.26, 31.93) * mm, "end": v(139.55, 32.34) * mm});
            skLineSegment(sketch, "E1068", {"start": v(139.55, 32.34) * mm, "end": v(138.8, 32.86) * mm});
            skLineSegment(sketch, "E1069", {"start": v(138.8, 32.86) * mm, "end": v(138.54, 33.02) * mm});
            skLineSegment(sketch, "E1070", {"start": v(138.54, 33.02) * mm, "end": v(138.1, 32.35) * mm});
            skLineSegment(sketch, "E1071", {"start": v(138.1, 32.35) * mm, "end": v(137.69, 31.8) * mm});
            skLineSegment(sketch, "E1072", {"start": v(137.69, 31.8) * mm, "end": v(137.51, 31.29) * mm});
            skLineSegment(sketch, "E1073", {"start": v(137.51, 31.29) * mm, "end": v(137.62, 30.9) * mm});
            skLineSegment(sketch, "E1074", {"start": v(137.62, 30.9) * mm, "end": v(136.87, 30.1) * mm});
            skLineSegment(sketch, "E1075", {"start": v(136.87, 30.1) * mm, "end": v(135.88, 29.21) * mm});
            skLineSegment(sketch, "E1076", {"start": v(135.88, 29.21) * mm, "end": v(135.05, 28.2) * mm});
            skLineSegment(sketch, "E1077", {"start": v(135.05, 28.2) * mm, "end": v(134.25, 27.16) * mm});
            skLineSegment(sketch, "E1078", {"start": v(134.25, 27.16) * mm, "end": v(133.87, 25.79) * mm});
            skLineSegment(sketch, "E1079", {"start": v(133.87, 25.79) * mm, "end": v(133.75, 24.7) * mm});
            skLineSegment(sketch, "E1080", {"start": v(133.75, 24.7) * mm, "end": v(133.9, 22.78) * mm});
            skLineSegment(sketch, "E1081", {"start": v(133.9, 22.78) * mm, "end": v(134.4, 21.34) * mm});
            skLineSegment(sketch, "E1082", {"start": v(134.4, 21.34) * mm, "end": v(135.27, 19.78) * mm});
            skLineSegment(sketch, "E1083", {"start": v(135.27, 19.78) * mm, "end": v(135.99, 18.63) * mm});
            skLineSegment(sketch, "E1084", {"start": v(135.99, 18.63) * mm, "end": v(136.38, 17.18) * mm});
            skLineSegment(sketch, "E1085", {"start": v(136.38, 17.18) * mm, "end": v(136.38, 15.7) * mm});
            skLineSegment(sketch, "E1086", {"start": v(136.38, 15.7) * mm, "end": v(136.67, 14.54) * mm});
            skLineSegment(sketch, "E1087", {"start": v(136.67, 14.54) * mm, "end": v(136.67, 13.6) * mm});
            skLineSegment(sketch, "E1088", {"start": v(136.67, 13.6) * mm, "end": v(136.4, 12.48) * mm});
            skLineSegment(sketch, "E1089", {"start": v(136.4, 12.48) * mm, "end": v(135.94, 10.61) * mm});
            skLineSegment(sketch, "E1090", {"start": v(135.94, 10.61) * mm, "end": v(135.62, 9) * mm});
            skLineSegment(sketch, "E1091", {"start": v(135.62, 9) * mm, "end": v(135.45, 7.96) * mm});
            skLineSegment(sketch, "E1092", {"start": v(135.45, 7.96) * mm, "end": v(135.46, 7.29) * mm});
            skLineSegment(sketch, "E1093", {"start": v(135.46, 7.29) * mm, "end": v(135.77, 6.1) * mm});
            skLineSegment(sketch, "E1094", {"start": v(135.77, 6.1) * mm, "end": v(135.94, 4.4) * mm});
            skLineSegment(sketch, "E1095", {"start": v(135.94, 4.4) * mm, "end": v(136.67, 2.58) * mm});
            skLineSegment(sketch, "E1096", {"start": v(136.67, 2.58) * mm, "end": v(136.98, 1.52) * mm});
            skLineSegment(sketch, "E1097", {"start": v(136.98, 1.52) * mm, "end": v(137.43, 0.68) * mm});
            skLineSegment(sketch, "E1098", {"start": v(137.43, 0.68) * mm, "end": v(137.7, 0.24) * mm});
            skLineSegment(sketch, "E1099", {"start": v(137.7, 0.24) * mm, "end": v(138.2, -0.29) * mm});
            skLineSegment(sketch, "E1100", {"start": v(138.2, -0.29) * mm, "end": v(138.8, -0.8) * mm});
            skLineSegment(sketch, "E1101", {"start": v(145.85, 6.89) * mm, "end": v(145.64, 5.24) * mm});
            skLineSegment(sketch, "E1102", {"start": v(145.64, 5.24) * mm, "end": v(145.28, 4.04) * mm});
            skLineSegment(sketch, "E1103", {"start": v(145.28, 4.04) * mm, "end": v(145.08, 3.15) * mm});
            skLineSegment(sketch, "E1104", {"start": v(145.08, 3.15) * mm, "end": v(144.7, 1.93) * mm});
            skLineSegment(sketch, "E1105", {"start": v(144.7, 1.93) * mm, "end": v(144.53, 1.23) * mm});
            skLineSegment(sketch, "E1106", {"start": v(144.53, 1.23) * mm, "end": v(144.29, 0.68) * mm});
            skLineSegment(sketch, "E1107", {"start": v(139.56, -1.4) * mm, "end": v(140.31, -1.55) * mm});
            skLineSegment(sketch, "E1108", {"start": v(140.31, -1.55) * mm, "end": v(141.14, -1.47) * mm});
            skPoint(sketch, "E1108.endSnap0", {"position": v(140.68, -1.47) * mm});
            skLineSegment(sketch, "E1109", {"start": v(141.14, -1.47) * mm, "end": v(141.9, -1.3) * mm});
            skLineSegment(sketch, "E1110", {"start": v(141.9, -1.3) * mm, "end": v(142.47, -1.16) * mm});
            skLineSegment(sketch, "E1111", {"start": v(142.47, -1.16) * mm, "end": v(143.14, -0.88) * mm});
            skLineSegment(sketch, "E1112", {"start": v(143.14, -0.88) * mm, "end": v(143.63, -0.52) * mm});
            skLineSegment(sketch, "E1113", {"start": v(143.63, -0.52) * mm, "end": v(143.98, -0.07) * mm});
            skLineSegment(sketch, "E1114", {"start": v(143.98, -0.07) * mm, "end": v(144.2, 0.32) * mm});
            skLineSegment(sketch, "E1115", {"start": v(144.2, 0.32) * mm, "end": v(144.29, 0.68) * mm});
            skPoint(sketch, "E1116.orphan", {"position": v(143.63, 0) * mm});
            skPoint(sketch, "E1117.orphan", {"position": v(141.04, -1.4) * mm});
            skLineSegment(sketch, "E1118", {"start": v(137.7, 28.55) * mm, "end": v(137.07, 27.62) * mm});
            skLineSegment(sketch, "E1119", {"start": v(136.7, 25.4) * mm, "end": v(137.15, 24.39) * mm});
            skLineSegment(sketch, "E1120", {"start": v(137.15, 24.39) * mm, "end": v(137.6, 23.83) * mm});
            skLineSegment(sketch, "E1121", {"start": v(137.6, 23.83) * mm, "end": v(138.9, 23.38) * mm});
            skLineSegment(sketch, "E1122", {"start": v(138.9, 23.38) * mm, "end": v(139.71, 23.16) * mm});
            skLineSegment(sketch, "E1123", {"start": v(139.71, 23.16) * mm, "end": v(140.46, 22.83) * mm});
            skLineSegment(sketch, "E1124", {"start": v(140.46, 22.83) * mm, "end": v(141.68, 23.2) * mm});
            skLineSegment(sketch, "E1125", {"start": v(141.68, 23.2) * mm, "end": v(142.35, 23.42) * mm});
            skLineSegment(sketch, "E1126", {"start": v(142.35, 23.42) * mm, "end": v(140.75, 24.39) * mm});
            skLineSegment(sketch, "E1127", {"start": v(140.75, 24.39) * mm, "end": v(139.64, 25.28) * mm});
            skLineSegment(sketch, "E1128", {"start": v(139.64, 25.28) * mm, "end": v(138.82, 26.5) * mm});
            skLineSegment(sketch, "E1129", {"start": v(138.82, 26.5) * mm, "end": v(138.26, 27.92) * mm});
            skLineSegment(sketch, "E1130", {"start": v(138.26, 27.92) * mm, "end": v(137.7, 28.55) * mm});
            skLineSegment(sketch, "E1131", {"start": v(136.7, 25.4) * mm, "end": v(136.7, 26.7) * mm});
            skLineSegment(sketch, "E1132", {"start": v(136.7, 26.7) * mm, "end": v(137.07, 27.62) * mm});
            skLineSegment(sketch, "E1133", {"start": v(138.6, 29.26) * mm, "end": v(138.6, 30.11) * mm});
            skLineSegment(sketch, "E1134", {"start": v(138.6, 30.11) * mm, "end": v(138.38, 31.04) * mm});
            skLineSegment(sketch, "E1135", {"start": v(138.38, 31.04) * mm, "end": v(138.75, 31.56) * mm});
            skLineSegment(sketch, "E1136", {"start": v(138.75, 31.56) * mm, "end": v(139.8, 31.04) * mm});
            skLineSegment(sketch, "E1137", {"start": v(139.8, 31.04) * mm, "end": v(140.57, 30.45) * mm});
            skLineSegment(sketch, "E1138", {"start": v(140.57, 30.45) * mm, "end": v(142.5, 30.26) * mm});
            skLineSegment(sketch, "E1139", {"start": v(142.5, 30.26) * mm, "end": v(143.8, 30.26) * mm});
            skLineSegment(sketch, "E1140", {"start": v(143.8, 30.26) * mm, "end": v(145.03, 30.15) * mm});
            skLineSegment(sketch, "E1141", {"start": v(145.03, 30.15) * mm, "end": v(145.63, 30.26) * mm});
            skLineSegment(sketch, "E1142", {"start": v(145.63, 30.26) * mm, "end": v(145.92, 30.11) * mm});
            skLineSegment(sketch, "E1143", {"start": v(145.92, 30.11) * mm, "end": v(145.78, 29.33) * mm});
            skLineSegment(sketch, "E1144", {"start": v(145.78, 29.33) * mm, "end": v(145.74, 28.4) * mm});
            skLineSegment(sketch, "E1145", {"start": v(145.74, 28.4) * mm, "end": v(145.59, 27.55) * mm});
            skLineSegment(sketch, "E1146", {"start": v(145.59, 27.55) * mm, "end": v(145.55, 26.66) * mm});
            skLineSegment(sketch, "E1147", {"start": v(145.55, 26.66) * mm, "end": v(145.4, 25.5) * mm});
            skLineSegment(sketch, "E1148", {"start": v(145.4, 25.5) * mm, "end": v(144.88, 24.69) * mm});
            skLineSegment(sketch, "E1149", {"start": v(144.88, 24.69) * mm, "end": v(144.25, 24.2) * mm});
            skLineSegment(sketch, "E1150", {"start": v(144.25, 24.2) * mm, "end": v(143.8, 24.02) * mm});
            skLineSegment(sketch, "E1151", {"start": v(143.8, 24.02) * mm, "end": v(143.55, 24.02) * mm});
            skLineSegment(sketch, "E1152", {"start": v(143.55, 24.02) * mm, "end": v(142.7, 24.58) * mm});
            skLineSegment(sketch, "E1153", {"start": v(142.7, 24.58) * mm, "end": v(141.02, 25.65) * mm});
            skLineSegment(sketch, "E1154", {"start": v(141.02, 25.65) * mm, "end": v(139.9, 26.66) * mm});
            skLineSegment(sketch, "E1155", {"start": v(139.9, 26.66) * mm, "end": v(139.05, 28.22) * mm});
            skLineSegment(sketch, "E1156", {"start": v(139.05, 28.22) * mm, "end": v(138.6, 29.26) * mm});
            skLineSegment(sketch, "E1157", {"start": v(147.87, 31.86) * mm, "end": v(147.24, 30.49) * mm});
            skLineSegment(sketch, "E1158", {"start": v(147.24, 30.49) * mm, "end": v(146.68, 29.7) * mm});
            skLineSegment(sketch, "E1159", {"start": v(146.68, 29.7) * mm, "end": v(146.4, 29.28) * mm});
            skLineSegment(sketch, "E1160", {"start": v(146.4, 29.28) * mm, "end": v(146.19, 29.07) * mm});
            skLineSegment(sketch, "E1161", {"start": v(146.19, 29.07) * mm, "end": v(145.9, 26.83) * mm});
            skLineSegment(sketch, "E1162", {"start": v(145.9, 26.83) * mm, "end": v(146.98, 26.92) * mm});
            skLineSegment(sketch, "E1163", {"start": v(146.98, 26.92) * mm, "end": v(147.8, 27.4) * mm});
            skLineSegment(sketch, "E1164", {"start": v(147.8, 27.4) * mm, "end": v(148.33, 28.24) * mm});
            skLineSegment(sketch, "E1165", {"start": v(148.33, 28.24) * mm, "end": v(148.57, 29.22) * mm});
            skLineSegment(sketch, "E1166", {"start": v(148.57, 29.22) * mm, "end": v(148.57, 29.99) * mm});
            skLineSegment(sketch, "E1167", {"start": v(148.57, 29.99) * mm, "end": v(148.39, 30.86) * mm});
            skLineSegment(sketch, "E1168", {"start": v(148.39, 30.86) * mm, "end": v(147.87, 31.86) * mm});
            skLineSegment(sketch, "E1169", {"start": v(145.4, 24.67) * mm, "end": v(144.16, 23.42) * mm});
            skLineSegment(sketch, "E1170", {"start": v(144.16, 23.42) * mm, "end": v(144.76, 22.98) * mm});
            skLineSegment(sketch, "E1171", {"start": v(144.76, 22.98) * mm, "end": v(145.13, 22.1) * mm});
            skLineSegment(sketch, "E1172", {"start": v(145.13, 22.1) * mm, "end": v(144.98, 21.73) * mm});
            skLineSegment(sketch, "E1173", {"start": v(144.98, 21.73) * mm, "end": v(146.07, 21.42) * mm});
            skLineSegment(sketch, "E1174", {"start": v(146.07, 21.42) * mm, "end": v(146.82, 21.7) * mm});
            skLineSegment(sketch, "E1175", {"start": v(146.82, 21.7) * mm, "end": v(147.5, 22.57) * mm});
            skLineSegment(sketch, "E1176", {"start": v(147.5, 22.57) * mm, "end": v(147.8, 23.64) * mm});
            skLineSegment(sketch, "E1177", {"start": v(147.8, 23.64) * mm, "end": v(147.67, 24.2) * mm});
            skLineSegment(sketch, "E1178", {"start": v(147.67, 24.2) * mm, "end": v(147.04, 24.45) * mm});
            skLineSegment(sketch, "E1179", {"start": v(147.04, 24.45) * mm, "end": v(146.48, 24.57) * mm});
            skLineSegment(sketch, "E1180", {"start": v(146.48, 24.57) * mm, "end": v(145.92, 24.7) * mm});
            skLineSegment(sketch, "E1181", {"start": v(145.92, 24.7) * mm, "end": v(145.4, 24.67) * mm});
            skLineSegment(sketch, "E1182", {"start": v(141.3, 20.72) * mm, "end": v(141.03, 21) * mm});
            skLineSegment(sketch, "E1183", {"start": v(141.03, 21) * mm, "end": v(140.73, 21.63) * mm});
            skLineSegment(sketch, "E1184", {"start": v(140.73, 21.63) * mm, "end": v(140.87, 22.1) * mm});
            skLineSegment(sketch, "E1185", {"start": v(140.87, 22.1) * mm, "end": v(141.03, 22.25) * mm});
            skLineSegment(sketch, "E1186", {"start": v(141.03, 22.25) * mm, "end": v(141.57, 22.23) * mm});
            skLineSegment(sketch, "E1187", {"start": v(141.57, 22.23) * mm, "end": v(142.3, 22.37) * mm});
            skLineSegment(sketch, "E1188", {"start": v(142.3, 22.37) * mm, "end": v(142.91, 22.68) * mm});
            skLineSegment(sketch, "E1189", {"start": v(142.91, 22.68) * mm, "end": v(143.39, 22.84) * mm});
            skLineSegment(sketch, "E1190", {"start": v(143.39, 22.84) * mm, "end": v(143.63, 22.85) * mm});
            skLineSegment(sketch, "E1191", {"start": v(143.63, 22.85) * mm, "end": v(143.86, 22.74) * mm});
            skLineSegment(sketch, "E1192", {"start": v(143.86, 22.74) * mm, "end": v(144.25, 22.59) * mm});
            skLineSegment(sketch, "E1193", {"start": v(144.25, 22.59) * mm, "end": v(144.28, 22.25) * mm});
            skLineSegment(sketch, "E1194", {"start": v(144.28, 22.25) * mm, "end": v(144.3, 21.68) * mm});
            skLineSegment(sketch, "E1195", {"start": v(144.3, 21.68) * mm, "end": v(144.33, 21.15) * mm});
            skLineSegment(sketch, "E1196", {"start": v(144.33, 21.15) * mm, "end": v(144.3, 20.69) * mm});
            skLineSegment(sketch, "E1197", {"start": v(144.3, 20.69) * mm, "end": v(144.23, 20.38) * mm});
            skLineSegment(sketch, "E1198", {"start": v(144.23, 20.38) * mm, "end": v(143.94, 19.84) * mm});
            skLineSegment(sketch, "E1199", {"start": v(143.94, 19.84) * mm, "end": v(143.64, 19.5) * mm});
            skLineSegment(sketch, "E1200", {"start": v(143.64, 19.5) * mm, "end": v(143.34, 19.1) * mm});
            skLineSegment(sketch, "E1201", {"start": v(143.34, 19.1) * mm, "end": v(142.9, 19.54) * mm});
            skLineSegment(sketch, "E1202", {"start": v(142.9, 19.54) * mm, "end": v(142.3, 20.06) * mm});
            skLineSegment(sketch, "E1203", {"start": v(142.3, 20.06) * mm, "end": v(141.9, 20.38) * mm});
            skLineSegment(sketch, "E1204", {"start": v(141.9, 20.38) * mm, "end": v(141.49, 20.6) * mm});
            skLineSegment(sketch, "E1205", {"start": v(141.49, 20.6) * mm, "end": v(141.3, 20.72) * mm});
            skLineSegment(sketch, "E1206", {"start": v(143.76, 18.53) * mm, "end": v(144.77, 20) * mm});
            skLineSegment(sketch, "E1207", {"start": v(144.77, 20) * mm, "end": v(145.8, 19.63) * mm});
            skLineSegment(sketch, "E1208", {"start": v(145.8, 19.63) * mm, "end": v(146.28, 18.83) * mm});
            skLineSegment(sketch, "E1209", {"start": v(146.28, 18.83) * mm, "end": v(146.24, 17.9) * mm});
            skLineSegment(sketch, "E1210", {"start": v(146.24, 17.9) * mm, "end": v(145.18, 17.82) * mm});
            skLineSegment(sketch, "E1211", {"start": v(145.18, 17.82) * mm, "end": v(144.65, 17.82) * mm});
            skLineSegment(sketch, "E1212", {"start": v(144.65, 17.82) * mm, "end": v(144.69, 17.07) * mm});
            skLineSegment(sketch, "E1213", {"start": v(144.69, 17.07) * mm, "end": v(143.76, 18.53) * mm});
            skLineSegment(sketch, "E1214", {"start": v(136.59, 20.97) * mm, "end": v(136.59, 20.38) * mm});
            skLineSegment(sketch, "E1215", {"start": v(136.59, 20.38) * mm, "end": v(136.59, 19.6) * mm});
            skLineSegment(sketch, "E1216", {"start": v(136.59, 19.6) * mm, "end": v(136.87, 19.02) * mm});
            skLineSegment(sketch, "E1217", {"start": v(136.87, 19.02) * mm, "end": v(137.18, 18.54) * mm});
            skLineSegment(sketch, "E1218", {"start": v(137.18, 18.54) * mm, "end": v(137.67, 18.05) * mm});
            skLineSegment(sketch, "E1219", {"start": v(137.67, 18.05) * mm, "end": v(138.29, 17.65) * mm});
            skLineSegment(sketch, "E1220", {"start": v(138.29, 17.65) * mm, "end": v(139.3, 17.6) * mm});
            skLineSegment(sketch, "E1221", {"start": v(139.3, 17.6) * mm, "end": v(140.17, 17.65) * mm});
            skLineSegment(sketch, "E1222", {"start": v(140.17, 17.65) * mm, "end": v(141.56, 17.56) * mm});
            skLineSegment(sketch, "E1223", {"start": v(141.56, 17.56) * mm, "end": v(142.09, 17.56) * mm});
            skLineSegment(sketch, "E1224", {"start": v(142.09, 17.56) * mm, "end": v(142.22, 17.5) * mm});
            skLineSegment(sketch, "E1225", {"start": v(142.22, 17.5) * mm, "end": v(142.42, 17.98) * mm});
            skLineSegment(sketch, "E1226", {"start": v(142.42, 17.98) * mm, "end": v(142.7, 18.45) * mm});
            skLineSegment(sketch, "E1227", {"start": v(142.7, 18.45) * mm, "end": v(141.76, 19.13) * mm});
            skLineSegment(sketch, "E1228", {"start": v(141.76, 19.13) * mm, "end": v(141.1, 19.93) * mm});
            skLineSegment(sketch, "E1229", {"start": v(141.1, 19.93) * mm, "end": v(140.63, 20.53) * mm});
            skLineSegment(sketch, "E1230", {"start": v(140.63, 20.53) * mm, "end": v(140.23, 20.57) * mm});
            skLineSegment(sketch, "E1231", {"start": v(140.23, 20.57) * mm, "end": v(138.84, 20.6) * mm});
            skLineSegment(sketch, "E1232", {"start": v(138.84, 20.6) * mm, "end": v(137.96, 20.92) * mm});
            skLineSegment(sketch, "E1233", {"start": v(137.96, 20.92) * mm, "end": v(137.36, 20.97) * mm});
            skLineSegment(sketch, "E1234", {"start": v(137.36, 20.97) * mm, "end": v(136.59, 20.97) * mm});
            skLineSegment(sketch, "E1235", {"start": v(143.4, 17.65) * mm, "end": v(142.81, 16.99) * mm});
            skLineSegment(sketch, "E1236", {"start": v(142.81, 16.99) * mm, "end": v(142.79, 16.32) * mm});
            skLineSegment(sketch, "E1237", {"start": v(142.79, 16.32) * mm, "end": v(143.56, 14.84) * mm});
            skLineSegment(sketch, "E1238", {"start": v(143.56, 14.84) * mm, "end": v(144.1, 15.55) * mm});
            skLineSegment(sketch, "E1239", {"start": v(144.1, 15.55) * mm, "end": v(144.25, 16.77) * mm});
            skLineSegment(sketch, "E1240", {"start": v(144.25, 16.77) * mm, "end": v(143.4, 17.65) * mm});
            skLineSegment(sketch, "E1241", {"start": v(138.1, 15.73) * mm, "end": v(137.82, 15.09) * mm});
            skLineSegment(sketch, "E1242", {"start": v(137.82, 15.09) * mm, "end": v(137.88, 14.31) * mm});
            skLineSegment(sketch, "E1243", {"start": v(137.88, 14.31) * mm, "end": v(138.24, 13.54) * mm});
            skLineSegment(sketch, "E1244", {"start": v(138.24, 13.54) * mm, "end": v(138.81, 13.25) * mm});
            skLineSegment(sketch, "E1245", {"start": v(138.81, 13.25) * mm, "end": v(139.8, 13.12) * mm});
            skLineSegment(sketch, "E1246", {"start": v(139.8, 13.12) * mm, "end": v(140.93, 12.97) * mm});
            skLineSegment(sketch, "E1247", {"start": v(140.93, 12.97) * mm, "end": v(141.8, 12.86) * mm});
            skLineSegment(sketch, "E1248", {"start": v(141.8, 12.86) * mm, "end": v(142.88, 14.07) * mm});
            skLineSegment(sketch, "E1249", {"start": v(142.88, 14.07) * mm, "end": v(142.3, 15.9) * mm});
            skLineSegment(sketch, "E1250", {"start": v(142.3, 15.9) * mm, "end": v(140.54, 15.68) * mm});
            skLineSegment(sketch, "E1251", {"start": v(140.54, 15.68) * mm, "end": v(139.03, 15.75) * mm});
            skLineSegment(sketch, "E1252", {"start": v(139.03, 15.75) * mm, "end": v(138.1, 15.73) * mm});
            skLineSegment(sketch, "E1253", {"start": v(143.76, 13.85) * mm, "end": v(144.53, 15.3) * mm});
            skLineSegment(sketch, "E1254", {"start": v(144.53, 15.3) * mm, "end": v(145.03, 15.45) * mm});
            skLineSegment(sketch, "E1255", {"start": v(145.03, 15.45) * mm, "end": v(145, 15.96) * mm});
            skLineSegment(sketch, "E1256", {"start": v(145, 15.96) * mm, "end": v(145.53, 15.63) * mm});
            skLineSegment(sketch, "E1257", {"start": v(145.53, 15.63) * mm, "end": v(145.86, 15.02) * mm});
            skLineSegment(sketch, "E1258", {"start": v(145.86, 15.02) * mm, "end": v(145.86, 14.85) * mm});
            skLineSegment(sketch, "E1259", {"start": v(145.86, 14.85) * mm, "end": v(144.89, 14.91) * mm});
            skLineSegment(sketch, "E1260", {"start": v(144.89, 14.91) * mm, "end": v(144.8, 14.32) * mm});
            skLineSegment(sketch, "E1261", {"start": v(144.8, 14.32) * mm, "end": v(144.82, 13.65) * mm});
            skLineSegment(sketch, "E1262", {"start": v(144.82, 13.65) * mm, "end": v(144.98, 13.04) * mm});
            skLineSegment(sketch, "E1263", {"start": v(144.98, 13.04) * mm, "end": v(144.59, 12.79) * mm});
            skLineSegment(sketch, "E1264", {"start": v(144.59, 12.79) * mm, "end": v(144.36, 12.73) * mm});
            skLineSegment(sketch, "E1265", {"start": v(144.36, 12.73) * mm, "end": v(143.76, 13.85) * mm});
            skLineSegment(sketch, "E1266", {"start": v(143.02, 9.83) * mm, "end": v(141.49, 8.04) * mm});
            skLineSegment(sketch, "E1267", {"start": v(141.49, 8.04) * mm, "end": v(140.99, 6.73) * mm});
            skLineSegment(sketch, "E1268", {"start": v(140.99, 6.73) * mm, "end": v(141.02, 5.92) * mm});
            skLineSegment(sketch, "E1269", {"start": v(141.02, 5.92) * mm, "end": v(141.18, 5.54) * mm});
            skLineSegment(sketch, "E1270", {"start": v(141.18, 5.54) * mm, "end": v(142.86, 5.42) * mm});
            skLineSegment(sketch, "E1271", {"start": v(142.86, 5.42) * mm, "end": v(143.99, 7.36) * mm});
            skLineSegment(sketch, "E1272", {"start": v(143.99, 7.36) * mm, "end": v(143.93, 8.7) * mm});
            skLineSegment(sketch, "E1273", {"start": v(143.93, 8.7) * mm, "end": v(143.02, 9.83) * mm});
            skLineSegment(sketch, "E1274", {"start": v(138.6, 11.37) * mm, "end": v(138.1, 11.17) * mm});
            skLineSegment(sketch, "E1275", {"start": v(138.1, 11.17) * mm, "end": v(138.05, 10.47) * mm});
            skLineSegment(sketch, "E1276", {"start": v(138.05, 10.47) * mm, "end": v(138.16, 9.76) * mm});
            skLineSegment(sketch, "E1277", {"start": v(138.16, 9.76) * mm, "end": v(138.55, 9.33) * mm});
            skLineSegment(sketch, "E1278", {"start": v(138.55, 9.33) * mm, "end": v(139.45, 8.9) * mm});
            skLineSegment(sketch, "E1279", {"start": v(139.45, 8.9) * mm, "end": v(140.2, 8.53) * mm});
            skLineSegment(sketch, "E1280", {"start": v(140.2, 8.53) * mm, "end": v(140.68, 8.3) * mm});
            skLineSegment(sketch, "E1281", {"start": v(140.68, 8.3) * mm, "end": v(141.28, 9.03) * mm});
            skLineSegment(sketch, "E1282", {"start": v(141.28, 9.03) * mm, "end": v(141.68, 9.45) * mm});
            skLineSegment(sketch, "E1283", {"start": v(141.68, 9.45) * mm, "end": v(142.14, 9.72) * mm});
            skLineSegment(sketch, "E1284", {"start": v(142.14, 9.72) * mm, "end": v(142.5, 10.31) * mm});
            skLineSegment(sketch, "E1285", {"start": v(142.5, 10.31) * mm, "end": v(142.11, 11.2) * mm});
            skLineSegment(sketch, "E1286", {"start": v(142.11, 11.2) * mm, "end": v(140.93, 11.17) * mm});
            skLineSegment(sketch, "E1287", {"start": v(140.93, 11.17) * mm, "end": v(139.96, 11.29) * mm});
            skLineSegment(sketch, "E1288", {"start": v(139.96, 11.29) * mm, "end": v(139.29, 11.4) * mm});
            skLineSegment(sketch, "E1289", {"start": v(139.29, 11.4) * mm, "end": v(138.6, 11.37) * mm});
            skLineSegment(sketch, "E1290", {"start": v(143.2, 13.32) * mm, "end": v(142.5, 12.3) * mm});
            skLineSegment(sketch, "E1291", {"start": v(142.5, 12.3) * mm, "end": v(142.65, 11.72) * mm});
            skLineSegment(sketch, "E1292", {"start": v(142.65, 11.72) * mm, "end": v(143.11, 11.17) * mm});
            skLineSegment(sketch, "E1293", {"start": v(143.11, 11.17) * mm, "end": v(143.55, 12.16) * mm});
            skLineSegment(sketch, "E1294", {"start": v(143.55, 12.16) * mm, "end": v(143.66, 12.62) * mm});
            skLineSegment(sketch, "E1295", {"start": v(143.66, 12.62) * mm, "end": v(143.2, 13.32) * mm});
            skLineSegment(sketch, "E1296", {"start": v(144.65, 7.36) * mm, "end": v(143.93, 5.53) * mm});
            skLineSegment(sketch, "E1297", {"start": v(143.93, 5.53) * mm, "end": v(143.2, 4.92) * mm});
            skLineSegment(sketch, "E1298", {"start": v(143.2, 4.92) * mm, "end": v(143.44, 4.42) * mm});
            skLineSegment(sketch, "E1299", {"start": v(143.44, 4.42) * mm, "end": v(143.99, 4.66) * mm});
            skLineSegment(sketch, "E1300", {"start": v(143.99, 4.66) * mm, "end": v(144.99, 5.32) * mm});
            skLineSegment(sketch, "E1301", {"start": v(144.99, 5.32) * mm, "end": v(145.46, 6.02) * mm});
            skLineSegment(sketch, "E1302", {"start": v(145.46, 6.02) * mm, "end": v(145.33, 7.05) * mm});
            skLineSegment(sketch, "E1303", {"start": v(145.33, 7.05) * mm, "end": v(145.28, 7.58) * mm});
            skLineSegment(sketch, "E1304", {"start": v(145.28, 7.58) * mm, "end": v(144.65, 7.36) * mm});
            skLineSegment(sketch, "E1305", {"start": v(143.93, 11.13) * mm, "end": v(143.4, 10.64) * mm});
            skLineSegment(sketch, "E1306", {"start": v(143.4, 10.64) * mm, "end": v(143.92, 9.85) * mm});
            skLineSegment(sketch, "E1307", {"start": v(143.92, 9.85) * mm, "end": v(144.47, 8.87) * mm});
            skLineSegment(sketch, "E1308", {"start": v(144.47, 8.87) * mm, "end": v(145.37, 9.45) * mm});
            skLineSegment(sketch, "E1309", {"start": v(145.37, 9.45) * mm, "end": v(145.5, 10.23) * mm});
            skLineSegment(sketch, "E1310", {"start": v(145.5, 10.23) * mm, "end": v(145.3, 11.04) * mm});
            skLineSegment(sketch, "E1311", {"start": v(145.3, 11.04) * mm, "end": v(145.26, 11.24) * mm});
            skLineSegment(sketch, "E1312", {"start": v(145.26, 11.24) * mm, "end": v(144.51, 11.11) * mm});
            skLineSegment(sketch, "E1313", {"start": v(144.51, 11.11) * mm, "end": v(143.93, 11.13) * mm});
            skLineSegment(sketch, "E1314", {"start": v(138.4, 7.36) * mm, "end": v(137.93, 7.36) * mm});
            skLineSegment(sketch, "E1315", {"start": v(137.93, 7.36) * mm, "end": v(137.69, 6.98) * mm});
            skLineSegment(sketch, "E1316", {"start": v(137.69, 6.98) * mm, "end": v(137.6, 6.54) * mm});
            skLineSegment(sketch, "E1317", {"start": v(137.6, 6.54) * mm, "end": v(137.53, 6.11) * mm});
            skLineSegment(sketch, "E1318", {"start": v(137.53, 6.11) * mm, "end": v(137.76, 5.35) * mm});
            skLineSegment(sketch, "E1319", {"start": v(137.76, 5.35) * mm, "end": v(138.66, 4.7) * mm});
            skLineSegment(sketch, "E1320", {"start": v(138.66, 4.7) * mm, "end": v(139.27, 4.35) * mm});
            skLineSegment(sketch, "E1321", {"start": v(139.27, 4.35) * mm, "end": v(139.86, 4.12) * mm});
            skLineSegment(sketch, "E1322", {"start": v(139.86, 4.12) * mm, "end": v(140.5, 4.1) * mm});
            skLineSegment(sketch, "E1323", {"start": v(140.5, 4.1) * mm, "end": v(140.88, 4.3) * mm});
            skLineSegment(sketch, "E1324", {"start": v(140.88, 4.3) * mm, "end": v(140.74, 4.88) * mm});
            skLineSegment(sketch, "E1325", {"start": v(140.74, 4.88) * mm, "end": v(140.56, 5.42) * mm});
            skLineSegment(sketch, "E1326", {"start": v(140.56, 5.42) * mm, "end": v(140.48, 6.07) * mm});
            skLineSegment(sketch, "E1327", {"start": v(140.48, 6.07) * mm, "end": v(140.36, 6.58) * mm});
            skLineSegment(sketch, "E1328", {"start": v(140.36, 6.58) * mm, "end": v(139.78, 6.91) * mm});
            skLineSegment(sketch, "E1329", {"start": v(139.78, 6.91) * mm, "end": v(139.05, 7.23) * mm});
            skLineSegment(sketch, "E1330.bottom", {"start": v(144.7, 19.57) * mm, "end": v(144.75, 19.57) * mm});
            skLineSegment(sketch, "E1330.top", {"start": v(144.7, 18.04) * mm, "end": v(144.75, 18.04) * mm});
            skLineSegment(sketch, "E1330.left", {"start": v(144.7, 19.57) * mm, "end": v(144.7, 18.04) * mm});
            skLineSegment(sketch, "E1330.right", {"start": v(144.75, 19.57) * mm, "end": v(144.75, 18.04) * mm});
            skSolve(sketch);
        }
        {
            var Q0;
            Q0 = qSketchRegion(id + "F10", true);
            extrude(context, id + "F11", {"entities" : qUnion([Q0]), "depth" : 5 * mm});
        }
        {
            var Q0;
            Q0=makeQuery(id+"F11.opExtrude","SWEPT_BODY",BODY,{"disambiguationData":[OSD([sQuery(id+"F10.wireOp",EDGE,"E1033"),sQuery(id+"F10.wireOp",EDGE,"E1034"),sQuery(id+"F10.wireOp",EDGE,"E1035"),sQuery(id+"F10.wireOp",EDGE,"E1036"),sQuery(id+"F10.wireOp",EDGE,"E1037"),sQuery(id+"F10.wireOp",EDGE,"E1038"),sQuery(id+"F10.wireOp",EDGE,"E1039"),sQuery(id+"F10.wireOp",EDGE,"E1040"),sQuery(id+"F10.wireOp",EDGE,"E1041"),sQuery(id+"F10.wireOp",EDGE,"E1042"),sQuery(id+"F10.wireOp",EDGE,"E1043"),sQuery(id+"F10.wireOp",EDGE,"E1044"),sQuery(id+"F10.wireOp",EDGE,"E1045"),sQuery(id+"F10.wireOp",EDGE,"E1046"),sQuery(id+"F10.wireOp",EDGE,"E1047"),sQuery(id+"F10.wireOp",EDGE,"E1048"),sQuery(id+"F10.wireOp",EDGE,"E1049"),sQuery(id+"F10.wireOp",EDGE,"E1050"),sQuery(id+"F10.wireOp",EDGE,"E1051"),sQuery(id+"F10.wireOp",EDGE,"E1052"),sQuery(id+"F10.wireOp",EDGE,"E1053"),sQuery(id+"F10.wireOp",EDGE,"E1054"),sQuery(id+"F10.wireOp",EDGE,"E1055"),sQuery(id+"F10.wireOp",EDGE,"E1056"),sQuery(id+"F10.wireOp",EDGE,"E1057"),sQuery(id+"F10.wireOp",EDGE,"E1058"),sQuery(id+"F10.wireOp",EDGE,"E1059"),sQuery(id+"F10.wireOp",EDGE,"E1060"),sQuery(id+"F10.wireOp",EDGE,"E1061"),sQuery(id+"F10.wireOp",EDGE,"E1062"),sQuery(id+"F10.wireOp",EDGE,"E1063"),sQuery(id+"F10.wireOp",EDGE,"E1064"),sQuery(id+"F10.wireOp",EDGE,"E1065"),sQuery(id+"F10.wireOp",EDGE,"E1066"),sQuery(id+"F10.wireOp",EDGE,"E1067"),sQuery(id+"F10.wireOp",EDGE,"E1068"),sQuery(id+"F10.wireOp",EDGE,"E1069"),sQuery(id+"F10.wireOp",EDGE,"E1070"),sQuery(id+"F10.wireOp",EDGE,"E1071"),sQuery(id+"F10.wireOp",EDGE,"E1072"),sQuery(id+"F10.wireOp",EDGE,"E1073"),sQuery(id+"F10.wireOp",EDGE,"E1074"),sQuery(id+"F10.wireOp",EDGE,"E1075"),sQuery(id+"F10.wireOp",EDGE,"E1076"),sQuery(id+"F10.wireOp",EDGE,"E1077"),sQuery(id+"F10.wireOp",EDGE,"E1078"),sQuery(id+"F10.wireOp",EDGE,"E1079"),sQuery(id+"F10.wireOp",EDGE,"E1080"),sQuery(id+"F10.wireOp",EDGE,"E1081"),sQuery(id+"F10.wireOp",EDGE,"E1082"),sQuery(id+"F10.wireOp",EDGE,"E1083"),sQuery(id+"F10.wireOp",EDGE,"E1084"),sQuery(id+"F10.wireOp",EDGE,"E1085"),sQuery(id+"F10.wireOp",EDGE,"E1086"),sQuery(id+"F10.wireOp",EDGE,"E1087"),sQuery(id+"F10.wireOp",EDGE,"E1088"),sQuery(id+"F10.wireOp",EDGE,"E1089"),sQuery(id+"F10.wireOp",EDGE,"E1090"),sQuery(id+"F10.wireOp",EDGE,"E1091"),sQuery(id+"F10.wireOp",EDGE,"E1092"),sQuery(id+"F10.wireOp",EDGE,"E1093"),sQuery(id+"F10.wireOp",EDGE,"E1094"),sQuery(id+"F10.wireOp",EDGE,"E1095"),sQuery(id+"F10.wireOp",EDGE,"E1096"),sQuery(id+"F10.wireOp",EDGE,"E1097"),sQuery(id+"F10.wireOp",EDGE,"E1098"),sQuery(id+"F10.wireOp",EDGE,"E1099"),sQuery(id+"F10.wireOp",EDGE,"E1100"),sQuery(id+"F10.wireOp",EDGE,"E1101"),sQuery(id+"F10.wireOp",EDGE,"E1102"),sQuery(id+"F10.wireOp",EDGE,"E1103"),sQuery(id+"F10.wireOp",EDGE,"E1104"),sQuery(id+"F10.wireOp",EDGE,"E1105"),sQuery(id+"F10.wireOp",EDGE,"E1106"),sQuery(id+"F10.wireOp",EDGE,"E1107"),sQuery(id+"F10.wireOp",EDGE,"E1108"),sQuery(id+"F10.wireOp",EDGE,"E1109"),sQuery(id+"F10.wireOp",EDGE,"E1110"),sQuery(id+"F10.wireOp",EDGE,"E1111"),sQuery(id+"F10.wireOp",EDGE,"E1112"),sQuery(id+"F10.wireOp",EDGE,"E1113"),sQuery(id+"F10.wireOp",EDGE,"E1114"),sQuery(id+"F10.wireOp",EDGE,"E1115"),sQuery(id+"F10.wireOp",EDGE,"E1118"),sQuery(id+"F10.wireOp",EDGE,"E1119"),sQuery(id+"F10.wireOp",EDGE,"E1120"),sQuery(id+"F10.wireOp",EDGE,"E1121"),sQuery(id+"F10.wireOp",EDGE,"E1122"),sQuery(id+"F10.wireOp",EDGE,"E1123"),sQuery(id+"F10.wireOp",EDGE,"E1124"),sQuery(id+"F10.wireOp",EDGE,"E1125"),sQuery(id+"F10.wireOp",EDGE,"E1126"),sQuery(id+"F10.wireOp",EDGE,"E1127"),sQuery(id+"F10.wireOp",EDGE,"E1128"),sQuery(id+"F10.wireOp",EDGE,"E1129"),sQuery(id+"F10.wireOp",EDGE,"E1130"),sQuery(id+"F10.wireOp",EDGE,"E1131"),sQuery(id+"F10.wireOp",EDGE,"E1132"),sQuery(id+"F10.wireOp",EDGE,"E1133"),sQuery(id+"F10.wireOp",EDGE,"E1134"),sQuery(id+"F10.wireOp",EDGE,"E1135"),sQuery(id+"F10.wireOp",EDGE,"E1136"),sQuery(id+"F10.wireOp",EDGE,"E1137"),sQuery(id+"F10.wireOp",EDGE,"E1138"),sQuery(id+"F10.wireOp",EDGE,"E1139"),sQuery(id+"F10.wireOp",EDGE,"E1140"),sQuery(id+"F10.wireOp",EDGE,"E1141"),sQuery(id+"F10.wireOp",EDGE,"E1142"),sQuery(id+"F10.wireOp",EDGE,"E1143"),sQuery(id+"F10.wireOp",EDGE,"E1144"),sQuery(id+"F10.wireOp",EDGE,"E1145"),sQuery(id+"F10.wireOp",EDGE,"E1146"),sQuery(id+"F10.wireOp",EDGE,"E1147"),sQuery(id+"F10.wireOp",EDGE,"E1148"),sQuery(id+"F10.wireOp",EDGE,"E1149"),sQuery(id+"F10.wireOp",EDGE,"E1150"),sQuery(id+"F10.wireOp",EDGE,"E1151"),sQuery(id+"F10.wireOp",EDGE,"E1152"),sQuery(id+"F10.wireOp",EDGE,"E1153"),sQuery(id+"F10.wireOp",EDGE,"E1154"),sQuery(id+"F10.wireOp",EDGE,"E1155"),sQuery(id+"F10.wireOp",EDGE,"E1156"),sQuery(id+"F10.wireOp",EDGE,"E1157"),sQuery(id+"F10.wireOp",EDGE,"E1158"),sQuery(id+"F10.wireOp",EDGE,"E1159"),sQuery(id+"F10.wireOp",EDGE,"E1160"),sQuery(id+"F10.wireOp",EDGE,"E1161"),sQuery(id+"F10.wireOp",EDGE,"E1162"),sQuery(id+"F10.wireOp",EDGE,"E1163"),sQuery(id+"F10.wireOp",EDGE,"E1164"),sQuery(id+"F10.wireOp",EDGE,"E1165"),sQuery(id+"F10.wireOp",EDGE,"E1166"),sQuery(id+"F10.wireOp",EDGE,"E1167"),sQuery(id+"F10.wireOp",EDGE,"E1168"),sQuery(id+"F10.wireOp",EDGE,"E1169"),sQuery(id+"F10.wireOp",EDGE,"E1170"),sQuery(id+"F10.wireOp",EDGE,"E1171"),sQuery(id+"F10.wireOp",EDGE,"E1172"),sQuery(id+"F10.wireOp",EDGE,"E1173"),sQuery(id+"F10.wireOp",EDGE,"E1174"),sQuery(id+"F10.wireOp",EDGE,"E1175"),sQuery(id+"F10.wireOp",EDGE,"E1176"),sQuery(id+"F10.wireOp",EDGE,"E1177"),sQuery(id+"F10.wireOp",EDGE,"E1178"),sQuery(id+"F10.wireOp",EDGE,"E1179"),sQuery(id+"F10.wireOp",EDGE,"E1180"),sQuery(id+"F10.wireOp",EDGE,"E1181"),sQuery(id+"F10.wireOp",EDGE,"E1182"),sQuery(id+"F10.wireOp",EDGE,"E1183"),sQuery(id+"F10.wireOp",EDGE,"E1184"),sQuery(id+"F10.wireOp",EDGE,"E1185"),sQuery(id+"F10.wireOp",EDGE,"E1186"),sQuery(id+"F10.wireOp",EDGE,"E1187"),sQuery(id+"F10.wireOp",EDGE,"E1188"),sQuery(id+"F10.wireOp",EDGE,"E1189"),sQuery(id+"F10.wireOp",EDGE,"E1190"),sQuery(id+"F10.wireOp",EDGE,"E1191"),sQuery(id+"F10.wireOp",EDGE,"E1192"),sQuery(id+"F10.wireOp",EDGE,"E1193"),sQuery(id+"F10.wireOp",EDGE,"E1194"),sQuery(id+"F10.wireOp",EDGE,"E1195"),sQuery(id+"F10.wireOp",EDGE,"E1196"),sQuery(id+"F10.wireOp",EDGE,"E1197"),sQuery(id+"F10.wireOp",EDGE,"E1198"),sQuery(id+"F10.wireOp",EDGE,"E1199"),sQuery(id+"F10.wireOp",EDGE,"E1200"),sQuery(id+"F10.wireOp",EDGE,"E1201"),sQuery(id+"F10.wireOp",EDGE,"E1202"),sQuery(id+"F10.wireOp",EDGE,"E1203"),sQuery(id+"F10.wireOp",EDGE,"E1204"),sQuery(id+"F10.wireOp",EDGE,"E1205"),sQuery(id+"F10.wireOp",EDGE,"E1206"),sQuery(id+"F10.wireOp",EDGE,"E1207"),sQuery(id+"F10.wireOp",EDGE,"E1208"),sQuery(id+"F10.wireOp",EDGE,"E1209"),sQuery(id+"F10.wireOp",EDGE,"E1210"),sQuery(id+"F10.wireOp",EDGE,"E1211"),sQuery(id+"F10.wireOp",EDGE,"E1212"),sQuery(id+"F10.wireOp",EDGE,"E1213"),sQuery(id+"F10.wireOp",EDGE,"E1214"),sQuery(id+"F10.wireOp",EDGE,"E1215"),sQuery(id+"F10.wireOp",EDGE,"E1216"),sQuery(id+"F10.wireOp",EDGE,"E1217"),sQuery(id+"F10.wireOp",EDGE,"E1218"),sQuery(id+"F10.wireOp",EDGE,"E1219"),sQuery(id+"F10.wireOp",EDGE,"E1220"),sQuery(id+"F10.wireOp",EDGE,"E1221"),sQuery(id+"F10.wireOp",EDGE,"E1222"),sQuery(id+"F10.wireOp",EDGE,"E1223"),sQuery(id+"F10.wireOp",EDGE,"E1224"),sQuery(id+"F10.wireOp",EDGE,"E1225"),sQuery(id+"F10.wireOp",EDGE,"E1226"),sQuery(id+"F10.wireOp",EDGE,"E1227"),sQuery(id+"F10.wireOp",EDGE,"E1228"),sQuery(id+"F10.wireOp",EDGE,"E1229"),sQuery(id+"F10.wireOp",EDGE,"E1230"),sQuery(id+"F10.wireOp",EDGE,"E1231"),sQuery(id+"F10.wireOp",EDGE,"E1232"),sQuery(id+"F10.wireOp",EDGE,"E1233"),sQuery(id+"F10.wireOp",EDGE,"E1234"),sQuery(id+"F10.wireOp",EDGE,"E1235"),sQuery(id+"F10.wireOp",EDGE,"E1236"),sQuery(id+"F10.wireOp",EDGE,"E1237"),sQuery(id+"F10.wireOp",EDGE,"E1238"),sQuery(id+"F10.wireOp",EDGE,"E1239"),sQuery(id+"F10.wireOp",EDGE,"E1240"),sQuery(id+"F10.wireOp",EDGE,"E1241"),sQuery(id+"F10.wireOp",EDGE,"E1242"),sQuery(id+"F10.wireOp",EDGE,"E1243"),sQuery(id+"F10.wireOp",EDGE,"E1244"),sQuery(id+"F10.wireOp",EDGE,"E1245"),sQuery(id+"F10.wireOp",EDGE,"E1246"),sQuery(id+"F10.wireOp",EDGE,"E1247"),sQuery(id+"F10.wireOp",EDGE,"E1248"),sQuery(id+"F10.wireOp",EDGE,"E1249"),sQuery(id+"F10.wireOp",EDGE,"E1250"),sQuery(id+"F10.wireOp",EDGE,"E1251"),sQuery(id+"F10.wireOp",EDGE,"E1252"),sQuery(id+"F10.wireOp",EDGE,"E1253"),sQuery(id+"F10.wireOp",EDGE,"E1254"),sQuery(id+"F10.wireOp",EDGE,"E1255"),sQuery(id+"F10.wireOp",EDGE,"E1256"),sQuery(id+"F10.wireOp",EDGE,"E1257"),sQuery(id+"F10.wireOp",EDGE,"E1258"),sQuery(id+"F10.wireOp",EDGE,"E1259"),sQuery(id+"F10.wireOp",EDGE,"E1260"),sQuery(id+"F10.wireOp",EDGE,"E1261"),sQuery(id+"F10.wireOp",EDGE,"E1262"),sQuery(id+"F10.wireOp",EDGE,"E1263"),sQuery(id+"F10.wireOp",EDGE,"E1264"),sQuery(id+"F10.wireOp",EDGE,"E1265"),sQuery(id+"F10.wireOp",EDGE,"E1266"),sQuery(id+"F10.wireOp",EDGE,"E1267"),sQuery(id+"F10.wireOp",EDGE,"E1268"),sQuery(id+"F10.wireOp",EDGE,"E1269"),sQuery(id+"F10.wireOp",EDGE,"E1270"),sQuery(id+"F10.wireOp",EDGE,"E1271"),sQuery(id+"F10.wireOp",EDGE,"E1272"),sQuery(id+"F10.wireOp",EDGE,"E1273"),sQuery(id+"F10.wireOp",EDGE,"E1274"),sQuery(id+"F10.wireOp",EDGE,"E1275"),sQuery(id+"F10.wireOp",EDGE,"E1276"),sQuery(id+"F10.wireOp",EDGE,"E1277"),sQuery(id+"F10.wireOp",EDGE,"E1278"),sQuery(id+"F10.wireOp",EDGE,"E1279"),sQuery(id+"F10.wireOp",EDGE,"E1280"),sQuery(id+"F10.wireOp",EDGE,"E1281"),sQuery(id+"F10.wireOp",EDGE,"E1282"),sQuery(id+"F10.wireOp",EDGE,"E1283"),sQuery(id+"F10.wireOp",EDGE,"E1284"),sQuery(id+"F10.wireOp",EDGE,"E1285"),sQuery(id+"F10.wireOp",EDGE,"E1286"),sQuery(id+"F10.wireOp",EDGE,"E1287"),sQuery(id+"F10.wireOp",EDGE,"E1288"),sQuery(id+"F10.wireOp",EDGE,"E1289"),sQuery(id+"F10.wireOp",EDGE,"E1290"),sQuery(id+"F10.wireOp",EDGE,"E1291"),sQuery(id+"F10.wireOp",EDGE,"E1292"),sQuery(id+"F10.wireOp",EDGE,"E1293"),sQuery(id+"F10.wireOp",EDGE,"E1294"),sQuery(id+"F10.wireOp",EDGE,"E1295"),sQuery(id+"F10.wireOp",EDGE,"E1296"),sQuery(id+"F10.wireOp",EDGE,"E1297"),sQuery(id+"F10.wireOp",EDGE,"E1298"),sQuery(id+"F10.wireOp",EDGE,"E1299"),sQuery(id+"F10.wireOp",EDGE,"E1300"),sQuery(id+"F10.wireOp",EDGE,"E1301"),sQuery(id+"F10.wireOp",EDGE,"E1302"),sQuery(id+"F10.wireOp",EDGE,"E1303"),sQuery(id+"F10.wireOp",EDGE,"E1304"),sQuery(id+"F10.wireOp",EDGE,"E1305"),sQuery(id+"F10.wireOp",EDGE,"E1306"),sQuery(id+"F10.wireOp",EDGE,"E1307"),sQuery(id+"F10.wireOp",EDGE,"E1308"),sQuery(id+"F10.wireOp",EDGE,"E1309"),sQuery(id+"F10.wireOp",EDGE,"E1310"),sQuery(id+"F10.wireOp",EDGE,"E1311"),sQuery(id+"F10.wireOp",EDGE,"E1312"),sQuery(id+"F10.wireOp",EDGE,"E1313")])]});
            var Q1;
            Q1=makeQuery(id+"F11.opExtrude","CAP_VERTEX",VERTEX,{"disambiguationData":[OSD([sQuery(id+"F10.wireOp",EDGE,"E1108"),sQuery(id+"F10.wireOp",EDGE,"E1109")])],"isStart":false});
            transform(context, id + "F12", {"entities" : qUnion([Q0]), "transformType" : TransformType.SCALE_UNIFORMLY, "scale" : 1.3, "scalePoint" : qUnion([Q1]), "makeCopy" : false});
        }
        {
            var Q0;
            Q0=makeQuery(id+"F11.opExtrude","SWEPT_BODY",BODY,{"disambiguationData":[OSD([sQuery(id+"F10.wireOp",EDGE,"E1033"),sQuery(id+"F10.wireOp",EDGE,"E1034"),sQuery(id+"F10.wireOp",EDGE,"E1035"),sQuery(id+"F10.wireOp",EDGE,"E1036"),sQuery(id+"F10.wireOp",EDGE,"E1037"),sQuery(id+"F10.wireOp",EDGE,"E1038"),sQuery(id+"F10.wireOp",EDGE,"E1039"),sQuery(id+"F10.wireOp",EDGE,"E1040"),sQuery(id+"F10.wireOp",EDGE,"E1041"),sQuery(id+"F10.wireOp",EDGE,"E1042"),sQuery(id+"F10.wireOp",EDGE,"E1043"),sQuery(id+"F10.wireOp",EDGE,"E1044"),sQuery(id+"F10.wireOp",EDGE,"E1045"),sQuery(id+"F10.wireOp",EDGE,"E1046"),sQuery(id+"F10.wireOp",EDGE,"E1047"),sQuery(id+"F10.wireOp",EDGE,"E1048"),sQuery(id+"F10.wireOp",EDGE,"E1049"),sQuery(id+"F10.wireOp",EDGE,"E1050"),sQuery(id+"F10.wireOp",EDGE,"E1051"),sQuery(id+"F10.wireOp",EDGE,"E1052"),sQuery(id+"F10.wireOp",EDGE,"E1053"),sQuery(id+"F10.wireOp",EDGE,"E1054"),sQuery(id+"F10.wireOp",EDGE,"E1055"),sQuery(id+"F10.wireOp",EDGE,"E1056"),sQuery(id+"F10.wireOp",EDGE,"E1057"),sQuery(id+"F10.wireOp",EDGE,"E1058"),sQuery(id+"F10.wireOp",EDGE,"E1059"),sQuery(id+"F10.wireOp",EDGE,"E1060"),sQuery(id+"F10.wireOp",EDGE,"E1061"),sQuery(id+"F10.wireOp",EDGE,"E1062"),sQuery(id+"F10.wireOp",EDGE,"E1063"),sQuery(id+"F10.wireOp",EDGE,"E1064"),sQuery(id+"F10.wireOp",EDGE,"E1065"),sQuery(id+"F10.wireOp",EDGE,"E1066"),sQuery(id+"F10.wireOp",EDGE,"E1067"),sQuery(id+"F10.wireOp",EDGE,"E1068"),sQuery(id+"F10.wireOp",EDGE,"E1069"),sQuery(id+"F10.wireOp",EDGE,"E1070"),sQuery(id+"F10.wireOp",EDGE,"E1071"),sQuery(id+"F10.wireOp",EDGE,"E1072"),sQuery(id+"F10.wireOp",EDGE,"E1073"),sQuery(id+"F10.wireOp",EDGE,"E1074"),sQuery(id+"F10.wireOp",EDGE,"E1075"),sQuery(id+"F10.wireOp",EDGE,"E1076"),sQuery(id+"F10.wireOp",EDGE,"E1077"),sQuery(id+"F10.wireOp",EDGE,"E1078"),sQuery(id+"F10.wireOp",EDGE,"E1079"),sQuery(id+"F10.wireOp",EDGE,"E1080"),sQuery(id+"F10.wireOp",EDGE,"E1081"),sQuery(id+"F10.wireOp",EDGE,"E1082"),sQuery(id+"F10.wireOp",EDGE,"E1083"),sQuery(id+"F10.wireOp",EDGE,"E1084"),sQuery(id+"F10.wireOp",EDGE,"E1085"),sQuery(id+"F10.wireOp",EDGE,"E1086"),sQuery(id+"F10.wireOp",EDGE,"E1087"),sQuery(id+"F10.wireOp",EDGE,"E1088"),sQuery(id+"F10.wireOp",EDGE,"E1089"),sQuery(id+"F10.wireOp",EDGE,"E1090"),sQuery(id+"F10.wireOp",EDGE,"E1091"),sQuery(id+"F10.wireOp",EDGE,"E1092"),sQuery(id+"F10.wireOp",EDGE,"E1093"),sQuery(id+"F10.wireOp",EDGE,"E1094"),sQuery(id+"F10.wireOp",EDGE,"E1095"),sQuery(id+"F10.wireOp",EDGE,"E1096"),sQuery(id+"F10.wireOp",EDGE,"E1097"),sQuery(id+"F10.wireOp",EDGE,"E1098"),sQuery(id+"F10.wireOp",EDGE,"E1099"),sQuery(id+"F10.wireOp",EDGE,"E1100"),sQuery(id+"F10.wireOp",EDGE,"E1101"),sQuery(id+"F10.wireOp",EDGE,"E1102"),sQuery(id+"F10.wireOp",EDGE,"E1103"),sQuery(id+"F10.wireOp",EDGE,"E1104"),sQuery(id+"F10.wireOp",EDGE,"E1105"),sQuery(id+"F10.wireOp",EDGE,"E1106"),sQuery(id+"F10.wireOp",EDGE,"E1107"),sQuery(id+"F10.wireOp",EDGE,"E1108"),sQuery(id+"F10.wireOp",EDGE,"E1109"),sQuery(id+"F10.wireOp",EDGE,"E1110"),sQuery(id+"F10.wireOp",EDGE,"E1111"),sQuery(id+"F10.wireOp",EDGE,"E1112"),sQuery(id+"F10.wireOp",EDGE,"E1113"),sQuery(id+"F10.wireOp",EDGE,"E1114"),sQuery(id+"F10.wireOp",EDGE,"E1115"),sQuery(id+"F10.wireOp",EDGE,"E1118"),sQuery(id+"F10.wireOp",EDGE,"E1119"),sQuery(id+"F10.wireOp",EDGE,"E1120"),sQuery(id+"F10.wireOp",EDGE,"E1121"),sQuery(id+"F10.wireOp",EDGE,"E1122"),sQuery(id+"F10.wireOp",EDGE,"E1123"),sQuery(id+"F10.wireOp",EDGE,"E1124"),sQuery(id+"F10.wireOp",EDGE,"E1125"),sQuery(id+"F10.wireOp",EDGE,"E1126"),sQuery(id+"F10.wireOp",EDGE,"E1127"),sQuery(id+"F10.wireOp",EDGE,"E1128"),sQuery(id+"F10.wireOp",EDGE,"E1129"),sQuery(id+"F10.wireOp",EDGE,"E1130"),sQuery(id+"F10.wireOp",EDGE,"E1131"),sQuery(id+"F10.wireOp",EDGE,"E1132"),sQuery(id+"F10.wireOp",EDGE,"E1133"),sQuery(id+"F10.wireOp",EDGE,"E1134"),sQuery(id+"F10.wireOp",EDGE,"E1135"),sQuery(id+"F10.wireOp",EDGE,"E1136"),sQuery(id+"F10.wireOp",EDGE,"E1137"),sQuery(id+"F10.wireOp",EDGE,"E1138"),sQuery(id+"F10.wireOp",EDGE,"E1139"),sQuery(id+"F10.wireOp",EDGE,"E1140"),sQuery(id+"F10.wireOp",EDGE,"E1141"),sQuery(id+"F10.wireOp",EDGE,"E1142"),sQuery(id+"F10.wireOp",EDGE,"E1143"),sQuery(id+"F10.wireOp",EDGE,"E1144"),sQuery(id+"F10.wireOp",EDGE,"E1145"),sQuery(id+"F10.wireOp",EDGE,"E1146"),sQuery(id+"F10.wireOp",EDGE,"E1147"),sQuery(id+"F10.wireOp",EDGE,"E1148"),sQuery(id+"F10.wireOp",EDGE,"E1149"),sQuery(id+"F10.wireOp",EDGE,"E1150"),sQuery(id+"F10.wireOp",EDGE,"E1151"),sQuery(id+"F10.wireOp",EDGE,"E1152"),sQuery(id+"F10.wireOp",EDGE,"E1153"),sQuery(id+"F10.wireOp",EDGE,"E1154"),sQuery(id+"F10.wireOp",EDGE,"E1155"),sQuery(id+"F10.wireOp",EDGE,"E1156"),sQuery(id+"F10.wireOp",EDGE,"E1157"),sQuery(id+"F10.wireOp",EDGE,"E1158"),sQuery(id+"F10.wireOp",EDGE,"E1159"),sQuery(id+"F10.wireOp",EDGE,"E1160"),sQuery(id+"F10.wireOp",EDGE,"E1161"),sQuery(id+"F10.wireOp",EDGE,"E1162"),sQuery(id+"F10.wireOp",EDGE,"E1163"),sQuery(id+"F10.wireOp",EDGE,"E1164"),sQuery(id+"F10.wireOp",EDGE,"E1165"),sQuery(id+"F10.wireOp",EDGE,"E1166"),sQuery(id+"F10.wireOp",EDGE,"E1167"),sQuery(id+"F10.wireOp",EDGE,"E1168"),sQuery(id+"F10.wireOp",EDGE,"E1169"),sQuery(id+"F10.wireOp",EDGE,"E1170"),sQuery(id+"F10.wireOp",EDGE,"E1171"),sQuery(id+"F10.wireOp",EDGE,"E1172"),sQuery(id+"F10.wireOp",EDGE,"E1173"),sQuery(id+"F10.wireOp",EDGE,"E1174"),sQuery(id+"F10.wireOp",EDGE,"E1175"),sQuery(id+"F10.wireOp",EDGE,"E1176"),sQuery(id+"F10.wireOp",EDGE,"E1177"),sQuery(id+"F10.wireOp",EDGE,"E1178"),sQuery(id+"F10.wireOp",EDGE,"E1179"),sQuery(id+"F10.wireOp",EDGE,"E1180"),sQuery(id+"F10.wireOp",EDGE,"E1181"),sQuery(id+"F10.wireOp",EDGE,"E1182"),sQuery(id+"F10.wireOp",EDGE,"E1183"),sQuery(id+"F10.wireOp",EDGE,"E1184"),sQuery(id+"F10.wireOp",EDGE,"E1185"),sQuery(id+"F10.wireOp",EDGE,"E1186"),sQuery(id+"F10.wireOp",EDGE,"E1187"),sQuery(id+"F10.wireOp",EDGE,"E1188"),sQuery(id+"F10.wireOp",EDGE,"E1189"),sQuery(id+"F10.wireOp",EDGE,"E1190"),sQuery(id+"F10.wireOp",EDGE,"E1191"),sQuery(id+"F10.wireOp",EDGE,"E1192"),sQuery(id+"F10.wireOp",EDGE,"E1193"),sQuery(id+"F10.wireOp",EDGE,"E1194"),sQuery(id+"F10.wireOp",EDGE,"E1195"),sQuery(id+"F10.wireOp",EDGE,"E1196"),sQuery(id+"F10.wireOp",EDGE,"E1197"),sQuery(id+"F10.wireOp",EDGE,"E1198"),sQuery(id+"F10.wireOp",EDGE,"E1199"),sQuery(id+"F10.wireOp",EDGE,"E1200"),sQuery(id+"F10.wireOp",EDGE,"E1201"),sQuery(id+"F10.wireOp",EDGE,"E1202"),sQuery(id+"F10.wireOp",EDGE,"E1203"),sQuery(id+"F10.wireOp",EDGE,"E1204"),sQuery(id+"F10.wireOp",EDGE,"E1205"),sQuery(id+"F10.wireOp",EDGE,"E1206"),sQuery(id+"F10.wireOp",EDGE,"E1207"),sQuery(id+"F10.wireOp",EDGE,"E1208"),sQuery(id+"F10.wireOp",EDGE,"E1209"),sQuery(id+"F10.wireOp",EDGE,"E1210"),sQuery(id+"F10.wireOp",EDGE,"E1211"),sQuery(id+"F10.wireOp",EDGE,"E1212"),sQuery(id+"F10.wireOp",EDGE,"E1213"),sQuery(id+"F10.wireOp",EDGE,"E1214"),sQuery(id+"F10.wireOp",EDGE,"E1215"),sQuery(id+"F10.wireOp",EDGE,"E1216"),sQuery(id+"F10.wireOp",EDGE,"E1217"),sQuery(id+"F10.wireOp",EDGE,"E1218"),sQuery(id+"F10.wireOp",EDGE,"E1219"),sQuery(id+"F10.wireOp",EDGE,"E1220"),sQuery(id+"F10.wireOp",EDGE,"E1221"),sQuery(id+"F10.wireOp",EDGE,"E1222"),sQuery(id+"F10.wireOp",EDGE,"E1223"),sQuery(id+"F10.wireOp",EDGE,"E1224"),sQuery(id+"F10.wireOp",EDGE,"E1225"),sQuery(id+"F10.wireOp",EDGE,"E1226"),sQuery(id+"F10.wireOp",EDGE,"E1227"),sQuery(id+"F10.wireOp",EDGE,"E1228"),sQuery(id+"F10.wireOp",EDGE,"E1229"),sQuery(id+"F10.wireOp",EDGE,"E1230"),sQuery(id+"F10.wireOp",EDGE,"E1231"),sQuery(id+"F10.wireOp",EDGE,"E1232"),sQuery(id+"F10.wireOp",EDGE,"E1233"),sQuery(id+"F10.wireOp",EDGE,"E1234"),sQuery(id+"F10.wireOp",EDGE,"E1235"),sQuery(id+"F10.wireOp",EDGE,"E1236"),sQuery(id+"F10.wireOp",EDGE,"E1237"),sQuery(id+"F10.wireOp",EDGE,"E1238"),sQuery(id+"F10.wireOp",EDGE,"E1239"),sQuery(id+"F10.wireOp",EDGE,"E1240"),sQuery(id+"F10.wireOp",EDGE,"E1241"),sQuery(id+"F10.wireOp",EDGE,"E1242"),sQuery(id+"F10.wireOp",EDGE,"E1243"),sQuery(id+"F10.wireOp",EDGE,"E1244"),sQuery(id+"F10.wireOp",EDGE,"E1245"),sQuery(id+"F10.wireOp",EDGE,"E1246"),sQuery(id+"F10.wireOp",EDGE,"E1247"),sQuery(id+"F10.wireOp",EDGE,"E1248"),sQuery(id+"F10.wireOp",EDGE,"E1249"),sQuery(id+"F10.wireOp",EDGE,"E1250"),sQuery(id+"F10.wireOp",EDGE,"E1251"),sQuery(id+"F10.wireOp",EDGE,"E1252"),sQuery(id+"F10.wireOp",EDGE,"E1253"),sQuery(id+"F10.wireOp",EDGE,"E1254"),sQuery(id+"F10.wireOp",EDGE,"E1255"),sQuery(id+"F10.wireOp",EDGE,"E1256"),sQuery(id+"F10.wireOp",EDGE,"E1257"),sQuery(id+"F10.wireOp",EDGE,"E1258"),sQuery(id+"F10.wireOp",EDGE,"E1259"),sQuery(id+"F10.wireOp",EDGE,"E1260"),sQuery(id+"F10.wireOp",EDGE,"E1261"),sQuery(id+"F10.wireOp",EDGE,"E1262"),sQuery(id+"F10.wireOp",EDGE,"E1263"),sQuery(id+"F10.wireOp",EDGE,"E1264"),sQuery(id+"F10.wireOp",EDGE,"E1265"),sQuery(id+"F10.wireOp",EDGE,"E1266"),sQuery(id+"F10.wireOp",EDGE,"E1267"),sQuery(id+"F10.wireOp",EDGE,"E1268"),sQuery(id+"F10.wireOp",EDGE,"E1269"),sQuery(id+"F10.wireOp",EDGE,"E1270"),sQuery(id+"F10.wireOp",EDGE,"E1271"),sQuery(id+"F10.wireOp",EDGE,"E1272"),sQuery(id+"F10.wireOp",EDGE,"E1273"),sQuery(id+"F10.wireOp",EDGE,"E1274"),sQuery(id+"F10.wireOp",EDGE,"E1275"),sQuery(id+"F10.wireOp",EDGE,"E1276"),sQuery(id+"F10.wireOp",EDGE,"E1277"),sQuery(id+"F10.wireOp",EDGE,"E1278"),sQuery(id+"F10.wireOp",EDGE,"E1279"),sQuery(id+"F10.wireOp",EDGE,"E1280"),sQuery(id+"F10.wireOp",EDGE,"E1281"),sQuery(id+"F10.wireOp",EDGE,"E1282"),sQuery(id+"F10.wireOp",EDGE,"E1283"),sQuery(id+"F10.wireOp",EDGE,"E1284"),sQuery(id+"F10.wireOp",EDGE,"E1285"),sQuery(id+"F10.wireOp",EDGE,"E1286"),sQuery(id+"F10.wireOp",EDGE,"E1287"),sQuery(id+"F10.wireOp",EDGE,"E1288"),sQuery(id+"F10.wireOp",EDGE,"E1289"),sQuery(id+"F10.wireOp",EDGE,"E1290"),sQuery(id+"F10.wireOp",EDGE,"E1291"),sQuery(id+"F10.wireOp",EDGE,"E1292"),sQuery(id+"F10.wireOp",EDGE,"E1293"),sQuery(id+"F10.wireOp",EDGE,"E1294"),sQuery(id+"F10.wireOp",EDGE,"E1295"),sQuery(id+"F10.wireOp",EDGE,"E1296"),sQuery(id+"F10.wireOp",EDGE,"E1297"),sQuery(id+"F10.wireOp",EDGE,"E1298"),sQuery(id+"F10.wireOp",EDGE,"E1299"),sQuery(id+"F10.wireOp",EDGE,"E1300"),sQuery(id+"F10.wireOp",EDGE,"E1301"),sQuery(id+"F10.wireOp",EDGE,"E1302"),sQuery(id+"F10.wireOp",EDGE,"E1303"),sQuery(id+"F10.wireOp",EDGE,"E1304"),sQuery(id+"F10.wireOp",EDGE,"E1305"),sQuery(id+"F10.wireOp",EDGE,"E1306"),sQuery(id+"F10.wireOp",EDGE,"E1307"),sQuery(id+"F10.wireOp",EDGE,"E1308"),sQuery(id+"F10.wireOp",EDGE,"E1309"),sQuery(id+"F10.wireOp",EDGE,"E1310"),sQuery(id+"F10.wireOp",EDGE,"E1311"),sQuery(id+"F10.wireOp",EDGE,"E1312"),sQuery(id+"F10.wireOp",EDGE,"E1313")])]});
            transform(context, id + "F13", {"entities" : qUnion([Q0]), "transformType" : TransformType.TRANSLATION_3D, "dx" : 0 * mm, "dy" : 0 * mm, "dz" : 0 * mm, "makeCopy" : true});
        }
    });
